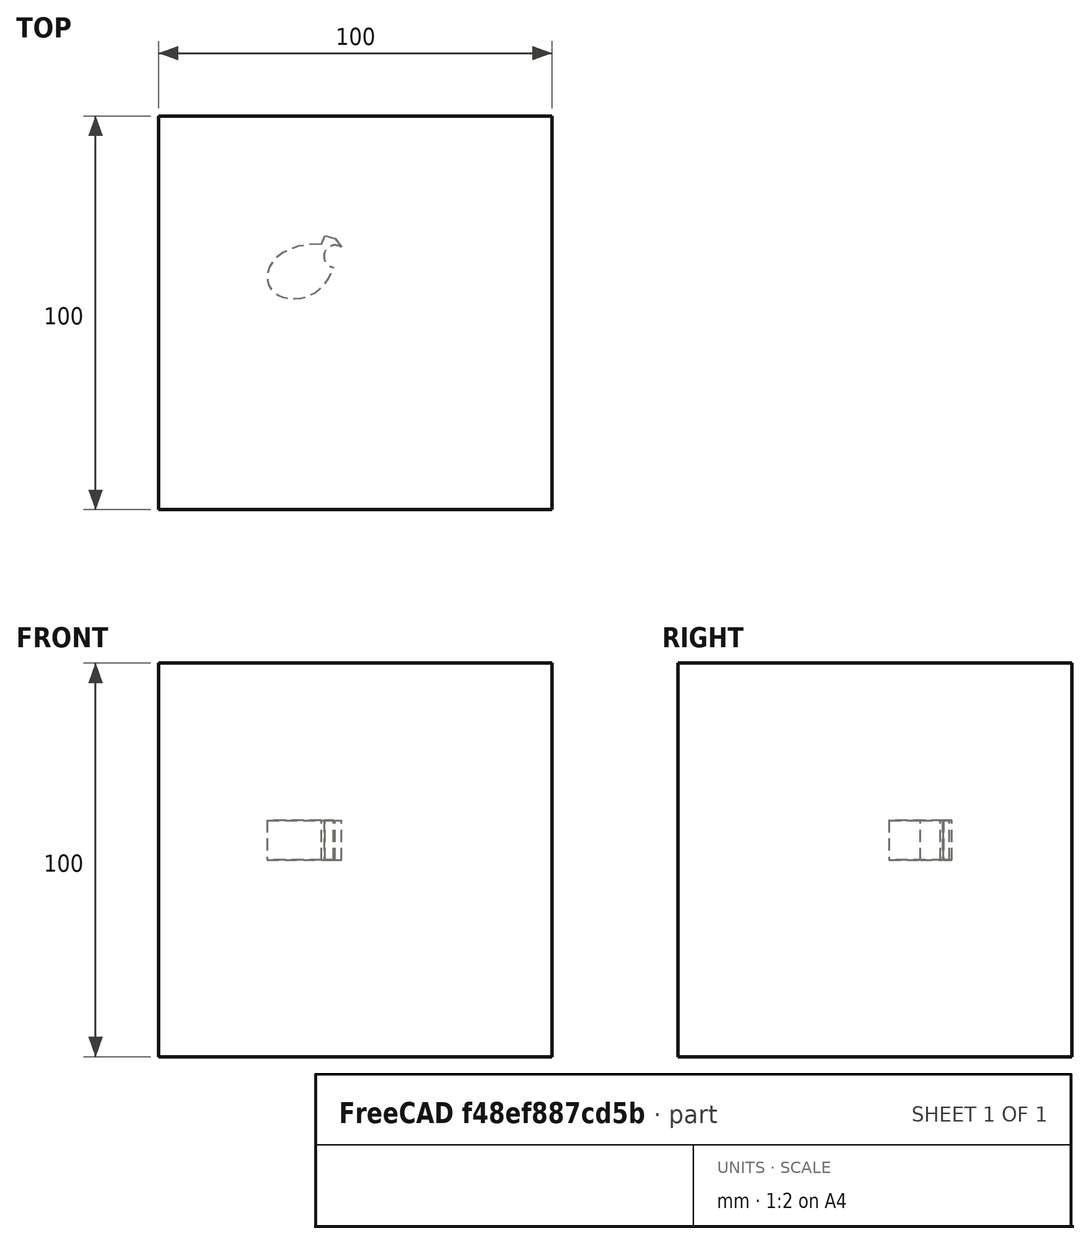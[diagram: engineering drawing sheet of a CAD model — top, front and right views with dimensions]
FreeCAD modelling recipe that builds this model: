
FCSTD DOCUMENT  (FreeCAD 0.19RUnknown)
Label: mirrorTest-1
License: All rights reserved
LicenseURL: http://en.wikipedia.org/wiki/All_rights_reserved
objects: App::DocumentObjectGroupPython×1248, App::Part×2, Part::FeaturePython×1, Sketcher::SketchObject×1, Part::Extrusion×1, Part::Mirroring×1
note: 4 computed .brp shape members not serialized (recipe doc carries the construction recipe); baked Part::Feature solids carry a one-line shape summary decoded from their .brp

FEATURE [App::DocumentObjectGroupPython] HALFPI  # scripted group (container) (typed FeaturePython)
  name = HALFPI
  value = pi/2.
FEATURE [App::DocumentObjectGroupPython] PI  # scripted group (container) (typed FeaturePython)
  name = PI
  value = 1.*pi
FEATURE [App::DocumentObjectGroupPython] TWOPI  # scripted group (container) (typed FeaturePython)
  name = TWOPI
  value = 2.*pi
FEATURE [App::DocumentObjectGroupPython] Constants  # scripted group (container) (typed FeaturePython)
  Group = -> [HALFPI,PI,TWOPI]
FEATURE [App::DocumentObjectGroupPython] Variables  # scripted group (container) (typed FeaturePython)
FEATURE [App::DocumentObjectGroupPython] Quantities  # scripted group (container) (typed FeaturePython)
FEATURE [App::DocumentObjectGroupPython] Isotopes  # scripted group (container) (typed FeaturePython)
FEATURE [App::DocumentObjectGroupPython] Elements  # scripted group (container) (typed FeaturePython)
FEATURE [App::DocumentObjectGroupPython] G4Isotopes  # scripted group (container) (typed FeaturePython)
FEATURE [App::DocumentObjectGroupPython] H_element  # scripted group (container) (typed FeaturePython)
  Z = 1
  atom_value = 1.008
  formula = H
  name = H_element
FEATURE [App::DocumentObjectGroupPython] He_element  # scripted group (container) (typed FeaturePython)
  Z = 2
  atom_value = 4.0026
  formula = He
  name = He_element
FEATURE [App::DocumentObjectGroupPython] Li_element  # scripted group (container) (typed FeaturePython)
  Z = 3
  atom_value = 6.94
  formula = Li
  name = Li_element
FEATURE [App::DocumentObjectGroupPython] Be_element  # scripted group (container) (typed FeaturePython)
  Z = 4
  atom_value = 9.01218
  formula = Be
  name = Be_element
FEATURE [App::DocumentObjectGroupPython] B_element  # scripted group (container) (typed FeaturePython)
  Z = 5
  atom_value = 10.81
  formula = B
  name = B_element
FEATURE [App::DocumentObjectGroupPython] C_element  # scripted group (container) (typed FeaturePython)
  Z = 6
  atom_value = 12.011
  formula = C
  name = C_element
FEATURE [App::DocumentObjectGroupPython] N_element  # scripted group (container) (typed FeaturePython)
  Z = 7
  atom_value = 14.007
  formula = N
  name = N_element
FEATURE [App::DocumentObjectGroupPython] O_element  # scripted group (container) (typed FeaturePython)
  Z = 8
  atom_value = 15.999
  formula = O
  name = O_element
FEATURE [App::DocumentObjectGroupPython] F_element  # scripted group (container) (typed FeaturePython)
  Z = 9
  atom_value = 18.9984
  formula = F
  name = F_element
FEATURE [App::DocumentObjectGroupPython] Ne_element  # scripted group (container) (typed FeaturePython)
  Z = 10
  atom_value = 20.1797
  formula = Ne
  name = Ne_element
FEATURE [App::DocumentObjectGroupPython] Na_element  # scripted group (container) (typed FeaturePython)
  Z = 11
  atom_value = 22.9898
  formula = Na
  name = Na_element
FEATURE [App::DocumentObjectGroupPython] Mg_element  # scripted group (container) (typed FeaturePython)
  Z = 12
  atom_value = 24.305
  formula = Mg
  name = Mg_element
FEATURE [App::DocumentObjectGroupPython] Al_element  # scripted group (container) (typed FeaturePython)
  Z = 13
  atom_value = 26.9815
  formula = Al
  name = Al_element
FEATURE [App::DocumentObjectGroupPython] Si_element  # scripted group (container) (typed FeaturePython)
  Z = 14
  atom_value = 28.085
  formula = Si
  name = Si_element
FEATURE [App::DocumentObjectGroupPython] P_element  # scripted group (container) (typed FeaturePython)
  Z = 15
  atom_value = 30.9738
  formula = P
  name = P_element
FEATURE [App::DocumentObjectGroupPython] S_element  # scripted group (container) (typed FeaturePython)
  Z = 16
  atom_value = 32.06
  formula = S
  name = S_element
FEATURE [App::DocumentObjectGroupPython] Cl_element  # scripted group (container) (typed FeaturePython)
  Z = 17
  atom_value = 35.45
  formula = Cl
  name = Cl_element
FEATURE [App::DocumentObjectGroupPython] Ar_element  # scripted group (container) (typed FeaturePython)
  Z = 18
  atom_value = 39.95
  formula = Ar
  name = Ar_element
FEATURE [App::DocumentObjectGroupPython] K_element  # scripted group (container) (typed FeaturePython)
  Z = 19
  atom_value = 39.0983
  formula = K
  name = K_element
FEATURE [App::DocumentObjectGroupPython] Ca_element  # scripted group (container) (typed FeaturePython)
  Z = 20
  atom_value = 40.078
  formula = Ca
  name = Ca_element
FEATURE [App::DocumentObjectGroupPython] Sc_element  # scripted group (container) (typed FeaturePython)
  Z = 21
  atom_value = 44.9559
  formula = Sc
  name = Sc_element
FEATURE [App::DocumentObjectGroupPython] Ti_element  # scripted group (container) (typed FeaturePython)
  Z = 22
  atom_value = 47.867
  formula = Ti
  name = Ti_element
FEATURE [App::DocumentObjectGroupPython] V_element  # scripted group (container) (typed FeaturePython)
  Z = 23
  atom_value = 50.9415
  formula = V
  name = V_element
FEATURE [App::DocumentObjectGroupPython] Cr_element  # scripted group (container) (typed FeaturePython)
  Z = 24
  atom_value = 51.9961
  formula = Cr
  name = Cr_element
FEATURE [App::DocumentObjectGroupPython] Mn_element  # scripted group (container) (typed FeaturePython)
  Z = 25
  atom_value = 54.938
  formula = Mn
  name = Mn_element
FEATURE [App::DocumentObjectGroupPython] Fe_element  # scripted group (container) (typed FeaturePython)
  Z = 26
  atom_value = 55.845
  formula = Fe
  name = Fe_element
FEATURE [App::DocumentObjectGroupPython] Co_element  # scripted group (container) (typed FeaturePython)
  Z = 27
  atom_value = 58.9332
  formula = Co
  name = Co_element
FEATURE [App::DocumentObjectGroupPython] Ni_element  # scripted group (container) (typed FeaturePython)
  Z = 28
  atom_value = 58.6934
  formula = Ni
  name = Ni_element
FEATURE [App::DocumentObjectGroupPython] Cu_element  # scripted group (container) (typed FeaturePython)
  Z = 29
  atom_value = 63.546
  formula = Cu
  name = Cu_element
FEATURE [App::DocumentObjectGroupPython] Zn_element  # scripted group (container) (typed FeaturePython)
  Z = 30
  atom_value = 65.38
  formula = Zn
  name = Zn_element
FEATURE [App::DocumentObjectGroupPython] Ga_element  # scripted group (container) (typed FeaturePython)
  Z = 31
  atom_value = 69.723
  formula = Ga
  name = Ga_element
FEATURE [App::DocumentObjectGroupPython] Ge_element  # scripted group (container) (typed FeaturePython)
  Z = 32
  atom_value = 72.63
  formula = Ge
  name = Ge_element
FEATURE [App::DocumentObjectGroupPython] As_element  # scripted group (container) (typed FeaturePython)
  Z = 33
  atom_value = 74.9216
  formula = As
  name = As_element
FEATURE [App::DocumentObjectGroupPython] Se_element  # scripted group (container) (typed FeaturePython)
  Z = 34
  atom_value = 78.971
  formula = Se
  name = Se_element
FEATURE [App::DocumentObjectGroupPython] Br_element  # scripted group (container) (typed FeaturePython)
  Z = 35
  atom_value = 79.904
  formula = Br
  name = Br_element
FEATURE [App::DocumentObjectGroupPython] Kr_element  # scripted group (container) (typed FeaturePython)
  Z = 36
  atom_value = 83.798
  formula = Kr
  name = Kr_element
FEATURE [App::DocumentObjectGroupPython] Rb_element  # scripted group (container) (typed FeaturePython)
  Z = 37
  atom_value = 85.4678
  formula = Rb
  name = Rb_element
FEATURE [App::DocumentObjectGroupPython] Sr_element  # scripted group (container) (typed FeaturePython)
  Z = 38
  atom_value = 87.62
  formula = Sr
  name = Sr_element
FEATURE [App::DocumentObjectGroupPython] Y_element  # scripted group (container) (typed FeaturePython)
  Z = 39
  atom_value = 88.9058
  formula = Y
  name = Y_element
FEATURE [App::DocumentObjectGroupPython] Zr_element  # scripted group (container) (typed FeaturePython)
  Z = 40
  atom_value = 91.224
  formula = Zr
  name = Zr_element
FEATURE [App::DocumentObjectGroupPython] Nb_element  # scripted group (container) (typed FeaturePython)
  Z = 41
  atom_value = 92.9064
  formula = Nb
  name = Nb_element
FEATURE [App::DocumentObjectGroupPython] Mo_element  # scripted group (container) (typed FeaturePython)
  Z = 42
  atom_value = 95.95
  formula = Mo
  name = Mo_element
FEATURE [App::DocumentObjectGroupPython] Tc_element  # scripted group (container) (typed FeaturePython)
  Z = 43
  atom_value = 97
  formula = Tc
  name = Tc_element
FEATURE [App::DocumentObjectGroupPython] Ru_element  # scripted group (container) (typed FeaturePython)
  Z = 44
  atom_value = 101.07
  formula = Ru
  name = Ru_element
FEATURE [App::DocumentObjectGroupPython] Rh_element  # scripted group (container) (typed FeaturePython)
  Z = 45
  atom_value = 102.905
  formula = Rh
  name = Rh_element
FEATURE [App::DocumentObjectGroupPython] Pd_element  # scripted group (container) (typed FeaturePython)
  Z = 46
  atom_value = 106.42
  formula = Pd
  name = Pd_element
FEATURE [App::DocumentObjectGroupPython] Ag_element  # scripted group (container) (typed FeaturePython)
  Z = 47
  atom_value = 107.868
  formula = Ag
  name = Ag_element
FEATURE [App::DocumentObjectGroupPython] Cd_element  # scripted group (container) (typed FeaturePython)
  Z = 48
  atom_value = 112.414
  formula = Cd
  name = Cd_element
FEATURE [App::DocumentObjectGroupPython] In_element  # scripted group (container) (typed FeaturePython)
  Z = 49
  atom_value = 114.818
  formula = In
  name = In_element
FEATURE [App::DocumentObjectGroupPython] Sn_element  # scripted group (container) (typed FeaturePython)
  Z = 50
  atom_value = 118.71
  formula = Sn
  name = Sn_element
FEATURE [App::DocumentObjectGroupPython] Sb_element  # scripted group (container) (typed FeaturePython)
  Z = 51
  atom_value = 121.76
  formula = Sb
  name = Sb_element
FEATURE [App::DocumentObjectGroupPython] Te_element  # scripted group (container) (typed FeaturePython)
  Z = 52
  atom_value = 127.6
  formula = Te
  name = Te_element
FEATURE [App::DocumentObjectGroupPython] I_element  # scripted group (container) (typed FeaturePython)
  Z = 53
  atom_value = 126.904
  formula = I
  name = I_element
FEATURE [App::DocumentObjectGroupPython] Xe_element  # scripted group (container) (typed FeaturePython)
  Z = 54
  atom_value = 131.293
  formula = Xe
  name = Xe_element
FEATURE [App::DocumentObjectGroupPython] Cs_element  # scripted group (container) (typed FeaturePython)
  Z = 55
  atom_value = 132.905
  formula = Cs
  name = Cs_element
FEATURE [App::DocumentObjectGroupPython] Ba_element  # scripted group (container) (typed FeaturePython)
  Z = 56
  atom_value = 137.327
  formula = Ba
  name = Ba_element
FEATURE [App::DocumentObjectGroupPython] La_element  # scripted group (container) (typed FeaturePython)
  Z = 57
  atom_value = 138.905
  formula = La
  name = La_element
FEATURE [App::DocumentObjectGroupPython] Ce_element  # scripted group (container) (typed FeaturePython)
  Z = 58
  atom_value = 140.116
  formula = Ce
  name = Ce_element
FEATURE [App::DocumentObjectGroupPython] Pr_element  # scripted group (container) (typed FeaturePython)
  Z = 59
  atom_value = 140.908
  formula = Pr
  name = Pr_element
FEATURE [App::DocumentObjectGroupPython] Nd_element  # scripted group (container) (typed FeaturePython)
  Z = 60
  atom_value = 144.242
  formula = Nd
  name = Nd_element
FEATURE [App::DocumentObjectGroupPython] Pm_element  # scripted group (container) (typed FeaturePython)
  Z = 61
  atom_value = 145
  formula = Pm
  name = Pm_element
FEATURE [App::DocumentObjectGroupPython] Sm_element  # scripted group (container) (typed FeaturePython)
  Z = 62
  atom_value = 150.36
  formula = Sm
  name = Sm_element
FEATURE [App::DocumentObjectGroupPython] Eu_element  # scripted group (container) (typed FeaturePython)
  Z = 63
  atom_value = 151.964
  formula = Eu
  name = Eu_element
FEATURE [App::DocumentObjectGroupPython] Gd_element  # scripted group (container) (typed FeaturePython)
  Z = 64
  atom_value = 157.25
  formula = Gd
  name = Gd_element
FEATURE [App::DocumentObjectGroupPython] Tb_element  # scripted group (container) (typed FeaturePython)
  Z = 65
  atom_value = 158.925
  formula = Tb
  name = Tb_element
FEATURE [App::DocumentObjectGroupPython] Dy_element  # scripted group (container) (typed FeaturePython)
  Z = 66
  atom_value = 162.5
  formula = Dy
  name = Dy_element
FEATURE [App::DocumentObjectGroupPython] Ho_element  # scripted group (container) (typed FeaturePython)
  Z = 67
  atom_value = 164.93
  formula = Ho
  name = Ho_element
FEATURE [App::DocumentObjectGroupPython] Er_element  # scripted group (container) (typed FeaturePython)
  Z = 68
  atom_value = 167.259
  formula = Er
  name = Er_element
FEATURE [App::DocumentObjectGroupPython] Tm_element  # scripted group (container) (typed FeaturePython)
  Z = 69
  atom_value = 168.934
  formula = Tm
  name = Tm_element
FEATURE [App::DocumentObjectGroupPython] Yb_element  # scripted group (container) (typed FeaturePython)
  Z = 70
  atom_value = 173.045
  formula = Yb
  name = Yb_element
FEATURE [App::DocumentObjectGroupPython] Lu_element  # scripted group (container) (typed FeaturePython)
  Z = 71
  atom_value = 174.967
  formula = Lu
  name = Lu_element
FEATURE [App::DocumentObjectGroupPython] Hf_element  # scripted group (container) (typed FeaturePython)
  Z = 72
  atom_value = 178.49
  formula = Hf
  name = Hf_element
FEATURE [App::DocumentObjectGroupPython] Ta_element  # scripted group (container) (typed FeaturePython)
  Z = 73
  atom_value = 180.948
  formula = Ta
  name = Ta_element
FEATURE [App::DocumentObjectGroupPython] W_element  # scripted group (container) (typed FeaturePython)
  Z = 74
  atom_value = 183.84
  formula = W
  name = W_element
FEATURE [App::DocumentObjectGroupPython] Re_element  # scripted group (container) (typed FeaturePython)
  Z = 75
  atom_value = 186.207
  formula = Re
  name = Re_element
FEATURE [App::DocumentObjectGroupPython] Os_element  # scripted group (container) (typed FeaturePython)
  Z = 76
  atom_value = 190.23
  formula = Os
  name = Os_element
FEATURE [App::DocumentObjectGroupPython] Ir_element  # scripted group (container) (typed FeaturePython)
  Z = 77
  atom_value = 192.217
  formula = Ir
  name = Ir_element
FEATURE [App::DocumentObjectGroupPython] Pt_element  # scripted group (container) (typed FeaturePython)
  Z = 78
  atom_value = 195.084
  formula = Pt
  name = Pt_element
FEATURE [App::DocumentObjectGroupPython] Au_element  # scripted group (container) (typed FeaturePython)
  Z = 79
  atom_value = 196.967
  formula = Au
  name = Au_element
FEATURE [App::DocumentObjectGroupPython] Hg_element  # scripted group (container) (typed FeaturePython)
  Z = 80
  atom_value = 200.592
  formula = Hg
  name = Hg_element
FEATURE [App::DocumentObjectGroupPython] Tl_element  # scripted group (container) (typed FeaturePython)
  Z = 81
  atom_value = 204.38
  formula = Tl
  name = Tl_element
FEATURE [App::DocumentObjectGroupPython] Pb_element  # scripted group (container) (typed FeaturePython)
  Z = 82
  atom_value = 207.2
  formula = Pb
  name = Pb_element
FEATURE [App::DocumentObjectGroupPython] Bi_element  # scripted group (container) (typed FeaturePython)
  Z = 83
  atom_value = 208.98
  formula = Bi
  name = Bi_element
FEATURE [App::DocumentObjectGroupPython] Po_element  # scripted group (container) (typed FeaturePython)
  Z = 84
  atom_value = 209
  formula = Po
  name = Po_element
FEATURE [App::DocumentObjectGroupPython] At_element  # scripted group (container) (typed FeaturePython)
  Z = 85
  atom_value = 210
  formula = At
  name = At_element
FEATURE [App::DocumentObjectGroupPython] Rn_element  # scripted group (container) (typed FeaturePython)
  Z = 86
  atom_value = 222
  formula = Rn
  name = Rn_element
FEATURE [App::DocumentObjectGroupPython] Fr_element  # scripted group (container) (typed FeaturePython)
  Z = 87
  atom_value = 223
  formula = Fr
  name = Fr_element
FEATURE [App::DocumentObjectGroupPython] Ra_element  # scripted group (container) (typed FeaturePython)
  Z = 88
  atom_value = 226
  formula = Ra
  name = Ra_element
FEATURE [App::DocumentObjectGroupPython] Ac_element  # scripted group (container) (typed FeaturePython)
  Z = 89
  atom_value = 227
  formula = Ac
  name = Ac_element
FEATURE [App::DocumentObjectGroupPython] Th_element  # scripted group (container) (typed FeaturePython)
  Z = 90
  atom_value = 232.038
  formula = Th
  name = Th_element
FEATURE [App::DocumentObjectGroupPython] Pa_element  # scripted group (container) (typed FeaturePython)
  Z = 91
  atom_value = 231.036
  formula = Pa
  name = Pa_element
FEATURE [App::DocumentObjectGroupPython] U_element  # scripted group (container) (typed FeaturePython)
  Z = 92
  atom_value = 238.029
  formula = U
  name = U_element
FEATURE [App::DocumentObjectGroupPython] Np_element  # scripted group (container) (typed FeaturePython)
  Z = 93
  atom_value = 237
  formula = Np
  name = Np_element
FEATURE [App::DocumentObjectGroupPython] Pu_element  # scripted group (container) (typed FeaturePython)
  Z = 94
  atom_value = 244
  formula = Pu
  name = Pu_element
FEATURE [App::DocumentObjectGroupPython] Am_element  # scripted group (container) (typed FeaturePython)
  Z = 95
  atom_value = 243
  formula = Am
  name = Am_element
FEATURE [App::DocumentObjectGroupPython] Cm_element  # scripted group (container) (typed FeaturePython)
  Z = 96
  atom_value = 247
  formula = Cm
  name = Cm_element
FEATURE [App::DocumentObjectGroupPython] Bk_element  # scripted group (container) (typed FeaturePython)
  Z = 97
  atom_value = 247
  formula = Bk
  name = Bk_element
FEATURE [App::DocumentObjectGroupPython] Cf_element  # scripted group (container) (typed FeaturePython)
  Z = 98
  atom_value = 251
  formula = Cf
  name = Cf_element
FEATURE [App::DocumentObjectGroupPython] G4Elements  # scripted group (container) (typed FeaturePython)
  Group = -> [H_element,He_element,Li_element,Be_element,B_element,C_element,N_element,O_element,F_element,Ne_element,Na_element,Mg_element,Al_element,Si_element,P_element,S_element,Cl_element,Ar_element,K_element,Ca_element,Sc_element,Ti_element,V_element,Cr_element,Mn_element,Fe_element,Co_element,Ni_element,Cu_element,Zn_element,Ga_element,Ge_element,As_element,Se_element,Br_element,Kr_element,Rb_element,+61 more]
FEATURE [App::DocumentObjectGroupPython] H_element001  label="H_element : 0.101"  # scripted group (container) (typed FeaturePython)
  n = 0.101327
FEATURE [App::DocumentObjectGroupPython] C_element001  label="C_element : 0.775"  # scripted group (container) (typed FeaturePython)
  n = 0.7755
FEATURE [App::DocumentObjectGroupPython] N_element001  label="N_element : 0.035"  # scripted group (container) (typed FeaturePython)
  n = 0.035057
FEATURE [App::DocumentObjectGroupPython] O_element001  label="O_element : 0.052"  # scripted group (container) (typed FeaturePython)
  n = 0.0523159
FEATURE [App::DocumentObjectGroupPython] F_element001  label="F_element : 0.017"  # scripted group (container) (typed FeaturePython)
  n = 0.017422
FEATURE [App::DocumentObjectGroupPython] Ca_element001  label="Ca_element : 0.018"  # scripted group (container) (typed FeaturePython)
  n = 0.018378
FEATURE [App::DocumentObjectGroupPython] G4_A_150_TISSUE  label="G4_A-150_TISSUE"  # scripted group (container) (typed FeaturePython)
  Dunit = g/cm3
  Dvalue = 1.127
  Group = -> [H_element001,C_element001,N_element001,O_element001,F_element001,Ca_element001]
  conduct = 2
  density = 1
  expand = 3
  formula = G4_A-150_TISSUE
  name = G4_A-150_TISSUE
  specific = 4
FEATURE [App::DocumentObjectGroupPython] C_element002  label="C_element : 3"  # scripted group (container) (typed FeaturePython)
  n = 3
  ref = C_element
FEATURE [App::DocumentObjectGroupPython] H_element002  label="H_element : 6"  # scripted group (container) (typed FeaturePython)
  n = 6
  ref = H_element
FEATURE [App::DocumentObjectGroupPython] O_element002  label="O_element : 1"  # scripted group (container) (typed FeaturePython)
  n = 1
  ref = O_element
FEATURE [App::DocumentObjectGroupPython] G4_ACETONE  # scripted group (container) (typed FeaturePython)
  Dunit = g/cm3
  Dvalue = 0.7899
  Group = -> [C_element002,H_element002,O_element002]
  conduct = 2
  density = 1
  expand = 3
  formula = G4_ACETONE
  name = G4_ACETONE
  specific = 4
FEATURE [App::DocumentObjectGroupPython] C_element003  label="C_element : 2"  # scripted group (container) (typed FeaturePython)
  n = 2
  ref = C_element
FEATURE [App::DocumentObjectGroupPython] H_element003  label="H_element : 2"  # scripted group (container) (typed FeaturePython)
  n = 2
  ref = H_element
FEATURE [App::DocumentObjectGroupPython] G4_ACETYLENE  # scripted group (container) (typed FeaturePython)
  Dunit = g/cm3
  Dvalue = 0.0010967
  Group = -> [C_element003,H_element003]
  conduct = 2
  density = 1
  expand = 3
  formula = G4_ACETYLENE
  name = G4_ACETYLENE
  specific = 4
FEATURE [App::DocumentObjectGroupPython] C_element004  label="C_element : 5"  # scripted group (container) (typed FeaturePython)
  n = 5
  ref = C_element
FEATURE [App::DocumentObjectGroupPython] H_element004  label="H_element : 5"  # scripted group (container) (typed FeaturePython)
  n = 5
  ref = H_element
FEATURE [App::DocumentObjectGroupPython] N_element002  label="N_element : 5"  # scripted group (container) (typed FeaturePython)
  n = 5
  ref = N_element
FEATURE [App::DocumentObjectGroupPython] G4_ADENINE  # scripted group (container) (typed FeaturePython)
  Dunit = g/cm3
  Dvalue = 1.6
  Group = -> [C_element004,H_element004,N_element002]
  conduct = 2
  density = 1
  expand = 3
  formula = G4_ADENINE
  name = G4_ADENINE
  specific = 4
FEATURE [App::DocumentObjectGroupPython] H_element005  label="H_element : 0.114"  # scripted group (container) (typed FeaturePython)
  n = 0.114
FEATURE [App::DocumentObjectGroupPython] C_element005  label="C_element : 0.598"  # scripted group (container) (typed FeaturePython)
  n = 0.598
FEATURE [App::DocumentObjectGroupPython] N_element003  label="N_element : 0.007"  # scripted group (container) (typed FeaturePython)
  n = 0.007
FEATURE [App::DocumentObjectGroupPython] O_element003  label="O_element : 0.278"  # scripted group (container) (typed FeaturePython)
  n = 0.278
FEATURE [App::DocumentObjectGroupPython] Na_element001  label="Na_element : 0.001"  # scripted group (container) (typed FeaturePython)
  n = 0.001
FEATURE [App::DocumentObjectGroupPython] S_element001  label="S_element : 0.001"  # scripted group (container) (typed FeaturePython)
  n = 0.001
FEATURE [App::DocumentObjectGroupPython] Cl_element001  label="Cl_element : 0.001"  # scripted group (container) (typed FeaturePython)
  n = 0.001
FEATURE [App::DocumentObjectGroupPython] G4_ADIPOSE_TISSUE_ICRP  # scripted group (container) (typed FeaturePython)
  Dunit = g/cm3
  Dvalue = 0.95
  Group = -> [H_element005,C_element005,N_element003,O_element003,Na_element001,S_element001,Cl_element001]
  conduct = 2
  density = 1
  expand = 3
  formula = G4_ADIPOSE_TISSUE_ICRP
  name = G4_ADIPOSE_TISSUE_ICRP
  specific = 4
FEATURE [App::DocumentObjectGroupPython] C_element006  label="C_element : 0.000"  # scripted group (container) (typed FeaturePython)
  n = 0.000124
FEATURE [App::DocumentObjectGroupPython] N_element004  label="N_element : 0.755"  # scripted group (container) (typed FeaturePython)
  n = 0.755268
FEATURE [App::DocumentObjectGroupPython] O_element004  label="O_element : 0.232"  # scripted group (container) (typed FeaturePython)
  n = 0.231781
FEATURE [App::DocumentObjectGroupPython] Ar_element001  label="Ar_element : 0.013"  # scripted group (container) (typed FeaturePython)
  n = 0.012827
FEATURE [App::DocumentObjectGroupPython] G4_AIR  # scripted group (container) (typed FeaturePython)
  Dunit = g/cm3
  Dvalue = 0.00120479
  Group = -> [C_element006,N_element004,O_element004,Ar_element001]
  conduct = 2
  density = 1
  expand = 3
  formula = G4_AIR
  name = G4_AIR
  specific = 4
FEATURE [App::DocumentObjectGroupPython] C_element007  label="C_element : 006"  # scripted group (container) (typed FeaturePython)
  n = 3
  ref = C_element
FEATURE [App::DocumentObjectGroupPython] H_element006  label="H_element : 7"  # scripted group (container) (typed FeaturePython)
  n = 7
  ref = H_element
FEATURE [App::DocumentObjectGroupPython] N_element005  label="N_element : 1"  # scripted group (container) (typed FeaturePython)
  n = 1
  ref = N_element
FEATURE [App::DocumentObjectGroupPython] O_element005  label="O_element : 2"  # scripted group (container) (typed FeaturePython)
  n = 2
  ref = O_element
FEATURE [App::DocumentObjectGroupPython] G4_ALANINE  # scripted group (container) (typed FeaturePython)
  Dunit = g/cm3
  Dvalue = 1.42
  Group = -> [C_element007,H_element006,N_element005,O_element005]
  conduct = 2
  density = 1
  expand = 3
  formula = G4_ALANINE
  name = G4_ALANINE
  specific = 4
FEATURE [App::DocumentObjectGroupPython] Al_element001  label="Al_element : 2"  # scripted group (container) (typed FeaturePython)
  n = 2
  ref = Al_element
FEATURE [App::DocumentObjectGroupPython] O_element006  label="O_element : 3"  # scripted group (container) (typed FeaturePython)
  n = 3
  ref = O_element
FEATURE [App::DocumentObjectGroupPython] G4_ALUMINUM_OXIDE  # scripted group (container) (typed FeaturePython)
  Dunit = g/cm3
  Dvalue = 3.97
  Group = -> [Al_element001,O_element006]
  conduct = 2
  density = 1
  expand = 3
  formula = G4_ALUMINUM_OXIDE
  name = G4_ALUMINUM_OXIDE
  specific = 4
FEATURE [App::DocumentObjectGroupPython] H_element007  label="H_element : 0.106"  # scripted group (container) (typed FeaturePython)
  n = 0.10593
FEATURE [App::DocumentObjectGroupPython] C_element008  label="C_element : 0.789"  # scripted group (container) (typed FeaturePython)
  n = 0.788974
FEATURE [App::DocumentObjectGroupPython] O_element007  label="O_element : 0.105"  # scripted group (container) (typed FeaturePython)
  n = 0.105096
FEATURE [App::DocumentObjectGroupPython] G4_AMBER  # scripted group (container) (typed FeaturePython)
  Dunit = g/cm3
  Dvalue = 1.1
  Group = -> [H_element007,C_element008,O_element007]
  conduct = 2
  density = 1
  expand = 3
  formula = G4_AMBER
  name = G4_AMBER
  specific = 4
FEATURE [App::DocumentObjectGroupPython] N_element006  label="N_element : 006"  # scripted group (container) (typed FeaturePython)
  n = 1
  ref = N_element
FEATURE [App::DocumentObjectGroupPython] H_element008  label="H_element : 3"  # scripted group (container) (typed FeaturePython)
  n = 3
  ref = H_element
FEATURE [App::DocumentObjectGroupPython] G4_AMMONIA  # scripted group (container) (typed FeaturePython)
  Dunit = g/cm3
  Dvalue = 0.000826019
  Group = -> [N_element006,H_element008]
  conduct = 2
  density = 1
  expand = 3
  formula = G4_AMMONIA
  name = G4_AMMONIA
  specific = 4
FEATURE [App::DocumentObjectGroupPython] C_element009  label="C_element : 6"  # scripted group (container) (typed FeaturePython)
  n = 6
  ref = C_element
FEATURE [App::DocumentObjectGroupPython] H_element009  label="H_element : 008"  # scripted group (container) (typed FeaturePython)
  n = 7
  ref = H_element
FEATURE [App::DocumentObjectGroupPython] N_element007  label="N_element : 007"  # scripted group (container) (typed FeaturePython)
  n = 1
  ref = N_element
FEATURE [App::DocumentObjectGroupPython] G4_ANILINE  # scripted group (container) (typed FeaturePython)
  Dunit = g/cm3
  Dvalue = 1.0235
  Group = -> [C_element009,H_element009,N_element007]
  conduct = 2
  density = 1
  expand = 3
  formula = G4_ANILINE
  name = G4_ANILINE
  specific = 4
FEATURE [App::DocumentObjectGroupPython] C_element010  label="C_element : 14"  # scripted group (container) (typed FeaturePython)
  n = 14
  ref = C_element
FEATURE [App::DocumentObjectGroupPython] H_element010  label="H_element : 10"  # scripted group (container) (typed FeaturePython)
  n = 10
  ref = H_element
FEATURE [App::DocumentObjectGroupPython] G4_ANTHRACENE  # scripted group (container) (typed FeaturePython)
  Dunit = g/cm3
  Dvalue = 1.283
  Group = -> [C_element010,H_element010]
  conduct = 2
  density = 1
  expand = 3
  formula = G4_ANTHRACENE
  name = G4_ANTHRACENE
  specific = 4
FEATURE [App::DocumentObjectGroupPython] H_element011  label="H_element : 0.065"  # scripted group (container) (typed FeaturePython)
  n = 0.0654709
FEATURE [App::DocumentObjectGroupPython] C_element011  label="C_element : 0.537"  # scripted group (container) (typed FeaturePython)
  n = 0.536944
FEATURE [App::DocumentObjectGroupPython] N_element008  label="N_element : 0.021"  # scripted group (container) (typed FeaturePython)
  n = 0.0215
FEATURE [App::DocumentObjectGroupPython] O_element008  label="O_element : 0.032"  # scripted group (container) (typed FeaturePython)
  n = 0.032085
FEATURE [App::DocumentObjectGroupPython] F_element002  label="F_element : 0.167"  # scripted group (container) (typed FeaturePython)
  n = 0.167411
FEATURE [App::DocumentObjectGroupPython] Ca_element002  label="Ca_element : 0.177"  # scripted group (container) (typed FeaturePython)
  n = 0.176589
FEATURE [App::DocumentObjectGroupPython] G4_B_100_BONE  label="G4_B-100_BONE"  # scripted group (container) (typed FeaturePython)
  Dunit = g/cm3
  Dvalue = 1.45
  Group = -> [H_element011,C_element011,N_element008,O_element008,F_element002,Ca_element002]
  conduct = 2
  density = 1
  expand = 3
  formula = G4_B-100_BONE
  name = G4_B-100_BONE
  specific = 4
FEATURE [App::DocumentObjectGroupPython] H_element012  label="H_element : 0.057"  # scripted group (container) (typed FeaturePython)
  n = 0.057441
FEATURE [App::DocumentObjectGroupPython] C_element012  label="C_element : 0.790"  # scripted group (container) (typed FeaturePython)
  n = 0.774591
FEATURE [App::DocumentObjectGroupPython] O_element009  label="O_element : 0.168"  # scripted group (container) (typed FeaturePython)
  n = 0.167968
FEATURE [App::DocumentObjectGroupPython] G4_BAKELITE  # scripted group (container) (typed FeaturePython)
  Dunit = g/cm3
  Dvalue = 1.25
  Group = -> [H_element012,C_element012,O_element009]
  conduct = 2
  density = 1
  expand = 3
  formula = G4_BAKELITE
  name = G4_BAKELITE
  specific = 4
FEATURE [App::DocumentObjectGroupPython] Ba_element001  label="Ba_element : 1"  # scripted group (container) (typed FeaturePython)
  n = 1
  ref = Ba_element
FEATURE [App::DocumentObjectGroupPython] F_element003  label="F_element : 2"  # scripted group (container) (typed FeaturePython)
  n = 2
  ref = F_element
FEATURE [App::DocumentObjectGroupPython] G4_BARIUM_FLUORIDE  # scripted group (container) (typed FeaturePython)
  Dunit = g/cm3
  Dvalue = 4.89
  Group = -> [Ba_element001,F_element003]
  conduct = 2
  density = 1
  expand = 3
  formula = G4_BARIUM_FLUORIDE
  name = G4_BARIUM_FLUORIDE
  specific = 4
FEATURE [App::DocumentObjectGroupPython] Ba_element002  label="Ba_element : 002"  # scripted group (container) (typed FeaturePython)
  n = 1
  ref = Ba_element
FEATURE [App::DocumentObjectGroupPython] S_element002  label="S_element : 1"  # scripted group (container) (typed FeaturePython)
  n = 1
  ref = S_element
FEATURE [App::DocumentObjectGroupPython] O_element010  label="O_element : 4"  # scripted group (container) (typed FeaturePython)
  n = 4
  ref = O_element
FEATURE [App::DocumentObjectGroupPython] G4_BARIUM_SULFATE  # scripted group (container) (typed FeaturePython)
  Dunit = g/cm3
  Dvalue = 4.5
  Group = -> [Ba_element002,S_element002,O_element010]
  conduct = 2
  density = 1
  expand = 3
  formula = G4_BARIUM_SULFATE
  name = G4_BARIUM_SULFATE
  specific = 4
FEATURE [App::DocumentObjectGroupPython] C_element013  label="C_element : 007"  # scripted group (container) (typed FeaturePython)
  n = 6
  ref = C_element
FEATURE [App::DocumentObjectGroupPython] H_element013  label="H_element : 009"  # scripted group (container) (typed FeaturePython)
  n = 6
  ref = H_element
FEATURE [App::DocumentObjectGroupPython] G4_BENZENE  # scripted group (container) (typed FeaturePython)
  Dunit = g/cm3
  Dvalue = 0.87865
  Group = -> [C_element013,H_element013]
  conduct = 2
  density = 1
  expand = 3
  formula = G4_BENZENE
  name = G4_BENZENE
  specific = 4
FEATURE [App::DocumentObjectGroupPython] Be_element001  label="Be_element : 1"  # scripted group (container) (typed FeaturePython)
  n = 1
  ref = Be_element
FEATURE [App::DocumentObjectGroupPython] O_element011  label="O_element : 005"  # scripted group (container) (typed FeaturePython)
  n = 1
  ref = O_element
FEATURE [App::DocumentObjectGroupPython] G4_BERYLLIUM_OXIDE  # scripted group (container) (typed FeaturePython)
  Dunit = g/cm3
  Dvalue = 3.01
  Group = -> [Be_element001,O_element011]
  conduct = 2
  density = 1
  expand = 3
  formula = G4_BERYLLIUM_OXIDE
  name = G4_BERYLLIUM_OXIDE
  specific = 4
FEATURE [App::DocumentObjectGroupPython] Bi_element001  label="Bi_element : 4"  # scripted group (container) (typed FeaturePython)
  n = 4
  ref = Bi_element
FEATURE [App::DocumentObjectGroupPython] Ge_element001  label="Ge_element : 3"  # scripted group (container) (typed FeaturePython)
  n = 3
  ref = Ge_element
FEATURE [App::DocumentObjectGroupPython] O_element012  label="O_element : 12"  # scripted group (container) (typed FeaturePython)
  n = 12
  ref = O_element
FEATURE [App::DocumentObjectGroupPython] G4_BGO  # scripted group (container) (typed FeaturePython)
  Dunit = g/cm3
  Dvalue = 7.13
  Group = -> [Bi_element001,Ge_element001,O_element012]
  conduct = 2
  density = 1
  expand = 3
  formula = G4_BGO
  name = G4_BGO
  specific = 4
FEATURE [App::DocumentObjectGroupPython] H_element014  label="H_element : 0.102"  # scripted group (container) (typed FeaturePython)
  n = 0.102
FEATURE [App::DocumentObjectGroupPython] C_element014  label="C_element : 0.110"  # scripted group (container) (typed FeaturePython)
  n = 0.11
FEATURE [App::DocumentObjectGroupPython] N_element009  label="N_element : 0.033"  # scripted group (container) (typed FeaturePython)
  n = 0.033
FEATURE [App::DocumentObjectGroupPython] O_element013  label="O_element : 0.745"  # scripted group (container) (typed FeaturePython)
  n = 0.745
FEATURE [App::DocumentObjectGroupPython] Na_element002  label="Na_element : 0.002"  # scripted group (container) (typed FeaturePython)
  n = 0.001
FEATURE [App::DocumentObjectGroupPython] P_element001  label="P_element : 0.001"  # scripted group (container) (typed FeaturePython)
  n = 0.001
FEATURE [App::DocumentObjectGroupPython] S_element003  label="S_element : 0.002"  # scripted group (container) (typed FeaturePython)
  n = 0.002
FEATURE [App::DocumentObjectGroupPython] Cl_element002  label="Cl_element : 0.003"  # scripted group (container) (typed FeaturePython)
  n = 0.003
FEATURE [App::DocumentObjectGroupPython] K_element001  label="K_element : 0.002"  # scripted group (container) (typed FeaturePython)
  n = 0.002
FEATURE [App::DocumentObjectGroupPython] Fe_element001  label="Fe_element : 0.001"  # scripted group (container) (typed FeaturePython)
  n = 0.001
FEATURE [App::DocumentObjectGroupPython] G4_BLOOD_ICRP  # scripted group (container) (typed FeaturePython)
  Dunit = g/cm3
  Dvalue = 1.06
  Group = -> [H_element014,C_element014,N_element009,O_element013,Na_element002,P_element001,S_element003,Cl_element002,K_element001,Fe_element001]
  conduct = 2
  density = 1
  expand = 3
  formula = G4_BLOOD_ICRP
  name = G4_BLOOD_ICRP
  specific = 4
FEATURE [App::DocumentObjectGroupPython] H_element015  label="H_element : 0.064"  # scripted group (container) (typed FeaturePython)
  n = 0.064
FEATURE [App::DocumentObjectGroupPython] C_element015  label="C_element : 0.278"  # scripted group (container) (typed FeaturePython)
  n = 0.278
FEATURE [App::DocumentObjectGroupPython] N_element010  label="N_element : 0.027"  # scripted group (container) (typed FeaturePython)
  n = 0.027
FEATURE [App::DocumentObjectGroupPython] O_element014  label="O_element : 0.410"  # scripted group (container) (typed FeaturePython)
  n = 0.41
FEATURE [App::DocumentObjectGroupPython] Mg_element001  label="Mg_element : 0.002"  # scripted group (container) (typed FeaturePython)
  n = 0.002
FEATURE [App::DocumentObjectGroupPython] P_element002  label="P_element : 0.070"  # scripted group (container) (typed FeaturePython)
  n = 0.07
FEATURE [App::DocumentObjectGroupPython] S_element004  label="S_element : 0.003"  # scripted group (container) (typed FeaturePython)
  n = 0.002
FEATURE [App::DocumentObjectGroupPython] Ca_element003  label="Ca_element : 0.147"  # scripted group (container) (typed FeaturePython)
  n = 0.147
FEATURE [App::DocumentObjectGroupPython] G4_BONE_COMPACT_ICRU  # scripted group (container) (typed FeaturePython)
  Dunit = g/cm3
  Dvalue = 1.85
  Group = -> [H_element015,C_element015,N_element010,O_element014,Mg_element001,P_element002,S_element004,Ca_element003]
  conduct = 2
  density = 1
  expand = 3
  formula = G4_BONE_COMPACT_ICRU
  name = G4_BONE_COMPACT_ICRU
  specific = 4
FEATURE [App::DocumentObjectGroupPython] H_element016  label="H_element : 0.034"  # scripted group (container) (typed FeaturePython)
  n = 0.034
FEATURE [App::DocumentObjectGroupPython] C_element016  label="C_element : 0.155"  # scripted group (container) (typed FeaturePython)
  n = 0.155
FEATURE [App::DocumentObjectGroupPython] N_element011  label="N_element : 0.042"  # scripted group (container) (typed FeaturePython)
  n = 0.042
FEATURE [App::DocumentObjectGroupPython] O_element015  label="O_element : 0.435"  # scripted group (container) (typed FeaturePython)
  n = 0.435
FEATURE [App::DocumentObjectGroupPython] Na_element003  label="Na_element : 0.003"  # scripted group (container) (typed FeaturePython)
  n = 0.001
FEATURE [App::DocumentObjectGroupPython] Mg_element002  label="Mg_element : 0.003"  # scripted group (container) (typed FeaturePython)
  n = 0.002
FEATURE [App::DocumentObjectGroupPython] P_element003  label="P_element : 0.103"  # scripted group (container) (typed FeaturePython)
  n = 0.103
FEATURE [App::DocumentObjectGroupPython] S_element005  label="S_element : 0.004"  # scripted group (container) (typed FeaturePython)
  n = 0.003
FEATURE [App::DocumentObjectGroupPython] Ca_element004  label="Ca_element : 0.225"  # scripted group (container) (typed FeaturePython)
  n = 0.225
FEATURE [App::DocumentObjectGroupPython] G4_BONE_CORTICAL_ICRP  # scripted group (container) (typed FeaturePython)
  Dunit = g/cm3
  Dvalue = 1.92
  Group = -> [H_element016,C_element016,N_element011,O_element015,Na_element003,Mg_element002,P_element003,S_element005,Ca_element004]
  conduct = 2
  density = 1
  expand = 3
  formula = G4_BONE_CORTICAL_ICRP
  name = G4_BONE_CORTICAL_ICRP
  specific = 4
FEATURE [App::DocumentObjectGroupPython] B_element001  label="B_element : 4"  # scripted group (container) (typed FeaturePython)
  n = 4
  ref = B_element
FEATURE [App::DocumentObjectGroupPython] C_element017  label="C_element : 1"  # scripted group (container) (typed FeaturePython)
  n = 1
  ref = C_element
FEATURE [App::DocumentObjectGroupPython] G4_BORON_CARBIDE  # scripted group (container) (typed FeaturePython)
  Dunit = g/cm3
  Dvalue = 2.52
  Group = -> [B_element001,C_element017]
  conduct = 2
  density = 1
  expand = 3
  formula = G4_BORON_CARBIDE
  name = G4_BORON_CARBIDE
  specific = 4
FEATURE [App::DocumentObjectGroupPython] B_element002  label="B_element : 2"  # scripted group (container) (typed FeaturePython)
  n = 2
  ref = B_element
FEATURE [App::DocumentObjectGroupPython] O_element016  label="O_element : 006"  # scripted group (container) (typed FeaturePython)
  n = 3
  ref = O_element
FEATURE [App::DocumentObjectGroupPython] G4_BORON_OXIDE  # scripted group (container) (typed FeaturePython)
  Dunit = g/cm3
  Dvalue = 1.812
  Group = -> [B_element002,O_element016]
  conduct = 2
  density = 1
  expand = 3
  formula = G4_BORON_OXIDE
  name = G4_BORON_OXIDE
  specific = 4
FEATURE [App::DocumentObjectGroupPython] H_element017  label="H_element : 0.107"  # scripted group (container) (typed FeaturePython)
  n = 0.107
FEATURE [App::DocumentObjectGroupPython] C_element018  label="C_element : 0.145"  # scripted group (container) (typed FeaturePython)
  n = 0.145
FEATURE [App::DocumentObjectGroupPython] N_element012  label="N_element : 0.022"  # scripted group (container) (typed FeaturePython)
  n = 0.022
FEATURE [App::DocumentObjectGroupPython] O_element017  label="O_element : 0.712"  # scripted group (container) (typed FeaturePython)
  n = 0.712
FEATURE [App::DocumentObjectGroupPython] Na_element004  label="Na_element : 0.004"  # scripted group (container) (typed FeaturePython)
  n = 0.002
FEATURE [App::DocumentObjectGroupPython] P_element004  label="P_element : 0.004"  # scripted group (container) (typed FeaturePython)
  n = 0.004
FEATURE [App::DocumentObjectGroupPython] S_element006  label="S_element : 0.005"  # scripted group (container) (typed FeaturePython)
  n = 0.002
FEATURE [App::DocumentObjectGroupPython] Cl_element003  label="Cl_element : 0.004"  # scripted group (container) (typed FeaturePython)
  n = 0.003
FEATURE [App::DocumentObjectGroupPython] K_element002  label="K_element : 0.003"  # scripted group (container) (typed FeaturePython)
  n = 0.003
FEATURE [App::DocumentObjectGroupPython] G4_BRAIN_ICRP  # scripted group (container) (typed FeaturePython)
  Dunit = g/cm3
  Dvalue = 1.04
  Group = -> [H_element017,C_element018,N_element012,O_element017,Na_element004,P_element004,S_element006,Cl_element003,K_element002]
  conduct = 2
  density = 1
  expand = 3
  formula = G4_BRAIN_ICRP
  name = G4_BRAIN_ICRP
  specific = 4
FEATURE [App::DocumentObjectGroupPython] C_element019  label="C_element : 4"  # scripted group (container) (typed FeaturePython)
  n = 4
  ref = C_element
FEATURE [App::DocumentObjectGroupPython] H_element018  label="H_element : 010"  # scripted group (container) (typed FeaturePython)
  n = 10
  ref = H_element
FEATURE [App::DocumentObjectGroupPython] G4_BUTANE  # scripted group (container) (typed FeaturePython)
  Dunit = g/cm3
  Dvalue = 0.00249343
  Group = -> [C_element019,H_element018]
  conduct = 2
  density = 1
  expand = 3
  formula = G4_BUTANE
  name = G4_BUTANE
  specific = 4
FEATURE [App::DocumentObjectGroupPython] C_element020  label="C_element : 008"  # scripted group (container) (typed FeaturePython)
  n = 4
  ref = C_element
FEATURE [App::DocumentObjectGroupPython] H_element019  label="H_element : 011"  # scripted group (container) (typed FeaturePython)
  n = 10
  ref = H_element
FEATURE [App::DocumentObjectGroupPython] O_element018  label="O_element : 007"  # scripted group (container) (typed FeaturePython)
  n = 1
  ref = O_element
FEATURE [App::DocumentObjectGroupPython] G4_N_BUTYL_ALCOHOL  label="G4_N-BUTYL_ALCOHOL"  # scripted group (container) (typed FeaturePython)
  Dunit = g/cm3
  Dvalue = 0.8098
  Group = -> [C_element020,H_element019,O_element018]
  conduct = 2
  density = 1
  expand = 3
  formula = G4_N-BUTYL_ALCOHOL
  name = G4_N-BUTYL_ALCOHOL
  specific = 4
FEATURE [App::DocumentObjectGroupPython] H_element020  label="H_element : 0.025"  # scripted group (container) (typed FeaturePython)
  n = 0.02468
FEATURE [App::DocumentObjectGroupPython] C_element021  label="C_element : 0.502"  # scripted group (container) (typed FeaturePython)
  n = 0.501611
FEATURE [App::DocumentObjectGroupPython] O_element019  label="O_element : 0.005"  # scripted group (container) (typed FeaturePython)
  n = 0.004527
FEATURE [App::DocumentObjectGroupPython] F_element004  label="F_element : 0.465"  # scripted group (container) (typed FeaturePython)
  n = 0.465209
FEATURE [App::DocumentObjectGroupPython] Si_element001  label="Si_element : 0.004"  # scripted group (container) (typed FeaturePython)
  n = 0.003973
FEATURE [App::DocumentObjectGroupPython] G4_C_552  label="G4_C-552"  # scripted group (container) (typed FeaturePython)
  Dunit = g/cm3
  Dvalue = 1.76
  Group = -> [H_element020,C_element021,O_element019,F_element004,Si_element001]
  conduct = 2
  density = 1
  expand = 3
  formula = G4_C-552
  name = G4_C-552
  specific = 4
FEATURE [App::DocumentObjectGroupPython] Cd_element001  label="Cd_element : 1"  # scripted group (container) (typed FeaturePython)
  n = 1
  ref = Cd_element
FEATURE [App::DocumentObjectGroupPython] Te_element001  label="Te_element : 1"  # scripted group (container) (typed FeaturePython)
  n = 1
  ref = Te_element
FEATURE [App::DocumentObjectGroupPython] G4_CADMIUM_TELLURIDE  # scripted group (container) (typed FeaturePython)
  Dunit = g/cm3
  Dvalue = 6.2
  Group = -> [Cd_element001,Te_element001]
  conduct = 2
  density = 1
  expand = 3
  formula = G4_CADMIUM_TELLURIDE
  name = G4_CADMIUM_TELLURIDE
  specific = 4
FEATURE [App::DocumentObjectGroupPython] Cd_element002  label="Cd_element : 002"  # scripted group (container) (typed FeaturePython)
  n = 1
  ref = Cd_element
FEATURE [App::DocumentObjectGroupPython] W_element001  label="W_element : 1"  # scripted group (container) (typed FeaturePython)
  n = 1
  ref = W_element
FEATURE [App::DocumentObjectGroupPython] O_element020  label="O_element : 008"  # scripted group (container) (typed FeaturePython)
  n = 4
  ref = O_element
FEATURE [App::DocumentObjectGroupPython] G4_CADMIUM_TUNGSTATE  # scripted group (container) (typed FeaturePython)
  Dunit = g/cm3
  Dvalue = 7.9
  Group = -> [Cd_element002,W_element001,O_element020]
  conduct = 2
  density = 1
  expand = 3
  formula = G4_CADMIUM_TUNGSTATE
  name = G4_CADMIUM_TUNGSTATE
  specific = 4
FEATURE [App::DocumentObjectGroupPython] Ca_element005  label="Ca_element : 1"  # scripted group (container) (typed FeaturePython)
  n = 1
  ref = Ca_element
FEATURE [App::DocumentObjectGroupPython] C_element022  label="C_element : 009"  # scripted group (container) (typed FeaturePython)
  n = 1
  ref = C_element
FEATURE [App::DocumentObjectGroupPython] O_element021  label="O_element : 009"  # scripted group (container) (typed FeaturePython)
  n = 3
  ref = O_element
FEATURE [App::DocumentObjectGroupPython] G4_CALCIUM_CARBONATE  # scripted group (container) (typed FeaturePython)
  Dunit = g/cm3
  Dvalue = 2.8
  Group = -> [Ca_element005,C_element022,O_element021]
  conduct = 2
  density = 1
  expand = 3
  formula = G4_CALCIUM_CARBONATE
  name = G4_CALCIUM_CARBONATE
  specific = 4
FEATURE [App::DocumentObjectGroupPython] Ca_element006  label="Ca_element : 002"  # scripted group (container) (typed FeaturePython)
  n = 1
  ref = Ca_element
FEATURE [App::DocumentObjectGroupPython] F_element005  label="F_element : 003"  # scripted group (container) (typed FeaturePython)
  n = 2
  ref = F_element
FEATURE [App::DocumentObjectGroupPython] G4_CALCIUM_FLUORIDE  # scripted group (container) (typed FeaturePython)
  Dunit = g/cm3
  Dvalue = 3.18
  Group = -> [Ca_element006,F_element005]
  conduct = 2
  density = 1
  expand = 3
  formula = G4_CALCIUM_FLUORIDE
  name = G4_CALCIUM_FLUORIDE
  specific = 4
FEATURE [App::DocumentObjectGroupPython] Ca_element007  label="Ca_element : 003"  # scripted group (container) (typed FeaturePython)
  n = 1
  ref = Ca_element
FEATURE [App::DocumentObjectGroupPython] O_element022  label="O_element : 010"  # scripted group (container) (typed FeaturePython)
  n = 1
  ref = O_element
FEATURE [App::DocumentObjectGroupPython] G4_CALCIUM_OXIDE  # scripted group (container) (typed FeaturePython)
  Dunit = g/cm3
  Dvalue = 3.3
  Group = -> [Ca_element007,O_element022]
  conduct = 2
  density = 1
  expand = 3
  formula = G4_CALCIUM_OXIDE
  name = G4_CALCIUM_OXIDE
  specific = 4
FEATURE [App::DocumentObjectGroupPython] Ca_element008  label="Ca_element : 004"  # scripted group (container) (typed FeaturePython)
  n = 1
  ref = Ca_element
FEATURE [App::DocumentObjectGroupPython] S_element007  label="S_element : 002"  # scripted group (container) (typed FeaturePython)
  n = 1
  ref = S_element
FEATURE [App::DocumentObjectGroupPython] O_element023  label="O_element : 011"  # scripted group (container) (typed FeaturePython)
  n = 4
  ref = O_element
FEATURE [App::DocumentObjectGroupPython] G4_CALCIUM_SULFATE  # scripted group (container) (typed FeaturePython)
  Dunit = g/cm3
  Dvalue = 2.96
  Group = -> [Ca_element008,S_element007,O_element023]
  conduct = 2
  density = 1
  expand = 3
  formula = G4_CALCIUM_SULFATE
  name = G4_CALCIUM_SULFATE
  specific = 4
FEATURE [App::DocumentObjectGroupPython] Ca_element009  label="Ca_element : 005"  # scripted group (container) (typed FeaturePython)
  n = 1
  ref = Ca_element
FEATURE [App::DocumentObjectGroupPython] W_element002  label="W_element : 002"  # scripted group (container) (typed FeaturePython)
  n = 1
  ref = W_element
FEATURE [App::DocumentObjectGroupPython] O_element024  label="O_element : 012"  # scripted group (container) (typed FeaturePython)
  n = 4
  ref = O_element
FEATURE [App::DocumentObjectGroupPython] G4_CALCIUM_TUNGSTATE  # scripted group (container) (typed FeaturePython)
  Dunit = g/cm3
  Dvalue = 6.062
  Group = -> [Ca_element009,W_element002,O_element024]
  conduct = 2
  density = 1
  expand = 3
  formula = G4_CALCIUM_TUNGSTATE
  name = G4_CALCIUM_TUNGSTATE
  specific = 4
FEATURE [App::DocumentObjectGroupPython] C_element023  label="C_element : 010"  # scripted group (container) (typed FeaturePython)
  n = 1
  ref = C_element
FEATURE [App::DocumentObjectGroupPython] O_element025  label="O_element : 013"  # scripted group (container) (typed FeaturePython)
  n = 2
  ref = O_element
FEATURE [App::DocumentObjectGroupPython] G4_CARBON_DIOXIDE  # scripted group (container) (typed FeaturePython)
  Dunit = g/cm3
  Dvalue = 0.00184212
  Group = -> [C_element023,O_element025]
  conduct = 2
  density = 1
  expand = 3
  formula = G4_CARBON_DIOXIDE
  name = G4_CARBON_DIOXIDE
  specific = 4
FEATURE [App::DocumentObjectGroupPython] C_element024  label="C_element : 011"  # scripted group (container) (typed FeaturePython)
  n = 1
  ref = C_element
FEATURE [App::DocumentObjectGroupPython] Cl_element004  label="Cl_element : 4"  # scripted group (container) (typed FeaturePython)
  n = 4
  ref = Cl_element
FEATURE [App::DocumentObjectGroupPython] G4_CARBON_TETRACHLORIDE  # scripted group (container) (typed FeaturePython)
  Dunit = g/cm3
  Dvalue = 1.594
  Group = -> [C_element024,Cl_element004]
  conduct = 2
  density = 1
  expand = 3
  formula = G4_CARBON_TETRACHLORIDE
  name = G4_CARBON_TETRACHLORIDE
  specific = 4
FEATURE [App::DocumentObjectGroupPython] C_element025  label="C_element : 012"  # scripted group (container) (typed FeaturePython)
  n = 6
  ref = C_element
FEATURE [App::DocumentObjectGroupPython] H_element021  label="H_element : 012"  # scripted group (container) (typed FeaturePython)
  n = 10
  ref = H_element
FEATURE [App::DocumentObjectGroupPython] O_element026  label="O_element : 5"  # scripted group (container) (typed FeaturePython)
  n = 5
  ref = O_element
FEATURE [App::DocumentObjectGroupPython] G4_CELLULOSE_CELLOPHANE  # scripted group (container) (typed FeaturePython)
  Dunit = g/cm3
  Dvalue = 1.42
  Group = -> [C_element025,H_element021,O_element026]
  conduct = 2
  density = 1
  expand = 3
  formula = G4_CELLULOSE_CELLOPHANE
  name = G4_CELLULOSE_CELLOPHANE
  specific = 4
FEATURE [App::DocumentObjectGroupPython] H_element022  label="H_element : 0.067"  # scripted group (container) (typed FeaturePython)
  n = 0.067125
FEATURE [App::DocumentObjectGroupPython] C_element026  label="C_element : 0.545"  # scripted group (container) (typed FeaturePython)
  n = 0.545403
FEATURE [App::DocumentObjectGroupPython] O_element027  label="O_element : 0.387"  # scripted group (container) (typed FeaturePython)
  n = 0.387472
FEATURE [App::DocumentObjectGroupPython] G4_CELLULOSE_BUTYRATE  # scripted group (container) (typed FeaturePython)
  Dunit = g/cm3
  Dvalue = 1.2
  Group = -> [H_element022,C_element026,O_element027]
  conduct = 2
  density = 1
  expand = 3
  formula = G4_CELLULOSE_BUTYRATE
  name = G4_CELLULOSE_BUTYRATE
  specific = 4
FEATURE [App::DocumentObjectGroupPython] H_element023  label="H_element : 0.029"  # scripted group (container) (typed FeaturePython)
  n = 0.029216
FEATURE [App::DocumentObjectGroupPython] C_element027  label="C_element : 0.271"  # scripted group (container) (typed FeaturePython)
  n = 0.271296
FEATURE [App::DocumentObjectGroupPython] N_element013  label="N_element : 0.121"  # scripted group (container) (typed FeaturePython)
  n = 0.121276
FEATURE [App::DocumentObjectGroupPython] O_element028  label="O_element : 0.578"  # scripted group (container) (typed FeaturePython)
  n = 0.578212
FEATURE [App::DocumentObjectGroupPython] G4_CELLULOSE_NITRATE  # scripted group (container) (typed FeaturePython)
  Dunit = g/cm3
  Dvalue = 1.49
  Group = -> [H_element023,C_element027,N_element013,O_element028]
  conduct = 2
  density = 1
  expand = 3
  formula = G4_CELLULOSE_NITRATE
  name = G4_CELLULOSE_NITRATE
  specific = 4
FEATURE [App::DocumentObjectGroupPython] H_element024  label="H_element : 0.108"  # scripted group (container) (typed FeaturePython)
  n = 0.107596
FEATURE [App::DocumentObjectGroupPython] N_element014  label="N_element : 0.001"  # scripted group (container) (typed FeaturePython)
  n = 0.0008
FEATURE [App::DocumentObjectGroupPython] O_element029  label="O_element : 0.875"  # scripted group (container) (typed FeaturePython)
  n = 0.874976
FEATURE [App::DocumentObjectGroupPython] S_element008  label="S_element : 0.015"  # scripted group (container) (typed FeaturePython)
  n = 0.014627
FEATURE [App::DocumentObjectGroupPython] Ce_element001  label="Ce_element : 0.002"  # scripted group (container) (typed FeaturePython)
  n = 0.002001
FEATURE [App::DocumentObjectGroupPython] G4_CERIC_SULFATE  # scripted group (container) (typed FeaturePython)
  Dunit = g/cm3
  Dvalue = 1.03
  Group = -> [H_element024,N_element014,O_element029,S_element008,Ce_element001]
  conduct = 2
  density = 1
  expand = 3
  formula = G4_CERIC_SULFATE
  name = G4_CERIC_SULFATE
  specific = 4
FEATURE [App::DocumentObjectGroupPython] Cs_element001  label="Cs_element : 1"  # scripted group (container) (typed FeaturePython)
  n = 1
  ref = Cs_element
FEATURE [App::DocumentObjectGroupPython] F_element006  label="F_element : 1"  # scripted group (container) (typed FeaturePython)
  n = 1
  ref = F_element
FEATURE [App::DocumentObjectGroupPython] G4_CESIUM_FLUORIDE  # scripted group (container) (typed FeaturePython)
  Dunit = g/cm3
  Dvalue = 4.115
  Group = -> [Cs_element001,F_element006]
  conduct = 2
  density = 1
  expand = 3
  formula = G4_CESIUM_FLUORIDE
  name = G4_CESIUM_FLUORIDE
  specific = 4
FEATURE [App::DocumentObjectGroupPython] Cs_element002  label="Cs_element : 002"  # scripted group (container) (typed FeaturePython)
  n = 1
  ref = Cs_element
FEATURE [App::DocumentObjectGroupPython] I_element001  label="I_element : 1"  # scripted group (container) (typed FeaturePython)
  n = 1
  ref = I_element
FEATURE [App::DocumentObjectGroupPython] G4_CESIUM_IODIDE  # scripted group (container) (typed FeaturePython)
  Dunit = g/cm3
  Dvalue = 4.51
  Group = -> [Cs_element002,I_element001]
  conduct = 2
  density = 1
  expand = 3
  formula = G4_CESIUM_IODIDE
  name = G4_CESIUM_IODIDE
  specific = 4
FEATURE [App::DocumentObjectGroupPython] C_element028  label="C_element : 013"  # scripted group (container) (typed FeaturePython)
  n = 6
  ref = C_element
FEATURE [App::DocumentObjectGroupPython] H_element025  label="H_element : 013"  # scripted group (container) (typed FeaturePython)
  n = 5
  ref = H_element
FEATURE [App::DocumentObjectGroupPython] Cl_element005  label="Cl_element : 1"  # scripted group (container) (typed FeaturePython)
  n = 1
  ref = Cl_element
FEATURE [App::DocumentObjectGroupPython] G4_CHLOROBENZENE  # scripted group (container) (typed FeaturePython)
  Dunit = g/cm3
  Dvalue = 1.1058
  Group = -> [C_element028,H_element025,Cl_element005]
  conduct = 2
  density = 1
  expand = 3
  formula = G4_CHLOROBENZENE
  name = G4_CHLOROBENZENE
  specific = 4
FEATURE [App::DocumentObjectGroupPython] C_element029  label="C_element : 014"  # scripted group (container) (typed FeaturePython)
  n = 1
  ref = C_element
FEATURE [App::DocumentObjectGroupPython] H_element026  label="H_element : 1"  # scripted group (container) (typed FeaturePython)
  n = 1
  ref = H_element
FEATURE [App::DocumentObjectGroupPython] Cl_element006  label="Cl_element : 3"  # scripted group (container) (typed FeaturePython)
  n = 3
  ref = Cl_element
FEATURE [App::DocumentObjectGroupPython] G4_CHLOROFORM  # scripted group (container) (typed FeaturePython)
  Dunit = g/cm3
  Dvalue = 1.4832
  Group = -> [C_element029,H_element026,Cl_element006]
  conduct = 2
  density = 1
  expand = 3
  formula = G4_CHLOROFORM
  name = G4_CHLOROFORM
  specific = 4
FEATURE [App::DocumentObjectGroupPython] H_element027  label="H_element : 0.010"  # scripted group (container) (typed FeaturePython)
  n = 0.01
FEATURE [App::DocumentObjectGroupPython] C_element030  label="C_element : 0.001"  # scripted group (container) (typed FeaturePython)
  n = 0.001
FEATURE [App::DocumentObjectGroupPython] O_element030  label="O_element : 0.529"  # scripted group (container) (typed FeaturePython)
  n = 0.529107
FEATURE [App::DocumentObjectGroupPython] Na_element005  label="Na_element : 0.016"  # scripted group (container) (typed FeaturePython)
  n = 0.016
FEATURE [App::DocumentObjectGroupPython] Mg_element003  label="Mg_element : 0.004"  # scripted group (container) (typed FeaturePython)
  n = 0.002
FEATURE [App::DocumentObjectGroupPython] Al_element002  label="Al_element : 0.034"  # scripted group (container) (typed FeaturePython)
  n = 0.033872
FEATURE [App::DocumentObjectGroupPython] Si_element002  label="Si_element : 0.337"  # scripted group (container) (typed FeaturePython)
  n = 0.337021
FEATURE [App::DocumentObjectGroupPython] K_element003  label="K_element : 0.013"  # scripted group (container) (typed FeaturePython)
  n = 0.013
FEATURE [App::DocumentObjectGroupPython] Ca_element010  label="Ca_element : 0.044"  # scripted group (container) (typed FeaturePython)
  n = 0.044
FEATURE [App::DocumentObjectGroupPython] Fe_element002  label="Fe_element : 0.014"  # scripted group (container) (typed FeaturePython)
  n = 0.014
FEATURE [App::DocumentObjectGroupPython] G4_CONCRETE  # scripted group (container) (typed FeaturePython)
  Dunit = g/cm3
  Dvalue = 2.3
  Group = -> [H_element027,C_element030,O_element030,Na_element005,Mg_element003,Al_element002,Si_element002,K_element003,Ca_element010,Fe_element002]
  conduct = 2
  density = 1
  expand = 3
  formula = G4_CONCRETE
  name = G4_CONCRETE
  specific = 4
FEATURE [App::DocumentObjectGroupPython] C_element031  label="C_element : 015"  # scripted group (container) (typed FeaturePython)
  n = 6
  ref = C_element
FEATURE [App::DocumentObjectGroupPython] H_element028  label="H_element : 12"  # scripted group (container) (typed FeaturePython)
  n = 12
  ref = H_element
FEATURE [App::DocumentObjectGroupPython] G4_CYCLOHEXANE  # scripted group (container) (typed FeaturePython)
  Dunit = g/cm3
  Dvalue = 0.779
  Group = -> [C_element031,H_element028]
  conduct = 2
  density = 1
  expand = 3
  formula = G4_CYCLOHEXANE
  name = G4_CYCLOHEXANE
  specific = 4
FEATURE [App::DocumentObjectGroupPython] C_element032  label="C_element : 016"  # scripted group (container) (typed FeaturePython)
  n = 6
  ref = C_element
FEATURE [App::DocumentObjectGroupPython] H_element029  label="H_element : 4"  # scripted group (container) (typed FeaturePython)
  n = 4
  ref = H_element
FEATURE [App::DocumentObjectGroupPython] Cl_element007  label="Cl_element : 2"  # scripted group (container) (typed FeaturePython)
  n = 2
  ref = Cl_element
FEATURE [App::DocumentObjectGroupPython] G4_1_2_DICHLOROBENZENE  label="G4_1.2-DICHLOROBENZENE"  # scripted group (container) (typed FeaturePython)
  Dunit = g/cm3
  Dvalue = 1.3048
  Group = -> [C_element032,H_element029,Cl_element007]
  conduct = 2
  density = 1
  expand = 3
  formula = G4_1.2-DICHLOROBENZENE
  name = G4_1.2-DICHLOROBENZENE
  specific = 4
FEATURE [App::DocumentObjectGroupPython] C_element033  label="C_element : 017"  # scripted group (container) (typed FeaturePython)
  n = 4
  ref = C_element
FEATURE [App::DocumentObjectGroupPython] H_element030  label="H_element : 8"  # scripted group (container) (typed FeaturePython)
  n = 8
  ref = H_element
FEATURE [App::DocumentObjectGroupPython] O_element031  label="O_element : 014"  # scripted group (container) (typed FeaturePython)
  n = 1
  ref = O_element
FEATURE [App::DocumentObjectGroupPython] Cl_element008  label="Cl_element : 005"  # scripted group (container) (typed FeaturePython)
  n = 2
  ref = Cl_element
FEATURE [App::DocumentObjectGroupPython] G4_DICHLORODIETHYL_ETHER  # scripted group (container) (typed FeaturePython)
  Dunit = g/cm3
  Dvalue = 1.2199
  Group = -> [C_element033,H_element030,O_element031,Cl_element008]
  conduct = 2
  density = 1
  expand = 3
  formula = G4_DICHLORODIETHYL_ETHER
  name = G4_DICHLORODIETHYL_ETHER
  specific = 4
FEATURE [App::DocumentObjectGroupPython] C_element034  label="C_element : 018"  # scripted group (container) (typed FeaturePython)
  n = 2
  ref = C_element
FEATURE [App::DocumentObjectGroupPython] H_element031  label="H_element : 014"  # scripted group (container) (typed FeaturePython)
  n = 4
  ref = H_element
FEATURE [App::DocumentObjectGroupPython] Cl_element009  label="Cl_element : 006"  # scripted group (container) (typed FeaturePython)
  n = 2
  ref = Cl_element
FEATURE [App::DocumentObjectGroupPython] G4_1_2_DICHLOROETHANE  label="G4_1.2-DICHLOROETHANE"  # scripted group (container) (typed FeaturePython)
  Dunit = g/cm3
  Dvalue = 1.2351
  Group = -> [C_element034,H_element031,Cl_element009]
  conduct = 2
  density = 1
  expand = 3
  formula = G4_1.2-DICHLOROETHANE
  name = G4_1.2-DICHLOROETHANE
  specific = 4
FEATURE [App::DocumentObjectGroupPython] C_element035  label="C_element : 019"  # scripted group (container) (typed FeaturePython)
  n = 4
  ref = C_element
FEATURE [App::DocumentObjectGroupPython] H_element032  label="H_element : 015"  # scripted group (container) (typed FeaturePython)
  n = 10
  ref = H_element
FEATURE [App::DocumentObjectGroupPython] O_element032  label="O_element : 015"  # scripted group (container) (typed FeaturePython)
  n = 1
  ref = O_element
FEATURE [App::DocumentObjectGroupPython] G4_DIETHYL_ETHER  # scripted group (container) (typed FeaturePython)
  Dunit = g/cm3
  Dvalue = 0.71378
  Group = -> [C_element035,H_element032,O_element032]
  conduct = 2
  density = 1
  expand = 3
  formula = G4_DIETHYL_ETHER
  name = G4_DIETHYL_ETHER
  specific = 4
FEATURE [App::DocumentObjectGroupPython] C_element036  label="C_element : 020"  # scripted group (container) (typed FeaturePython)
  n = 3
  ref = C_element
FEATURE [App::DocumentObjectGroupPython] H_element033  label="H_element : 016"  # scripted group (container) (typed FeaturePython)
  n = 7
  ref = H_element
FEATURE [App::DocumentObjectGroupPython] N_element015  label="N_element : 008"  # scripted group (container) (typed FeaturePython)
  n = 1
  ref = N_element
FEATURE [App::DocumentObjectGroupPython] O_element033  label="O_element : 016"  # scripted group (container) (typed FeaturePython)
  n = 1
  ref = O_element
FEATURE [App::DocumentObjectGroupPython] G4_N_N_DIMETHYL_FORMAMIDE  label="G4_N.N-DIMETHYL_FORMAMIDE"  # scripted group (container) (typed FeaturePython)
  Dunit = g/cm3
  Dvalue = 0.9487
  Group = -> [C_element036,H_element033,N_element015,O_element033]
  conduct = 2
  density = 1
  expand = 3
  formula = G4_N.N-DIMETHYL_FORMAMIDE
  name = G4_N.N-DIMETHYL_FORMAMIDE
  specific = 4
FEATURE [App::DocumentObjectGroupPython] C_element037  label="C_element : 021"  # scripted group (container) (typed FeaturePython)
  n = 2
  ref = C_element
FEATURE [App::DocumentObjectGroupPython] H_element034  label="H_element : 017"  # scripted group (container) (typed FeaturePython)
  n = 6
  ref = H_element
FEATURE [App::DocumentObjectGroupPython] O_element034  label="O_element : 017"  # scripted group (container) (typed FeaturePython)
  n = 1
  ref = O_element
FEATURE [App::DocumentObjectGroupPython] S_element009  label="S_element : 003"  # scripted group (container) (typed FeaturePython)
  n = 1
  ref = S_element
FEATURE [App::DocumentObjectGroupPython] G4_DIMETHYL_SULFOXIDE  # scripted group (container) (typed FeaturePython)
  Dunit = g/cm3
  Dvalue = 1.1014
  Group = -> [C_element037,H_element034,O_element034,S_element009]
  conduct = 2
  density = 1
  expand = 3
  formula = G4_DIMETHYL_SULFOXIDE
  name = G4_DIMETHYL_SULFOXIDE
  specific = 4
FEATURE [App::DocumentObjectGroupPython] C_element038  label="C_element : 022"  # scripted group (container) (typed FeaturePython)
  n = 2
  ref = C_element
FEATURE [App::DocumentObjectGroupPython] H_element035  label="H_element : 018"  # scripted group (container) (typed FeaturePython)
  n = 6
  ref = H_element
FEATURE [App::DocumentObjectGroupPython] G4_ETHANE  # scripted group (container) (typed FeaturePython)
  Dunit = g/cm3
  Dvalue = 0.00125324
  Group = -> [C_element038,H_element035]
  conduct = 2
  density = 1
  expand = 3
  formula = G4_ETHANE
  name = G4_ETHANE
  specific = 4
FEATURE [App::DocumentObjectGroupPython] C_element039  label="C_element : 023"  # scripted group (container) (typed FeaturePython)
  n = 2
  ref = C_element
FEATURE [App::DocumentObjectGroupPython] H_element036  label="H_element : 019"  # scripted group (container) (typed FeaturePython)
  n = 6
  ref = H_element
FEATURE [App::DocumentObjectGroupPython] O_element035  label="O_element : 018"  # scripted group (container) (typed FeaturePython)
  n = 1
  ref = O_element
FEATURE [App::DocumentObjectGroupPython] G4_ETHYL_ALCOHOL  # scripted group (container) (typed FeaturePython)
  Dunit = g/cm3
  Dvalue = 0.7893
  Group = -> [C_element039,H_element036,O_element035]
  conduct = 2
  density = 1
  expand = 3
  formula = G4_ETHYL_ALCOHOL
  name = G4_ETHYL_ALCOHOL
  specific = 4
FEATURE [App::DocumentObjectGroupPython] H_element037  label="H_element : 0.090"  # scripted group (container) (typed FeaturePython)
  n = 0.090027
FEATURE [App::DocumentObjectGroupPython] C_element040  label="C_element : 0.585"  # scripted group (container) (typed FeaturePython)
  n = 0.585182
FEATURE [App::DocumentObjectGroupPython] O_element036  label="O_element : 0.325"  # scripted group (container) (typed FeaturePython)
  n = 0.324791
FEATURE [App::DocumentObjectGroupPython] G4_ETHYL_CELLULOSE  # scripted group (container) (typed FeaturePython)
  Dunit = g/cm3
  Dvalue = 1.13
  Group = -> [H_element037,C_element040,O_element036]
  conduct = 2
  density = 1
  expand = 3
  formula = G4_ETHYL_CELLULOSE
  name = G4_ETHYL_CELLULOSE
  specific = 4
FEATURE [App::DocumentObjectGroupPython] C_element041  label="C_element : 024"  # scripted group (container) (typed FeaturePython)
  n = 2
  ref = C_element
FEATURE [App::DocumentObjectGroupPython] H_element038  label="H_element : 020"  # scripted group (container) (typed FeaturePython)
  n = 4
  ref = H_element
FEATURE [App::DocumentObjectGroupPython] G4_ETHYLENE  # scripted group (container) (typed FeaturePython)
  Dunit = g/cm3
  Dvalue = 0.00117497
  Group = -> [C_element041,H_element038]
  conduct = 2
  density = 1
  expand = 3
  formula = G4_ETHYLENE
  name = G4_ETHYLENE
  specific = 4
FEATURE [App::DocumentObjectGroupPython] H_element039  label="H_element : 0.096"  # scripted group (container) (typed FeaturePython)
  n = 0.096
FEATURE [App::DocumentObjectGroupPython] C_element042  label="C_element : 0.195"  # scripted group (container) (typed FeaturePython)
  n = 0.195
FEATURE [App::DocumentObjectGroupPython] N_element016  label="N_element : 0.057"  # scripted group (container) (typed FeaturePython)
  n = 0.057
FEATURE [App::DocumentObjectGroupPython] O_element037  label="O_element : 0.646"  # scripted group (container) (typed FeaturePython)
  n = 0.646
FEATURE [App::DocumentObjectGroupPython] Na_element006  label="Na_element : 0.017"  # scripted group (container) (typed FeaturePython)
  n = 0.001
FEATURE [App::DocumentObjectGroupPython] P_element005  label="P_element : 0.104"  # scripted group (container) (typed FeaturePython)
  n = 0.001
FEATURE [App::DocumentObjectGroupPython] S_element010  label="S_element : 0.016"  # scripted group (container) (typed FeaturePython)
  n = 0.003
FEATURE [App::DocumentObjectGroupPython] Cl_element010  label="Cl_element : 0.005"  # scripted group (container) (typed FeaturePython)
  n = 0.001
FEATURE [App::DocumentObjectGroupPython] G4_EYE_LENS_ICRP  # scripted group (container) (typed FeaturePython)
  Dunit = g/cm3
  Dvalue = 1.07
  Group = -> [H_element039,C_element042,N_element016,O_element037,Na_element006,P_element005,S_element010,Cl_element010]
  conduct = 2
  density = 1
  expand = 3
  formula = G4_EYE_LENS_ICRP
  name = G4_EYE_LENS_ICRP
  specific = 4
FEATURE [App::DocumentObjectGroupPython] Fe_element003  label="Fe_element : 2"  # scripted group (container) (typed FeaturePython)
  n = 2
  ref = Fe_element
FEATURE [App::DocumentObjectGroupPython] O_element038  label="O_element : 019"  # scripted group (container) (typed FeaturePython)
  n = 3
  ref = O_element
FEATURE [App::DocumentObjectGroupPython] G4_FERRIC_OXIDE  # scripted group (container) (typed FeaturePython)
  Dunit = g/cm3
  Dvalue = 5.2
  Group = -> [Fe_element003,O_element038]
  conduct = 2
  density = 1
  expand = 3
  formula = G4_FERRIC_OXIDE
  name = G4_FERRIC_OXIDE
  specific = 4
FEATURE [App::DocumentObjectGroupPython] Fe_element004  label="Fe_element : 1"  # scripted group (container) (typed FeaturePython)
  n = 1
  ref = Fe_element
FEATURE [App::DocumentObjectGroupPython] B_element003  label="B_element : 1"  # scripted group (container) (typed FeaturePython)
  n = 1
  ref = B_element
FEATURE [App::DocumentObjectGroupPython] G4_FERROBORIDE  # scripted group (container) (typed FeaturePython)
  Dunit = g/cm3
  Dvalue = 7.15
  Group = -> [Fe_element004,B_element003]
  conduct = 2
  density = 1
  expand = 3
  formula = G4_FERROBORIDE
  name = G4_FERROBORIDE
  specific = 4
FEATURE [App::DocumentObjectGroupPython] Fe_element005  label="Fe_element : 003"  # scripted group (container) (typed FeaturePython)
  n = 1
  ref = Fe_element
FEATURE [App::DocumentObjectGroupPython] O_element039  label="O_element : 020"  # scripted group (container) (typed FeaturePython)
  n = 1
  ref = O_element
FEATURE [App::DocumentObjectGroupPython] G4_FERROUS_OXIDE  # scripted group (container) (typed FeaturePython)
  Dunit = g/cm3
  Dvalue = 5.7
  Group = -> [Fe_element005,O_element039]
  conduct = 2
  density = 1
  expand = 3
  formula = G4_FERROUS_OXIDE
  name = G4_FERROUS_OXIDE
  specific = 4
FEATURE [App::DocumentObjectGroupPython] H_element040  label="H_element : 0.115"  # scripted group (container) (typed FeaturePython)
  n = 0.108259
FEATURE [App::DocumentObjectGroupPython] N_element017  label="N_element : 0.000"  # scripted group (container) (typed FeaturePython)
  n = 2.7e-05
FEATURE [App::DocumentObjectGroupPython] O_element040  label="O_element : 0.879"  # scripted group (container) (typed FeaturePython)
  n = 0.878636
FEATURE [App::DocumentObjectGroupPython] Na_element007  label="Na_element : 0.000"  # scripted group (container) (typed FeaturePython)
  n = 2.2e-05
FEATURE [App::DocumentObjectGroupPython] S_element011  label="S_element : 0.013"  # scripted group (container) (typed FeaturePython)
  n = 0.012968
FEATURE [App::DocumentObjectGroupPython] Cl_element011  label="Cl_element : 0.000"  # scripted group (container) (typed FeaturePython)
  n = 3.4e-05
FEATURE [App::DocumentObjectGroupPython] Fe_element006  label="Fe_element : 0.000"  # scripted group (container) (typed FeaturePython)
  n = 5.4e-05
FEATURE [App::DocumentObjectGroupPython] G4_FERROUS_SULFATE  # scripted group (container) (typed FeaturePython)
  Dunit = g/cm3
  Dvalue = 1.024
  Group = -> [H_element040,N_element017,O_element040,Na_element007,S_element011,Cl_element011,Fe_element006]
  conduct = 2
  density = 1
  expand = 3
  formula = G4_FERROUS_SULFATE
  name = G4_FERROUS_SULFATE
  specific = 4
FEATURE [App::DocumentObjectGroupPython] C_element043  label="C_element : 0.099"  # scripted group (container) (typed FeaturePython)
  n = 0.099335
FEATURE [App::DocumentObjectGroupPython] F_element007  label="F_element : 0.314"  # scripted group (container) (typed FeaturePython)
  n = 0.314247
FEATURE [App::DocumentObjectGroupPython] Cl_element012  label="Cl_element : 0.586"  # scripted group (container) (typed FeaturePython)
  n = 0.586418
FEATURE [App::DocumentObjectGroupPython] G4_FREON_12  label="G4_FREON-12"  # scripted group (container) (typed FeaturePython)
  Dunit = g/cm3
  Dvalue = 1.12
  Group = -> [C_element043,F_element007,Cl_element012]
  conduct = 2
  density = 1
  expand = 3
  formula = G4_FREON-12
  name = G4_FREON-12
  specific = 4
FEATURE [App::DocumentObjectGroupPython] C_element044  label="C_element : 0.057"  # scripted group (container) (typed FeaturePython)
  n = 0.057245
FEATURE [App::DocumentObjectGroupPython] F_element008  label="F_element : 0.181"  # scripted group (container) (typed FeaturePython)
  n = 0.181096
FEATURE [App::DocumentObjectGroupPython] Br_element001  label="Br_element : 0.762"  # scripted group (container) (typed FeaturePython)
  n = 0.761659
FEATURE [App::DocumentObjectGroupPython] G4_FREON_12B2  label="G4_FREON-12B2"  # scripted group (container) (typed FeaturePython)
  Dunit = g/cm3
  Dvalue = 1.8
  Group = -> [C_element044,F_element008,Br_element001]
  conduct = 2
  density = 1
  expand = 3
  formula = G4_FREON-12B2
  name = G4_FREON-12B2
  specific = 4
FEATURE [App::DocumentObjectGroupPython] C_element045  label="C_element : 0.115"  # scripted group (container) (typed FeaturePython)
  n = 0.114983
FEATURE [App::DocumentObjectGroupPython] F_element009  label="F_element : 0.546"  # scripted group (container) (typed FeaturePython)
  n = 0.545621
FEATURE [App::DocumentObjectGroupPython] Cl_element013  label="Cl_element : 0.339"  # scripted group (container) (typed FeaturePython)
  n = 0.339396
FEATURE [App::DocumentObjectGroupPython] G4_FREON_13  label="G4_FREON-13"  # scripted group (container) (typed FeaturePython)
  Dunit = g/cm3
  Dvalue = 0.95
  Group = -> [C_element045,F_element009,Cl_element013]
  conduct = 2
  density = 1
  expand = 3
  formula = G4_FREON-13
  name = G4_FREON-13
  specific = 4
FEATURE [App::DocumentObjectGroupPython] C_element046  label="C_element : 025"  # scripted group (container) (typed FeaturePython)
  n = 1
  ref = C_element
FEATURE [App::DocumentObjectGroupPython] F_element010  label="F_element : 3"  # scripted group (container) (typed FeaturePython)
  n = 3
  ref = F_element
FEATURE [App::DocumentObjectGroupPython] Br_element002  label="Br_element : 1"  # scripted group (container) (typed FeaturePython)
  n = 1
  ref = Br_element
FEATURE [App::DocumentObjectGroupPython] G4_FREON_13B1  label="G4_FREON-13B1"  # scripted group (container) (typed FeaturePython)
  Dunit = g/cm3
  Dvalue = 1.5
  Group = -> [C_element046,F_element010,Br_element002]
  conduct = 2
  density = 1
  expand = 3
  formula = G4_FREON-13B1
  name = G4_FREON-13B1
  specific = 4
FEATURE [App::DocumentObjectGroupPython] C_element047  label="C_element : 0.061"  # scripted group (container) (typed FeaturePython)
  n = 0.061309
FEATURE [App::DocumentObjectGroupPython] F_element011  label="F_element : 0.291"  # scripted group (container) (typed FeaturePython)
  n = 0.290924
FEATURE [App::DocumentObjectGroupPython] I_element002  label="I_element : 0.648"  # scripted group (container) (typed FeaturePython)
  n = 0.647767
FEATURE [App::DocumentObjectGroupPython] G4_FREON_13I1  label="G4_FREON-13I1"  # scripted group (container) (typed FeaturePython)
  Dunit = g/cm3
  Dvalue = 1.8
  Group = -> [C_element047,F_element011,I_element002]
  conduct = 2
  density = 1
  expand = 3
  formula = G4_FREON-13I1
  name = G4_FREON-13I1
  specific = 4
FEATURE [App::DocumentObjectGroupPython] Gd_element001  label="Gd_element : 2"  # scripted group (container) (typed FeaturePython)
  n = 2
  ref = Gd_element
FEATURE [App::DocumentObjectGroupPython] O_element041  label="O_element : 021"  # scripted group (container) (typed FeaturePython)
  n = 2
  ref = O_element
FEATURE [App::DocumentObjectGroupPython] S_element012  label="S_element : 004"  # scripted group (container) (typed FeaturePython)
  n = 1
  ref = S_element
FEATURE [App::DocumentObjectGroupPython] G4_GADOLINIUM_OXYSULFIDE  # scripted group (container) (typed FeaturePython)
  Dunit = g/cm3
  Dvalue = 7.44
  Group = -> [Gd_element001,O_element041,S_element012]
  conduct = 2
  density = 1
  expand = 3
  formula = G4_GADOLINIUM_OXYSULFIDE
  name = G4_GADOLINIUM_OXYSULFIDE
  specific = 4
FEATURE [App::DocumentObjectGroupPython] Ga_element001  label="Ga_element : 1"  # scripted group (container) (typed FeaturePython)
  n = 1
  ref = Ga_element
FEATURE [App::DocumentObjectGroupPython] As_element001  label="As_element : 1"  # scripted group (container) (typed FeaturePython)
  n = 1
  ref = As_element
FEATURE [App::DocumentObjectGroupPython] G4_GALLIUM_ARSENIDE  # scripted group (container) (typed FeaturePython)
  Dunit = g/cm3
  Dvalue = 5.31
  Group = -> [Ga_element001,As_element001]
  conduct = 2
  density = 1
  expand = 3
  formula = G4_GALLIUM_ARSENIDE
  name = G4_GALLIUM_ARSENIDE
  specific = 4
FEATURE [App::DocumentObjectGroupPython] H_element041  label="H_element : 0.081"  # scripted group (container) (typed FeaturePython)
  n = 0.08118
FEATURE [App::DocumentObjectGroupPython] C_element048  label="C_element : 0.416"  # scripted group (container) (typed FeaturePython)
  n = 0.41606
FEATURE [App::DocumentObjectGroupPython] N_element018  label="N_element : 0.111"  # scripted group (container) (typed FeaturePython)
  n = 0.11124
FEATURE [App::DocumentObjectGroupPython] O_element042  label="O_element : 0.381"  # scripted group (container) (typed FeaturePython)
  n = 0.38064
FEATURE [App::DocumentObjectGroupPython] S_element013  label="S_element : 0.011"  # scripted group (container) (typed FeaturePython)
  n = 0.01088
FEATURE [App::DocumentObjectGroupPython] G4_GEL_PHOTO_EMULSION  # scripted group (container) (typed FeaturePython)
  Dunit = g/cm3
  Dvalue = 1.2914
  Group = -> [H_element041,C_element048,N_element018,O_element042,S_element013]
  conduct = 2
  density = 1
  expand = 3
  formula = G4_GEL_PHOTO_EMULSION
  name = G4_GEL_PHOTO_EMULSION
  specific = 4
FEATURE [App::DocumentObjectGroupPython] B_element004  label="B_element : 0.040"  # scripted group (container) (typed FeaturePython)
  n = 0.0400639
FEATURE [App::DocumentObjectGroupPython] O_element043  label="O_element : 0.540"  # scripted group (container) (typed FeaturePython)
  n = 0.539561
FEATURE [App::DocumentObjectGroupPython] Na_element008  label="Na_element : 0.028"  # scripted group (container) (typed FeaturePython)
  n = 0.0281909
FEATURE [App::DocumentObjectGroupPython] Al_element003  label="Al_element : 0.012"  # scripted group (container) (typed FeaturePython)
  n = 0.011644
FEATURE [App::DocumentObjectGroupPython] Si_element003  label="Si_element : 0.377"  # scripted group (container) (typed FeaturePython)
  n = 0.377219
FEATURE [App::DocumentObjectGroupPython] K_element004  label="K_element : 0.014"  # scripted group (container) (typed FeaturePython)
  n = 0.00332099
FEATURE [App::DocumentObjectGroupPython] G4_Pyrex_Glass  # scripted group (container) (typed FeaturePython)
  Dunit = g/cm3
  Dvalue = 2.23
  Group = -> [B_element004,O_element043,Na_element008,Al_element003,Si_element003,K_element004]
  conduct = 2
  density = 1
  expand = 3
  formula = G4_Pyrex_Glass
  name = G4_Pyrex_Glass
  specific = 4
FEATURE [App::DocumentObjectGroupPython] O_element044  label="O_element : 0.156"  # scripted group (container) (typed FeaturePython)
  n = 0.156453
FEATURE [App::DocumentObjectGroupPython] Si_element004  label="Si_element : 0.081"  # scripted group (container) (typed FeaturePython)
  n = 0.080866
FEATURE [App::DocumentObjectGroupPython] Ti_element001  label="Ti_element : 0.008"  # scripted group (container) (typed FeaturePython)
  n = 0.008092
FEATURE [App::DocumentObjectGroupPython] As_element002  label="As_element : 0.003"  # scripted group (container) (typed FeaturePython)
  n = 0.002651
FEATURE [App::DocumentObjectGroupPython] Pb_element001  label="Pb_element : 0.752"  # scripted group (container) (typed FeaturePython)
  n = 0.751938
FEATURE [App::DocumentObjectGroupPython] G4_GLASS_LEAD  # scripted group (container) (typed FeaturePython)
  Dunit = g/cm3
  Dvalue = 6.22
  Group = -> [O_element044,Si_element004,Ti_element001,As_element002,Pb_element001]
  conduct = 2
  density = 1
  expand = 3
  formula = G4_GLASS_LEAD
  name = G4_GLASS_LEAD
  specific = 4
FEATURE [App::DocumentObjectGroupPython] O_element045  label="O_element : 0.460"  # scripted group (container) (typed FeaturePython)
  n = 0.4598
FEATURE [App::DocumentObjectGroupPython] Na_element009  label="Na_element : 0.096"  # scripted group (container) (typed FeaturePython)
  n = 0.0964411
FEATURE [App::DocumentObjectGroupPython] Si_element005  label="Si_element : 0.378"  # scripted group (container) (typed FeaturePython)
  n = 0.336553
FEATURE [App::DocumentObjectGroupPython] Ca_element011  label="Ca_element : 0.107"  # scripted group (container) (typed FeaturePython)
  n = 0.107205
FEATURE [App::DocumentObjectGroupPython] G4_GLASS_PLATE  # scripted group (container) (typed FeaturePython)
  Dunit = g/cm3
  Dvalue = 2.4
  Group = -> [O_element045,Na_element009,Si_element005,Ca_element011]
  conduct = 2
  density = 1
  expand = 3
  formula = G4_GLASS_PLATE
  name = G4_GLASS_PLATE
  specific = 4
FEATURE [App::DocumentObjectGroupPython] C_element049  label="C_element : 026"  # scripted group (container) (typed FeaturePython)
  n = 5
  ref = C_element
FEATURE [App::DocumentObjectGroupPython] H_element042  label="H_element : 021"  # scripted group (container) (typed FeaturePython)
  n = 10
  ref = H_element
FEATURE [App::DocumentObjectGroupPython] N_element019  label="N_element : 2"  # scripted group (container) (typed FeaturePython)
  n = 2
  ref = N_element
FEATURE [App::DocumentObjectGroupPython] O_element046  label="O_element : 022"  # scripted group (container) (typed FeaturePython)
  n = 3
  ref = O_element
FEATURE [App::DocumentObjectGroupPython] G4_GLUTAMINE  # scripted group (container) (typed FeaturePython)
  Dunit = g/cm3
  Dvalue = 1.46
  Group = -> [C_element049,H_element042,N_element019,O_element046]
  conduct = 2
  density = 1
  expand = 3
  formula = G4_GLUTAMINE
  name = G4_GLUTAMINE
  specific = 4
FEATURE [App::DocumentObjectGroupPython] C_element050  label="C_element : 027"  # scripted group (container) (typed FeaturePython)
  n = 3
  ref = C_element
FEATURE [App::DocumentObjectGroupPython] H_element043  label="H_element : 022"  # scripted group (container) (typed FeaturePython)
  n = 8
  ref = H_element
FEATURE [App::DocumentObjectGroupPython] O_element047  label="O_element : 023"  # scripted group (container) (typed FeaturePython)
  n = 3
  ref = O_element
FEATURE [App::DocumentObjectGroupPython] G4_GLYCEROL  # scripted group (container) (typed FeaturePython)
  Dunit = g/cm3
  Dvalue = 1.2613
  Group = -> [C_element050,H_element043,O_element047]
  conduct = 2
  density = 1
  expand = 3
  formula = G4_GLYCEROL
  name = G4_GLYCEROL
  specific = 4
FEATURE [App::DocumentObjectGroupPython] C_element051  label="C_element : 028"  # scripted group (container) (typed FeaturePython)
  n = 5
  ref = C_element
FEATURE [App::DocumentObjectGroupPython] H_element044  label="H_element : 023"  # scripted group (container) (typed FeaturePython)
  n = 5
  ref = H_element
FEATURE [App::DocumentObjectGroupPython] N_element020  label="N_element : 009"  # scripted group (container) (typed FeaturePython)
  n = 5
  ref = N_element
FEATURE [App::DocumentObjectGroupPython] O_element048  label="O_element : 024"  # scripted group (container) (typed FeaturePython)
  n = 1
  ref = O_element
FEATURE [App::DocumentObjectGroupPython] G4_GUANINE  # scripted group (container) (typed FeaturePython)
  Dunit = g/cm3
  Dvalue = 2.2
  Group = -> [C_element051,H_element044,N_element020,O_element048]
  conduct = 2
  density = 1
  expand = 3
  formula = G4_GUANINE
  name = G4_GUANINE
  specific = 4
FEATURE [App::DocumentObjectGroupPython] Ca_element012  label="Ca_element : 006"  # scripted group (container) (typed FeaturePython)
  n = 1
  ref = Ca_element
FEATURE [App::DocumentObjectGroupPython] S_element014  label="S_element : 005"  # scripted group (container) (typed FeaturePython)
  n = 1
  ref = S_element
FEATURE [App::DocumentObjectGroupPython] O_element049  label="O_element : 6"  # scripted group (container) (typed FeaturePython)
  n = 6
  ref = O_element
FEATURE [App::DocumentObjectGroupPython] H_element045  label="H_element : 024"  # scripted group (container) (typed FeaturePython)
  n = 4
  ref = H_element
FEATURE [App::DocumentObjectGroupPython] G4_GYPSUM  # scripted group (container) (typed FeaturePython)
  Dunit = g/cm3
  Dvalue = 2.32
  Group = -> [Ca_element012,S_element014,O_element049,H_element045]
  conduct = 2
  density = 1
  expand = 3
  formula = G4_GYPSUM
  name = G4_GYPSUM
  specific = 4
FEATURE [App::DocumentObjectGroupPython] C_element052  label="C_element : 7"  # scripted group (container) (typed FeaturePython)
  n = 7
  ref = C_element
FEATURE [App::DocumentObjectGroupPython] H_element046  label="H_element : 16"  # scripted group (container) (typed FeaturePython)
  n = 16
  ref = H_element
FEATURE [App::DocumentObjectGroupPython] G4_N_HEPTANE  label="G4_N-HEPTANE"  # scripted group (container) (typed FeaturePython)
  Dunit = g/cm3
  Dvalue = 0.68376
  Group = -> [C_element052,H_element046]
  conduct = 2
  density = 1
  expand = 3
  formula = G4_N-HEPTANE
  name = G4_N-HEPTANE
  specific = 4
FEATURE [App::DocumentObjectGroupPython] C_element053  label="C_element : 029"  # scripted group (container) (typed FeaturePython)
  n = 6
  ref = C_element
FEATURE [App::DocumentObjectGroupPython] H_element047  label="H_element : 14"  # scripted group (container) (typed FeaturePython)
  n = 14
  ref = H_element
FEATURE [App::DocumentObjectGroupPython] G4_N_HEXANE  label="G4_N-HEXANE"  # scripted group (container) (typed FeaturePython)
  Dunit = g/cm3
  Dvalue = 0.6603
  Group = -> [C_element053,H_element047]
  conduct = 2
  density = 1
  expand = 3
  formula = G4_N-HEXANE
  name = G4_N-HEXANE
  specific = 4
FEATURE [App::DocumentObjectGroupPython] C_element054  label="C_element : 22"  # scripted group (container) (typed FeaturePython)
  n = 22
  ref = C_element
FEATURE [App::DocumentObjectGroupPython] H_element048  label="H_element : 025"  # scripted group (container) (typed FeaturePython)
  n = 10
  ref = H_element
FEATURE [App::DocumentObjectGroupPython] N_element021  label="N_element : 010"  # scripted group (container) (typed FeaturePython)
  n = 2
  ref = N_element
FEATURE [App::DocumentObjectGroupPython] O_element050  label="O_element : 025"  # scripted group (container) (typed FeaturePython)
  n = 5
  ref = O_element
FEATURE [App::DocumentObjectGroupPython] G4_KAPTON  # scripted group (container) (typed FeaturePython)
  Dunit = g/cm3
  Dvalue = 1.42
  Group = -> [C_element054,H_element048,N_element021,O_element050]
  conduct = 2
  density = 1
  expand = 3
  formula = G4_KAPTON
  name = G4_KAPTON
  specific = 4
FEATURE [App::DocumentObjectGroupPython] La_element001  label="La_element : 1"  # scripted group (container) (typed FeaturePython)
  n = 1
  ref = La_element
FEATURE [App::DocumentObjectGroupPython] Br_element003  label="Br_element : 002"  # scripted group (container) (typed FeaturePython)
  n = 1
  ref = Br_element
FEATURE [App::DocumentObjectGroupPython] O_element051  label="O_element : 026"  # scripted group (container) (typed FeaturePython)
  n = 1
  ref = O_element
FEATURE [App::DocumentObjectGroupPython] G4_LANTHANUM_OXYBROMIDE  # scripted group (container) (typed FeaturePython)
  Dunit = g/cm3
  Dvalue = 6.28
  Group = -> [La_element001,Br_element003,O_element051]
  conduct = 2
  density = 1
  expand = 3
  formula = G4_LANTHANUM_OXYBROMIDE
  name = G4_LANTHANUM_OXYBROMIDE
  specific = 4
FEATURE [App::DocumentObjectGroupPython] La_element002  label="La_element : 2"  # scripted group (container) (typed FeaturePython)
  n = 2
  ref = La_element
FEATURE [App::DocumentObjectGroupPython] O_element052  label="O_element : 027"  # scripted group (container) (typed FeaturePython)
  n = 2
  ref = O_element
FEATURE [App::DocumentObjectGroupPython] S_element015  label="S_element : 006"  # scripted group (container) (typed FeaturePython)
  n = 1
  ref = S_element
FEATURE [App::DocumentObjectGroupPython] G4_LANTHANUM_OXYSULFIDE  # scripted group (container) (typed FeaturePython)
  Dunit = g/cm3
  Dvalue = 5.86
  Group = -> [La_element002,O_element052,S_element015]
  conduct = 2
  density = 1
  expand = 3
  formula = G4_LANTHANUM_OXYSULFIDE
  name = G4_LANTHANUM_OXYSULFIDE
  specific = 4
FEATURE [App::DocumentObjectGroupPython] O_element053  label="O_element : 0.072"  # scripted group (container) (typed FeaturePython)
  n = 0.071682
FEATURE [App::DocumentObjectGroupPython] Pb_element002  label="Pb_element : 0.928"  # scripted group (container) (typed FeaturePython)
  n = 0.928318
FEATURE [App::DocumentObjectGroupPython] G4_LEAD_OXIDE  # scripted group (container) (typed FeaturePython)
  Dunit = g/cm3
  Dvalue = 9.53
  Group = -> [O_element053,Pb_element002]
  conduct = 2
  density = 1
  expand = 3
  formula = G4_LEAD_OXIDE
  name = G4_LEAD_OXIDE
  specific = 4
FEATURE [App::DocumentObjectGroupPython] Li_element001  label="Li_element : 1"  # scripted group (container) (typed FeaturePython)
  n = 1
  ref = Li_element
FEATURE [App::DocumentObjectGroupPython] N_element022  label="N_element : 011"  # scripted group (container) (typed FeaturePython)
  n = 1
  ref = N_element
FEATURE [App::DocumentObjectGroupPython] H_element049  label="H_element : 026"  # scripted group (container) (typed FeaturePython)
  n = 2
  ref = H_element
FEATURE [App::DocumentObjectGroupPython] G4_LITHIUM_AMIDE  # scripted group (container) (typed FeaturePython)
  Dunit = g/cm3
  Dvalue = 1.178
  Group = -> [Li_element001,N_element022,H_element049]
  conduct = 2
  density = 1
  expand = 3
  formula = G4_LITHIUM_AMIDE
  name = G4_LITHIUM_AMIDE
  specific = 4
FEATURE [App::DocumentObjectGroupPython] Li_element002  label="Li_element : 2"  # scripted group (container) (typed FeaturePython)
  n = 2
  ref = Li_element
FEATURE [App::DocumentObjectGroupPython] C_element055  label="C_element : 030"  # scripted group (container) (typed FeaturePython)
  n = 1
  ref = C_element
FEATURE [App::DocumentObjectGroupPython] O_element054  label="O_element : 028"  # scripted group (container) (typed FeaturePython)
  n = 3
  ref = O_element
FEATURE [App::DocumentObjectGroupPython] G4_LITHIUM_CARBONATE  # scripted group (container) (typed FeaturePython)
  Dunit = g/cm3
  Dvalue = 2.11
  Group = -> [Li_element002,C_element055,O_element054]
  conduct = 2
  density = 1
  expand = 3
  formula = G4_LITHIUM_CARBONATE
  name = G4_LITHIUM_CARBONATE
  specific = 4
FEATURE [App::DocumentObjectGroupPython] Li_element003  label="Li_element : 003"  # scripted group (container) (typed FeaturePython)
  n = 1
  ref = Li_element
FEATURE [App::DocumentObjectGroupPython] F_element012  label="F_element : 004"  # scripted group (container) (typed FeaturePython)
  n = 1
  ref = F_element
FEATURE [App::DocumentObjectGroupPython] G4_LITHIUM_FLUORIDE  # scripted group (container) (typed FeaturePython)
  Dunit = g/cm3
  Dvalue = 2.635
  Group = -> [Li_element003,F_element012]
  conduct = 2
  density = 1
  expand = 3
  formula = G4_LITHIUM_FLUORIDE
  name = G4_LITHIUM_FLUORIDE
  specific = 4
FEATURE [App::DocumentObjectGroupPython] Li_element004  label="Li_element : 004"  # scripted group (container) (typed FeaturePython)
  n = 1
  ref = Li_element
FEATURE [App::DocumentObjectGroupPython] H_element050  label="H_element : 027"  # scripted group (container) (typed FeaturePython)
  n = 1
  ref = H_element
FEATURE [App::DocumentObjectGroupPython] G4_LITHIUM_HYDRIDE  # scripted group (container) (typed FeaturePython)
  Dunit = g/cm3
  Dvalue = 0.82
  Group = -> [Li_element004,H_element050]
  conduct = 2
  density = 1
  expand = 3
  formula = G4_LITHIUM_HYDRIDE
  name = G4_LITHIUM_HYDRIDE
  specific = 4
FEATURE [App::DocumentObjectGroupPython] Li_element005  label="Li_element : 005"  # scripted group (container) (typed FeaturePython)
  n = 1
  ref = Li_element
FEATURE [App::DocumentObjectGroupPython] I_element003  label="I_element : 002"  # scripted group (container) (typed FeaturePython)
  n = 1
  ref = I_element
FEATURE [App::DocumentObjectGroupPython] G4_LITHIUM_IODIDE  # scripted group (container) (typed FeaturePython)
  Dunit = g/cm3
  Dvalue = 3.494
  Group = -> [Li_element005,I_element003]
  conduct = 2
  density = 1
  expand = 3
  formula = G4_LITHIUM_IODIDE
  name = G4_LITHIUM_IODIDE
  specific = 4
FEATURE [App::DocumentObjectGroupPython] Li_element006  label="Li_element : 006"  # scripted group (container) (typed FeaturePython)
  n = 2
  ref = Li_element
FEATURE [App::DocumentObjectGroupPython] O_element055  label="O_element : 029"  # scripted group (container) (typed FeaturePython)
  n = 1
  ref = O_element
FEATURE [App::DocumentObjectGroupPython] G4_LITHIUM_OXIDE  # scripted group (container) (typed FeaturePython)
  Dunit = g/cm3
  Dvalue = 2.013
  Group = -> [Li_element006,O_element055]
  conduct = 2
  density = 1
  expand = 3
  formula = G4_LITHIUM_OXIDE
  name = G4_LITHIUM_OXIDE
  specific = 4
FEATURE [App::DocumentObjectGroupPython] Li_element007  label="Li_element : 007"  # scripted group (container) (typed FeaturePython)
  n = 2
  ref = Li_element
FEATURE [App::DocumentObjectGroupPython] B_element005  label="B_element : 005"  # scripted group (container) (typed FeaturePython)
  n = 4
  ref = B_element
FEATURE [App::DocumentObjectGroupPython] O_element056  label="O_element : 7"  # scripted group (container) (typed FeaturePython)
  n = 7
  ref = O_element
FEATURE [App::DocumentObjectGroupPython] G4_LITHIUM_TETRABORATE  # scripted group (container) (typed FeaturePython)
  Dunit = g/cm3
  Dvalue = 2.44
  Group = -> [Li_element007,B_element005,O_element056]
  conduct = 2
  density = 1
  expand = 3
  formula = G4_LITHIUM_TETRABORATE
  name = G4_LITHIUM_TETRABORATE
  specific = 4
FEATURE [App::DocumentObjectGroupPython] H_element051  label="H_element : 0.105"  # scripted group (container) (typed FeaturePython)
  n = 0.105
FEATURE [App::DocumentObjectGroupPython] C_element056  label="C_element : 0.083"  # scripted group (container) (typed FeaturePython)
  n = 0.083
FEATURE [App::DocumentObjectGroupPython] N_element023  label="N_element : 0.023"  # scripted group (container) (typed FeaturePython)
  n = 0.023
FEATURE [App::DocumentObjectGroupPython] O_element057  label="O_element : 0.779"  # scripted group (container) (typed FeaturePython)
  n = 0.779
FEATURE [App::DocumentObjectGroupPython] Na_element010  label="Na_element : 0.097"  # scripted group (container) (typed FeaturePython)
  n = 0.002
FEATURE [App::DocumentObjectGroupPython] P_element006  label="P_element : 0.105"  # scripted group (container) (typed FeaturePython)
  n = 0.001
FEATURE [App::DocumentObjectGroupPython] S_element016  label="S_element : 0.017"  # scripted group (container) (typed FeaturePython)
  n = 0.002
FEATURE [App::DocumentObjectGroupPython] Cl_element014  label="Cl_element : 0.587"  # scripted group (container) (typed FeaturePython)
  n = 0.003
FEATURE [App::DocumentObjectGroupPython] K_element005  label="K_element : 0.015"  # scripted group (container) (typed FeaturePython)
  n = 0.002
FEATURE [App::DocumentObjectGroupPython] G4_LUNG_ICRP  # scripted group (container) (typed FeaturePython)
  Dunit = g/cm3
  Dvalue = 1.04
  Group = -> [H_element051,C_element056,N_element023,O_element057,Na_element010,P_element006,S_element016,Cl_element014,K_element005]
  conduct = 2
  density = 1
  expand = 3
  formula = G4_LUNG_ICRP
  name = G4_LUNG_ICRP
  specific = 4
FEATURE [App::DocumentObjectGroupPython] H_element052  label="H_element : 0.116"  # scripted group (container) (typed FeaturePython)
  n = 0.114318
FEATURE [App::DocumentObjectGroupPython] C_element057  label="C_element : 0.656"  # scripted group (container) (typed FeaturePython)
  n = 0.655824
FEATURE [App::DocumentObjectGroupPython] O_element058  label="O_element : 0.092"  # scripted group (container) (typed FeaturePython)
  n = 0.0921831
FEATURE [App::DocumentObjectGroupPython] Mg_element004  label="Mg_element : 0.135"  # scripted group (container) (typed FeaturePython)
  n = 0.134792
FEATURE [App::DocumentObjectGroupPython] Ca_element013  label="Ca_element : 0.003"  # scripted group (container) (typed FeaturePython)
  n = 0.002883
FEATURE [App::DocumentObjectGroupPython] G4_M3_WAX  # scripted group (container) (typed FeaturePython)
  Dunit = g/cm3
  Dvalue = 1.05
  Group = -> [H_element052,C_element057,O_element058,Mg_element004,Ca_element013]
  conduct = 2
  density = 1
  expand = 3
  formula = G4_M3_WAX
  name = G4_M3_WAX
  specific = 4
FEATURE [App::DocumentObjectGroupPython] Mg_element005  label="Mg_element : 1"  # scripted group (container) (typed FeaturePython)
  n = 1
  ref = Mg_element
FEATURE [App::DocumentObjectGroupPython] C_element058  label="C_element : 031"  # scripted group (container) (typed FeaturePython)
  n = 1
  ref = C_element
FEATURE [App::DocumentObjectGroupPython] O_element059  label="O_element : 030"  # scripted group (container) (typed FeaturePython)
  n = 3
  ref = O_element
FEATURE [App::DocumentObjectGroupPython] G4_MAGNESIUM_CARBONATE  # scripted group (container) (typed FeaturePython)
  Dunit = g/cm3
  Dvalue = 2.958
  Group = -> [Mg_element005,C_element058,O_element059]
  conduct = 2
  density = 1
  expand = 3
  formula = G4_MAGNESIUM_CARBONATE
  name = G4_MAGNESIUM_CARBONATE
  specific = 4
FEATURE [App::DocumentObjectGroupPython] Mg_element006  label="Mg_element : 002"  # scripted group (container) (typed FeaturePython)
  n = 1
  ref = Mg_element
FEATURE [App::DocumentObjectGroupPython] F_element013  label="F_element : 005"  # scripted group (container) (typed FeaturePython)
  n = 2
  ref = F_element
FEATURE [App::DocumentObjectGroupPython] G4_MAGNESIUM_FLUORIDE  # scripted group (container) (typed FeaturePython)
  Dunit = g/cm3
  Dvalue = 3
  Group = -> [Mg_element006,F_element013]
  conduct = 2
  density = 1
  expand = 3
  formula = G4_MAGNESIUM_FLUORIDE
  name = G4_MAGNESIUM_FLUORIDE
  specific = 4
FEATURE [App::DocumentObjectGroupPython] Mg_element007  label="Mg_element : 003"  # scripted group (container) (typed FeaturePython)
  n = 1
  ref = Mg_element
FEATURE [App::DocumentObjectGroupPython] O_element060  label="O_element : 031"  # scripted group (container) (typed FeaturePython)
  n = 1
  ref = O_element
FEATURE [App::DocumentObjectGroupPython] G4_MAGNESIUM_OXIDE  # scripted group (container) (typed FeaturePython)
  Dunit = g/cm3
  Dvalue = 3.58
  Group = -> [Mg_element007,O_element060]
  conduct = 2
  density = 1
  expand = 3
  formula = G4_MAGNESIUM_OXIDE
  name = G4_MAGNESIUM_OXIDE
  specific = 4
FEATURE [App::DocumentObjectGroupPython] Mg_element008  label="Mg_element : 004"  # scripted group (container) (typed FeaturePython)
  n = 1
  ref = Mg_element
FEATURE [App::DocumentObjectGroupPython] B_element006  label="B_element : 006"  # scripted group (container) (typed FeaturePython)
  n = 4
  ref = B_element
FEATURE [App::DocumentObjectGroupPython] O_element061  label="O_element : 032"  # scripted group (container) (typed FeaturePython)
  n = 7
  ref = O_element
FEATURE [App::DocumentObjectGroupPython] G4_MAGNESIUM_TETRABORATE  # scripted group (container) (typed FeaturePython)
  Dunit = g/cm3
  Dvalue = 2.53
  Group = -> [Mg_element008,B_element006,O_element061]
  conduct = 2
  density = 1
  expand = 3
  formula = G4_MAGNESIUM_TETRABORATE
  name = G4_MAGNESIUM_TETRABORATE
  specific = 4
FEATURE [App::DocumentObjectGroupPython] Hg_element001  label="Hg_element : 1"  # scripted group (container) (typed FeaturePython)
  n = 1
  ref = Hg_element
FEATURE [App::DocumentObjectGroupPython] I_element004  label="I_element : 2"  # scripted group (container) (typed FeaturePython)
  n = 2
  ref = I_element
FEATURE [App::DocumentObjectGroupPython] G4_MERCURIC_IODIDE  # scripted group (container) (typed FeaturePython)
  Dunit = g/cm3
  Dvalue = 6.36
  Group = -> [Hg_element001,I_element004]
  conduct = 2
  density = 1
  expand = 3
  formula = G4_MERCURIC_IODIDE
  name = G4_MERCURIC_IODIDE
  specific = 4
FEATURE [App::DocumentObjectGroupPython] C_element059  label="C_element : 032"  # scripted group (container) (typed FeaturePython)
  n = 1
  ref = C_element
FEATURE [App::DocumentObjectGroupPython] H_element053  label="H_element : 028"  # scripted group (container) (typed FeaturePython)
  n = 4
  ref = H_element
FEATURE [App::DocumentObjectGroupPython] G4_METHANE  # scripted group (container) (typed FeaturePython)
  Dunit = g/cm3
  Dvalue = 0.000667151
  Group = -> [C_element059,H_element053]
  conduct = 2
  density = 1
  expand = 3
  formula = G4_METHANE
  name = G4_METHANE
  specific = 4
FEATURE [App::DocumentObjectGroupPython] C_element060  label="C_element : 033"  # scripted group (container) (typed FeaturePython)
  n = 1
  ref = C_element
FEATURE [App::DocumentObjectGroupPython] H_element054  label="H_element : 029"  # scripted group (container) (typed FeaturePython)
  n = 4
  ref = H_element
FEATURE [App::DocumentObjectGroupPython] O_element062  label="O_element : 033"  # scripted group (container) (typed FeaturePython)
  n = 1
  ref = O_element
FEATURE [App::DocumentObjectGroupPython] G4_METHANOL  # scripted group (container) (typed FeaturePython)
  Dunit = g/cm3
  Dvalue = 0.7914
  Group = -> [C_element060,H_element054,O_element062]
  conduct = 2
  density = 1
  expand = 3
  formula = G4_METHANOL
  name = G4_METHANOL
  specific = 4
FEATURE [App::DocumentObjectGroupPython] H_element055  label="H_element : 0.134"  # scripted group (container) (typed FeaturePython)
  n = 0.13404
FEATURE [App::DocumentObjectGroupPython] C_element061  label="C_element : 0.778"  # scripted group (container) (typed FeaturePython)
  n = 0.77796
FEATURE [App::DocumentObjectGroupPython] O_element063  label="O_element : 0.035"  # scripted group (container) (typed FeaturePython)
  n = 0.03502
FEATURE [App::DocumentObjectGroupPython] Mg_element009  label="Mg_element : 0.039"  # scripted group (container) (typed FeaturePython)
  n = 0.038594
FEATURE [App::DocumentObjectGroupPython] Ti_element002  label="Ti_element : 0.014"  # scripted group (container) (typed FeaturePython)
  n = 0.014386
FEATURE [App::DocumentObjectGroupPython] G4_MIX_D_WAX  # scripted group (container) (typed FeaturePython)
  Dunit = g/cm3
  Dvalue = 0.99
  Group = -> [H_element055,C_element061,O_element063,Mg_element009,Ti_element002]
  conduct = 2
  density = 1
  expand = 3
  formula = G4_MIX_D_WAX
  name = G4_MIX_D_WAX
  specific = 4
FEATURE [App::DocumentObjectGroupPython] H_element056  label="H_element : 0.135"  # scripted group (container) (typed FeaturePython)
  n = 0.081192
FEATURE [App::DocumentObjectGroupPython] C_element062  label="C_element : 0.583"  # scripted group (container) (typed FeaturePython)
  n = 0.583442
FEATURE [App::DocumentObjectGroupPython] N_element024  label="N_element : 0.018"  # scripted group (container) (typed FeaturePython)
  n = 0.017798
FEATURE [App::DocumentObjectGroupPython] O_element064  label="O_element : 0.186"  # scripted group (container) (typed FeaturePython)
  n = 0.186381
FEATURE [App::DocumentObjectGroupPython] Mg_element010  label="Mg_element : 0.130"  # scripted group (container) (typed FeaturePython)
  n = 0.130287
FEATURE [App::DocumentObjectGroupPython] Cl_element015  label="Cl_element : 0.588"  # scripted group (container) (typed FeaturePython)
  n = 0.0009
FEATURE [App::DocumentObjectGroupPython] G4_MS20_TISSUE  # scripted group (container) (typed FeaturePython)
  Dunit = g/cm3
  Dvalue = 1
  Group = -> [H_element056,C_element062,N_element024,O_element064,Mg_element010,Cl_element015]
  conduct = 2
  density = 1
  expand = 3
  formula = G4_MS20_TISSUE
  name = G4_MS20_TISSUE
  specific = 4
FEATURE [App::DocumentObjectGroupPython] H_element057  label="H_element : 0.136"  # scripted group (container) (typed FeaturePython)
  n = 0.102
FEATURE [App::DocumentObjectGroupPython] C_element063  label="C_element : 0.143"  # scripted group (container) (typed FeaturePython)
  n = 0.143
FEATURE [App::DocumentObjectGroupPython] N_element025  label="N_element : 0.034"  # scripted group (container) (typed FeaturePython)
  n = 0.034
FEATURE [App::DocumentObjectGroupPython] O_element065  label="O_element : 0.710"  # scripted group (container) (typed FeaturePython)
  n = 0.71
FEATURE [App::DocumentObjectGroupPython] Na_element011  label="Na_element : 0.098"  # scripted group (container) (typed FeaturePython)
  n = 0.001
FEATURE [App::DocumentObjectGroupPython] P_element007  label="P_element : 0.002"  # scripted group (container) (typed FeaturePython)
  n = 0.002
FEATURE [App::DocumentObjectGroupPython] S_element017  label="S_element : 0.018"  # scripted group (container) (typed FeaturePython)
  n = 0.003
FEATURE [App::DocumentObjectGroupPython] Cl_element016  label="Cl_element : 0.589"  # scripted group (container) (typed FeaturePython)
  n = 0.001
FEATURE [App::DocumentObjectGroupPython] K_element006  label="K_element : 0.004"  # scripted group (container) (typed FeaturePython)
  n = 0.004
FEATURE [App::DocumentObjectGroupPython] G4_MUSCLE_SKELETAL_ICRP  # scripted group (container) (typed FeaturePython)
  Dunit = g/cm3
  Dvalue = 1.05
  Group = -> [H_element057,C_element063,N_element025,O_element065,Na_element011,P_element007,S_element017,Cl_element016,K_element006]
  conduct = 2
  density = 1
  expand = 3
  formula = G4_MUSCLE_SKELETAL_ICRP
  name = G4_MUSCLE_SKELETAL_ICRP
  specific = 4
FEATURE [App::DocumentObjectGroupPython] H_element058  label="H_element : 0.137"  # scripted group (container) (typed FeaturePython)
  n = 0.102102
FEATURE [App::DocumentObjectGroupPython] C_element064  label="C_element : 0.123"  # scripted group (container) (typed FeaturePython)
  n = 0.123123
FEATURE [App::DocumentObjectGroupPython] N_element026  label="N_element : 0.756"  # scripted group (container) (typed FeaturePython)
  n = 0.035035
FEATURE [App::DocumentObjectGroupPython] O_element066  label="O_element : 0.730"  # scripted group (container) (typed FeaturePython)
  n = 0.72973
FEATURE [App::DocumentObjectGroupPython] Na_element012  label="Na_element : 0.099"  # scripted group (container) (typed FeaturePython)
  n = 0.001001
FEATURE [App::DocumentObjectGroupPython] P_element008  label="P_element : 0.106"  # scripted group (container) (typed FeaturePython)
  n = 0.002002
FEATURE [App::DocumentObjectGroupPython] S_element018  label="S_element : 0.019"  # scripted group (container) (typed FeaturePython)
  n = 0.004004
FEATURE [App::DocumentObjectGroupPython] K_element007  label="K_element : 0.016"  # scripted group (container) (typed FeaturePython)
  n = 0.003003
FEATURE [App::DocumentObjectGroupPython] G4_MUSCLE_STRIATED_ICRU  # scripted group (container) (typed FeaturePython)
  Dunit = g/cm3
  Dvalue = 1.04
  Group = -> [H_element058,C_element064,N_element026,O_element066,Na_element012,P_element008,S_element018,K_element007]
  conduct = 2
  density = 1
  expand = 3
  formula = G4_MUSCLE_STRIATED_ICRU
  name = G4_MUSCLE_STRIATED_ICRU
  specific = 4
FEATURE [App::DocumentObjectGroupPython] H_element059  label="H_element : 0.098"  # scripted group (container) (typed FeaturePython)
  n = 0.0982341
FEATURE [App::DocumentObjectGroupPython] C_element065  label="C_element : 0.156"  # scripted group (container) (typed FeaturePython)
  n = 0.156214
FEATURE [App::DocumentObjectGroupPython] N_element027  label="N_element : 0.757"  # scripted group (container) (typed FeaturePython)
  n = 0.035451
FEATURE [App::DocumentObjectGroupPython] O_element067  label="O_element : 0.880"  # scripted group (container) (typed FeaturePython)
  n = 0.710101
FEATURE [App::DocumentObjectGroupPython] G4_MUSCLE_WITH_SUCROSE  # scripted group (container) (typed FeaturePython)
  Dunit = g/cm3
  Dvalue = 1.11
  Group = -> [H_element059,C_element065,N_element027,O_element067]
  conduct = 2
  density = 1
  expand = 3
  formula = G4_MUSCLE_WITH_SUCROSE
  name = G4_MUSCLE_WITH_SUCROSE
  specific = 4
FEATURE [App::DocumentObjectGroupPython] H_element060  label="H_element : 0.138"  # scripted group (container) (typed FeaturePython)
  n = 0.101969
FEATURE [App::DocumentObjectGroupPython] C_element066  label="C_element : 0.120"  # scripted group (container) (typed FeaturePython)
  n = 0.120058
FEATURE [App::DocumentObjectGroupPython] N_element028  label="N_element : 0.758"  # scripted group (container) (typed FeaturePython)
  n = 0.035451
FEATURE [App::DocumentObjectGroupPython] O_element068  label="O_element : 0.743"  # scripted group (container) (typed FeaturePython)
  n = 0.742522
FEATURE [App::DocumentObjectGroupPython] G4_MUSCLE_WITHOUT_SUCROSE  # scripted group (container) (typed FeaturePython)
  Dunit = g/cm3
  Dvalue = 1.07
  Group = -> [H_element060,C_element066,N_element028,O_element068]
  conduct = 2
  density = 1
  expand = 3
  formula = G4_MUSCLE_WITHOUT_SUCROSE
  name = G4_MUSCLE_WITHOUT_SUCROSE
  specific = 4
FEATURE [App::DocumentObjectGroupPython] C_element067  label="C_element : 10"  # scripted group (container) (typed FeaturePython)
  n = 10
  ref = C_element
FEATURE [App::DocumentObjectGroupPython] H_element061  label="H_element : 030"  # scripted group (container) (typed FeaturePython)
  n = 8
  ref = H_element
FEATURE [App::DocumentObjectGroupPython] G4_NAPHTHALENE  # scripted group (container) (typed FeaturePython)
  Dunit = g/cm3
  Dvalue = 1.145
  Group = -> [C_element067,H_element061]
  conduct = 2
  density = 1
  expand = 3
  formula = G4_NAPHTHALENE
  name = G4_NAPHTHALENE
  specific = 4
FEATURE [App::DocumentObjectGroupPython] C_element068  label="C_element : 034"  # scripted group (container) (typed FeaturePython)
  n = 6
  ref = C_element
FEATURE [App::DocumentObjectGroupPython] H_element062  label="H_element : 031"  # scripted group (container) (typed FeaturePython)
  n = 5
  ref = H_element
FEATURE [App::DocumentObjectGroupPython] N_element029  label="N_element : 012"  # scripted group (container) (typed FeaturePython)
  n = 1
  ref = N_element
FEATURE [App::DocumentObjectGroupPython] O_element069  label="O_element : 034"  # scripted group (container) (typed FeaturePython)
  n = 2
  ref = O_element
FEATURE [App::DocumentObjectGroupPython] G4_NITROBENZENE  # scripted group (container) (typed FeaturePython)
  Dunit = g/cm3
  Dvalue = 1.19867
  Group = -> [C_element068,H_element062,N_element029,O_element069]
  conduct = 2
  density = 1
  expand = 3
  formula = G4_NITROBENZENE
  name = G4_NITROBENZENE
  specific = 4
FEATURE [App::DocumentObjectGroupPython] N_element030  label="N_element : 013"  # scripted group (container) (typed FeaturePython)
  n = 2
  ref = N_element
FEATURE [App::DocumentObjectGroupPython] O_element070  label="O_element : 035"  # scripted group (container) (typed FeaturePython)
  n = 1
  ref = O_element
FEATURE [App::DocumentObjectGroupPython] G4_NITROUS_OXIDE  # scripted group (container) (typed FeaturePython)
  Dunit = g/cm3
  Dvalue = 0.00183094
  Group = -> [N_element030,O_element070]
  conduct = 2
  density = 1
  expand = 3
  formula = G4_NITROUS_OXIDE
  name = G4_NITROUS_OXIDE
  specific = 4
FEATURE [App::DocumentObjectGroupPython] H_element063  label="H_element : 0.104"  # scripted group (container) (typed FeaturePython)
  n = 0.103509
FEATURE [App::DocumentObjectGroupPython] C_element069  label="C_element : 0.648"  # scripted group (container) (typed FeaturePython)
  n = 0.648416
FEATURE [App::DocumentObjectGroupPython] N_element031  label="N_element : 0.100"  # scripted group (container) (typed FeaturePython)
  n = 0.0995361
FEATURE [App::DocumentObjectGroupPython] O_element071  label="O_element : 0.149"  # scripted group (container) (typed FeaturePython)
  n = 0.148539
FEATURE [App::DocumentObjectGroupPython] G4_NYLON_8062  label="G4_NYLON-8062"  # scripted group (container) (typed FeaturePython)
  Dunit = g/cm3
  Dvalue = 1.08
  Group = -> [H_element063,C_element069,N_element031,O_element071]
  conduct = 2
  density = 1
  expand = 3
  formula = G4_NYLON-8062
  name = G4_NYLON-8062
  specific = 4
FEATURE [App::DocumentObjectGroupPython] C_element070  label="C_element : 035"  # scripted group (container) (typed FeaturePython)
  n = 6
  ref = C_element
FEATURE [App::DocumentObjectGroupPython] H_element064  label="H_element : 11"  # scripted group (container) (typed FeaturePython)
  n = 11
  ref = H_element
FEATURE [App::DocumentObjectGroupPython] N_element032  label="N_element : 014"  # scripted group (container) (typed FeaturePython)
  n = 1
  ref = N_element
FEATURE [App::DocumentObjectGroupPython] O_element072  label="O_element : 036"  # scripted group (container) (typed FeaturePython)
  n = 1
  ref = O_element
FEATURE [App::DocumentObjectGroupPython] G4_NYLON_6_6  label="G4_NYLON-6-6"  # scripted group (container) (typed FeaturePython)
  Dunit = g/cm3
  Dvalue = 1.14
  Group = -> [C_element070,H_element064,N_element032,O_element072]
  conduct = 2
  density = 1
  expand = 3
  formula = G4_NYLON-6-6
  name = G4_NYLON-6-6
  specific = 4
FEATURE [App::DocumentObjectGroupPython] H_element065  label="H_element : 0.139"  # scripted group (container) (typed FeaturePython)
  n = 0.107062
FEATURE [App::DocumentObjectGroupPython] C_element071  label="C_element : 0.680"  # scripted group (container) (typed FeaturePython)
  n = 0.680449
FEATURE [App::DocumentObjectGroupPython] N_element033  label="N_element : 0.099"  # scripted group (container) (typed FeaturePython)
  n = 0.099189
FEATURE [App::DocumentObjectGroupPython] O_element073  label="O_element : 0.113"  # scripted group (container) (typed FeaturePython)
  n = 0.1133
FEATURE [App::DocumentObjectGroupPython] G4_NYLON_6_10  label="G4_NYLON-6-10"  # scripted group (container) (typed FeaturePython)
  Dunit = g/cm3
  Dvalue = 1.14
  Group = -> [H_element065,C_element071,N_element033,O_element073]
  conduct = 2
  density = 1
  expand = 3
  formula = G4_NYLON-6-10
  name = G4_NYLON-6-10
  specific = 4
FEATURE [App::DocumentObjectGroupPython] H_element066  label="H_element : 0.140"  # scripted group (container) (typed FeaturePython)
  n = 0.115476
FEATURE [App::DocumentObjectGroupPython] C_element072  label="C_element : 0.721"  # scripted group (container) (typed FeaturePython)
  n = 0.720818
FEATURE [App::DocumentObjectGroupPython] N_element034  label="N_element : 0.076"  # scripted group (container) (typed FeaturePython)
  n = 0.0764169
FEATURE [App::DocumentObjectGroupPython] O_element074  label="O_element : 0.087"  # scripted group (container) (typed FeaturePython)
  n = 0.0872889
FEATURE [App::DocumentObjectGroupPython] G4_NYLON_11_RILSAN  label="G4_NYLON-11_RILSAN"  # scripted group (container) (typed FeaturePython)
  Dunit = g/cm3
  Dvalue = 1.425
  Group = -> [H_element066,C_element072,N_element034,O_element074]
  conduct = 2
  density = 1
  expand = 3
  formula = G4_NYLON-11_RILSAN
  name = G4_NYLON-11_RILSAN
  specific = 4
FEATURE [App::DocumentObjectGroupPython] C_element073  label="C_element : 8"  # scripted group (container) (typed FeaturePython)
  n = 8
  ref = C_element
FEATURE [App::DocumentObjectGroupPython] H_element067  label="H_element : 18"  # scripted group (container) (typed FeaturePython)
  n = 18
  ref = H_element
FEATURE [App::DocumentObjectGroupPython] G4_OCTANE  # scripted group (container) (typed FeaturePython)
  Dunit = g/cm3
  Dvalue = 0.7026
  Group = -> [C_element073,H_element067]
  conduct = 2
  density = 1
  expand = 3
  formula = G4_OCTANE
  name = G4_OCTANE
  specific = 4
FEATURE [App::DocumentObjectGroupPython] C_element074  label="C_element : 25"  # scripted group (container) (typed FeaturePython)
  n = 25
  ref = C_element
FEATURE [App::DocumentObjectGroupPython] H_element068  label="H_element : 52"  # scripted group (container) (typed FeaturePython)
  n = 52
  ref = H_element
FEATURE [App::DocumentObjectGroupPython] G4_PARAFFIN  # scripted group (container) (typed FeaturePython)
  Dunit = g/cm3
  Dvalue = 0.93
  Group = -> [C_element074,H_element068]
  conduct = 2
  density = 1
  expand = 3
  formula = G4_PARAFFIN
  name = G4_PARAFFIN
  specific = 4
FEATURE [App::DocumentObjectGroupPython] C_element075  label="C_element : 036"  # scripted group (container) (typed FeaturePython)
  n = 5
  ref = C_element
FEATURE [App::DocumentObjectGroupPython] H_element069  label="H_element : 032"  # scripted group (container) (typed FeaturePython)
  n = 12
  ref = H_element
FEATURE [App::DocumentObjectGroupPython] G4_N_PENTANE  label="G4_N-PENTANE"  # scripted group (container) (typed FeaturePython)
  Dunit = g/cm3
  Dvalue = 0.6262
  Group = -> [C_element075,H_element069]
  conduct = 2
  density = 1
  expand = 3
  formula = G4_N-PENTANE
  name = G4_N-PENTANE
  specific = 4
FEATURE [App::DocumentObjectGroupPython] H_element070  label="H_element : 0.014"  # scripted group (container) (typed FeaturePython)
  n = 0.0141
FEATURE [App::DocumentObjectGroupPython] C_element076  label="C_element : 0.072"  # scripted group (container) (typed FeaturePython)
  n = 0.072261
FEATURE [App::DocumentObjectGroupPython] N_element035  label="N_element : 0.019"  # scripted group (container) (typed FeaturePython)
  n = 0.01932
FEATURE [App::DocumentObjectGroupPython] O_element075  label="O_element : 0.066"  # scripted group (container) (typed FeaturePython)
  n = 0.066101
FEATURE [App::DocumentObjectGroupPython] S_element019  label="S_element : 0.020"  # scripted group (container) (typed FeaturePython)
  n = 0.00189
FEATURE [App::DocumentObjectGroupPython] Br_element004  label="Br_element : 0.349"  # scripted group (container) (typed FeaturePython)
  n = 0.349103
FEATURE [App::DocumentObjectGroupPython] Ag_element001  label="Ag_element : 0.474"  # scripted group (container) (typed FeaturePython)
  n = 0.474105
FEATURE [App::DocumentObjectGroupPython] I_element005  label="I_element : 0.003"  # scripted group (container) (typed FeaturePython)
  n = 0.00312
FEATURE [App::DocumentObjectGroupPython] G4_PHOTO_EMULSION  # scripted group (container) (typed FeaturePython)
  Dunit = g/cm3
  Dvalue = 3.815
  Group = -> [H_element070,C_element076,N_element035,O_element075,S_element019,Br_element004,Ag_element001,I_element005]
  conduct = 2
  density = 1
  expand = 3
  formula = G4_PHOTO_EMULSION
  name = G4_PHOTO_EMULSION
  specific = 4
FEATURE [App::DocumentObjectGroupPython] C_element077  label="C_element : 9"  # scripted group (container) (typed FeaturePython)
  n = 9
  ref = C_element
FEATURE [App::DocumentObjectGroupPython] H_element071  label="H_element : 033"  # scripted group (container) (typed FeaturePython)
  n = 10
  ref = H_element
FEATURE [App::DocumentObjectGroupPython] G4_PLASTIC_SC_VINYLTOLUENE  # scripted group (container) (typed FeaturePython)
  Dunit = g/cm3
  Dvalue = 1.032
  Group = -> [C_element077,H_element071]
  conduct = 2
  density = 1
  expand = 3
  formula = G4_PLASTIC_SC_VINYLTOLUENE
  name = G4_PLASTIC_SC_VINYLTOLUENE
  specific = 4
FEATURE [App::DocumentObjectGroupPython] Pu_element001  label="Pu_element : 1"  # scripted group (container) (typed FeaturePython)
  n = 1
  ref = Pu_element
FEATURE [App::DocumentObjectGroupPython] O_element076  label="O_element : 037"  # scripted group (container) (typed FeaturePython)
  n = 2
  ref = O_element
FEATURE [App::DocumentObjectGroupPython] G4_PLUTONIUM_DIOXIDE  # scripted group (container) (typed FeaturePython)
  Dunit = g/cm3
  Dvalue = 11.46
  Group = -> [Pu_element001,O_element076]
  conduct = 2
  density = 1
  expand = 3
  formula = G4_PLUTONIUM_DIOXIDE
  name = G4_PLUTONIUM_DIOXIDE
  specific = 4
FEATURE [App::DocumentObjectGroupPython] C_element078  label="C_element : 037"  # scripted group (container) (typed FeaturePython)
  n = 3
  ref = C_element
FEATURE [App::DocumentObjectGroupPython] H_element072  label="H_element : 034"  # scripted group (container) (typed FeaturePython)
  n = 3
  ref = H_element
FEATURE [App::DocumentObjectGroupPython] N_element036  label="N_element : 015"  # scripted group (container) (typed FeaturePython)
  n = 1
  ref = N_element
FEATURE [App::DocumentObjectGroupPython] G4_POLYACRYLONITRILE  # scripted group (container) (typed FeaturePython)
  Dunit = g/cm3
  Dvalue = 1.17
  Group = -> [C_element078,H_element072,N_element036]
  conduct = 2
  density = 1
  expand = 3
  formula = G4_POLYACRYLONITRILE
  name = G4_POLYACRYLONITRILE
  specific = 4
FEATURE [App::DocumentObjectGroupPython] C_element079  label="C_element : 16"  # scripted group (container) (typed FeaturePython)
  n = 16
  ref = C_element
FEATURE [App::DocumentObjectGroupPython] H_element073  label="H_element : 035"  # scripted group (container) (typed FeaturePython)
  n = 14
  ref = H_element
FEATURE [App::DocumentObjectGroupPython] O_element077  label="O_element : 038"  # scripted group (container) (typed FeaturePython)
  n = 3
  ref = O_element
FEATURE [App::DocumentObjectGroupPython] G4_POLYCARBONATE  # scripted group (container) (typed FeaturePython)
  Dunit = g/cm3
  Dvalue = 1.2
  Group = -> [C_element079,H_element073,O_element077]
  conduct = 2
  density = 1
  expand = 3
  formula = G4_POLYCARBONATE
  name = G4_POLYCARBONATE
  specific = 4
FEATURE [App::DocumentObjectGroupPython] C_element080  label="C_element : 038"  # scripted group (container) (typed FeaturePython)
  n = 8
  ref = C_element
FEATURE [App::DocumentObjectGroupPython] H_element074  label="H_element : 036"  # scripted group (container) (typed FeaturePython)
  n = 7
  ref = H_element
FEATURE [App::DocumentObjectGroupPython] Cl_element017  label="Cl_element : 007"  # scripted group (container) (typed FeaturePython)
  n = 1
  ref = Cl_element
FEATURE [App::DocumentObjectGroupPython] G4_POLYCHLOROSTYRENE  # scripted group (container) (typed FeaturePython)
  Dunit = g/cm3
  Dvalue = 1.3
  Group = -> [C_element080,H_element074,Cl_element017]
  conduct = 2
  density = 1
  expand = 3
  formula = G4_POLYCHLOROSTYRENE
  name = G4_POLYCHLOROSTYRENE
  specific = 4
FEATURE [App::DocumentObjectGroupPython] C_element081  label="C_element : 039"  # scripted group (container) (typed FeaturePython)
  n = 1
  ref = C_element
FEATURE [App::DocumentObjectGroupPython] H_element075  label="H_element : 037"  # scripted group (container) (typed FeaturePython)
  n = 2
  ref = H_element
FEATURE [App::DocumentObjectGroupPython] G4_POLYETHYLENE  # scripted group (container) (typed FeaturePython)
  Dunit = g/cm3
  Dvalue = 0.94
  Group = -> [C_element081,H_element075]
  conduct = 2
  density = 1
  expand = 3
  formula = G4_POLYETHYLENE
  name = G4_POLYETHYLENE
  specific = 4
FEATURE [App::DocumentObjectGroupPython] C_element082  label="C_element : 040"  # scripted group (container) (typed FeaturePython)
  n = 10
  ref = C_element
FEATURE [App::DocumentObjectGroupPython] H_element076  label="H_element : 038"  # scripted group (container) (typed FeaturePython)
  n = 8
  ref = H_element
FEATURE [App::DocumentObjectGroupPython] O_element078  label="O_element : 039"  # scripted group (container) (typed FeaturePython)
  n = 4
  ref = O_element
FEATURE [App::DocumentObjectGroupPython] G4_MYLAR  # scripted group (container) (typed FeaturePython)
  Dunit = g/cm3
  Dvalue = 1.4
  Group = -> [C_element082,H_element076,O_element078]
  conduct = 2
  density = 1
  expand = 3
  formula = G4_MYLAR
  name = G4_MYLAR
  specific = 4
FEATURE [App::DocumentObjectGroupPython] C_element083  label="C_element : 041"  # scripted group (container) (typed FeaturePython)
  n = 5
  ref = C_element
FEATURE [App::DocumentObjectGroupPython] H_element077  label="H_element : 039"  # scripted group (container) (typed FeaturePython)
  n = 8
  ref = H_element
FEATURE [App::DocumentObjectGroupPython] O_element079  label="O_element : 040"  # scripted group (container) (typed FeaturePython)
  n = 2
  ref = O_element
FEATURE [App::DocumentObjectGroupPython] G4_PLEXIGLASS  # scripted group (container) (typed FeaturePython)
  Dunit = g/cm3
  Dvalue = 1.19
  Group = -> [C_element083,H_element077,O_element079]
  conduct = 2
  density = 1
  expand = 3
  formula = G4_PLEXIGLASS
  name = G4_PLEXIGLASS
  specific = 4
FEATURE [App::DocumentObjectGroupPython] C_element084  label="C_element : 042"  # scripted group (container) (typed FeaturePython)
  n = 1
  ref = C_element
FEATURE [App::DocumentObjectGroupPython] H_element078  label="H_element : 040"  # scripted group (container) (typed FeaturePython)
  n = 2
  ref = H_element
FEATURE [App::DocumentObjectGroupPython] O_element080  label="O_element : 041"  # scripted group (container) (typed FeaturePython)
  n = 1
  ref = O_element
FEATURE [App::DocumentObjectGroupPython] G4_POLYOXYMETHYLENE  # scripted group (container) (typed FeaturePython)
  Dunit = g/cm3
  Dvalue = 1.425
  Group = -> [C_element084,H_element078,O_element080]
  conduct = 2
  density = 1
  expand = 3
  formula = G4_POLYOXYMETHYLENE
  name = G4_POLYOXYMETHYLENE
  specific = 4
FEATURE [App::DocumentObjectGroupPython] C_element085  label="C_element : 043"  # scripted group (container) (typed FeaturePython)
  n = 2
  ref = C_element
FEATURE [App::DocumentObjectGroupPython] H_element079  label="H_element : 041"  # scripted group (container) (typed FeaturePython)
  n = 4
  ref = H_element
FEATURE [App::DocumentObjectGroupPython] G4_POLYPROPYLENE  # scripted group (container) (typed FeaturePython)
  Dunit = g/cm3
  Dvalue = 0.9
  Group = -> [C_element085,H_element079]
  conduct = 2
  density = 1
  expand = 3
  formula = G4_POLYPROPYLENE
  name = G4_POLYPROPYLENE
  specific = 4
FEATURE [App::DocumentObjectGroupPython] C_element086  label="C_element : 044"  # scripted group (container) (typed FeaturePython)
  n = 8
  ref = C_element
FEATURE [App::DocumentObjectGroupPython] H_element080  label="H_element : 042"  # scripted group (container) (typed FeaturePython)
  n = 8
  ref = H_element
FEATURE [App::DocumentObjectGroupPython] G4_POLYSTYRENE  # scripted group (container) (typed FeaturePython)
  Dunit = g/cm3
  Dvalue = 1.06
  Group = -> [C_element086,H_element080]
  conduct = 2
  density = 1
  expand = 3
  formula = G4_POLYSTYRENE
  name = G4_POLYSTYRENE
  specific = 4
FEATURE [App::DocumentObjectGroupPython] C_element087  label="C_element : 045"  # scripted group (container) (typed FeaturePython)
  n = 2
  ref = C_element
FEATURE [App::DocumentObjectGroupPython] F_element014  label="F_element : 4"  # scripted group (container) (typed FeaturePython)
  n = 4
  ref = F_element
FEATURE [App::DocumentObjectGroupPython] G4_TEFLON  # scripted group (container) (typed FeaturePython)
  Dunit = g/cm3
  Dvalue = 2.2
  Group = -> [C_element087,F_element014]
  conduct = 2
  density = 1
  expand = 3
  formula = G4_TEFLON
  name = G4_TEFLON
  specific = 4
FEATURE [App::DocumentObjectGroupPython] C_element088  label="C_element : 046"  # scripted group (container) (typed FeaturePython)
  n = 2
  ref = C_element
FEATURE [App::DocumentObjectGroupPython] F_element015  label="F_element : 006"  # scripted group (container) (typed FeaturePython)
  n = 3
  ref = F_element
FEATURE [App::DocumentObjectGroupPython] Cl_element018  label="Cl_element : 008"  # scripted group (container) (typed FeaturePython)
  n = 1
  ref = Cl_element
FEATURE [App::DocumentObjectGroupPython] G4_POLYTRIFLUOROCHLOROETHYLENE  # scripted group (container) (typed FeaturePython)
  Dunit = g/cm3
  Dvalue = 2.1
  Group = -> [C_element088,F_element015,Cl_element018]
  conduct = 2
  density = 1
  expand = 3
  formula = G4_POLYTRIFLUOROCHLOROETHYLENE
  name = G4_POLYTRIFLUOROCHLOROETHYLENE
  specific = 4
FEATURE [App::DocumentObjectGroupPython] C_element089  label="C_element : 047"  # scripted group (container) (typed FeaturePython)
  n = 4
  ref = C_element
FEATURE [App::DocumentObjectGroupPython] H_element081  label="H_element : 043"  # scripted group (container) (typed FeaturePython)
  n = 6
  ref = H_element
FEATURE [App::DocumentObjectGroupPython] O_element081  label="O_element : 042"  # scripted group (container) (typed FeaturePython)
  n = 2
  ref = O_element
FEATURE [App::DocumentObjectGroupPython] G4_POLYVINYL_ACETATE  # scripted group (container) (typed FeaturePython)
  Dunit = g/cm3
  Dvalue = 1.19
  Group = -> [C_element089,H_element081,O_element081]
  conduct = 2
  density = 1
  expand = 3
  formula = G4_POLYVINYL_ACETATE
  name = G4_POLYVINYL_ACETATE
  specific = 4
FEATURE [App::DocumentObjectGroupPython] C_element090  label="C_element : 048"  # scripted group (container) (typed FeaturePython)
  n = 2
  ref = C_element
FEATURE [App::DocumentObjectGroupPython] H_element082  label="H_element : 044"  # scripted group (container) (typed FeaturePython)
  n = 4
  ref = H_element
FEATURE [App::DocumentObjectGroupPython] O_element082  label="O_element : 043"  # scripted group (container) (typed FeaturePython)
  n = 1
  ref = O_element
FEATURE [App::DocumentObjectGroupPython] G4_POLYVINYL_ALCOHOL  # scripted group (container) (typed FeaturePython)
  Dunit = g/cm3
  Dvalue = 1.3
  Group = -> [C_element090,H_element082,O_element082]
  conduct = 2
  density = 1
  expand = 3
  formula = G4_POLYVINYL_ALCOHOL
  name = G4_POLYVINYL_ALCOHOL
  specific = 4
FEATURE [App::DocumentObjectGroupPython] C_element091  label="C_element : 049"  # scripted group (container) (typed FeaturePython)
  n = 8
  ref = C_element
FEATURE [App::DocumentObjectGroupPython] H_element083  label="H_element : 045"  # scripted group (container) (typed FeaturePython)
  n = 14
  ref = H_element
FEATURE [App::DocumentObjectGroupPython] O_element083  label="O_element : 044"  # scripted group (container) (typed FeaturePython)
  n = 2
  ref = O_element
FEATURE [App::DocumentObjectGroupPython] G4_POLYVINYL_BUTYRAL  # scripted group (container) (typed FeaturePython)
  Dunit = g/cm3
  Dvalue = 1.12
  Group = -> [C_element091,H_element083,O_element083]
  conduct = 2
  density = 1
  expand = 3
  formula = G4_POLYVINYL_BUTYRAL
  name = G4_POLYVINYL_BUTYRAL
  specific = 4
FEATURE [App::DocumentObjectGroupPython] C_element092  label="C_element : 050"  # scripted group (container) (typed FeaturePython)
  n = 2
  ref = C_element
FEATURE [App::DocumentObjectGroupPython] H_element084  label="H_element : 046"  # scripted group (container) (typed FeaturePython)
  n = 3
  ref = H_element
FEATURE [App::DocumentObjectGroupPython] Cl_element019  label="Cl_element : 009"  # scripted group (container) (typed FeaturePython)
  n = 1
  ref = Cl_element
FEATURE [App::DocumentObjectGroupPython] G4_POLYVINYL_CHLORIDE  # scripted group (container) (typed FeaturePython)
  Dunit = g/cm3
  Dvalue = 1.3
  Group = -> [C_element092,H_element084,Cl_element019]
  conduct = 2
  density = 1
  expand = 3
  formula = G4_POLYVINYL_CHLORIDE
  name = G4_POLYVINYL_CHLORIDE
  specific = 4
FEATURE [App::DocumentObjectGroupPython] C_element093  label="C_element : 051"  # scripted group (container) (typed FeaturePython)
  n = 2
  ref = C_element
FEATURE [App::DocumentObjectGroupPython] H_element085  label="H_element : 047"  # scripted group (container) (typed FeaturePython)
  n = 2
  ref = H_element
FEATURE [App::DocumentObjectGroupPython] Cl_element020  label="Cl_element : 010"  # scripted group (container) (typed FeaturePython)
  n = 2
  ref = Cl_element
FEATURE [App::DocumentObjectGroupPython] G4_POLYVINYLIDENE_CHLORIDE  # scripted group (container) (typed FeaturePython)
  Dunit = g/cm3
  Dvalue = 1.7
  Group = -> [C_element093,H_element085,Cl_element020]
  conduct = 2
  density = 1
  expand = 3
  formula = G4_POLYVINYLIDENE_CHLORIDE
  name = G4_POLYVINYLIDENE_CHLORIDE
  specific = 4
FEATURE [App::DocumentObjectGroupPython] C_element094  label="C_element : 052"  # scripted group (container) (typed FeaturePython)
  n = 2
  ref = C_element
FEATURE [App::DocumentObjectGroupPython] H_element086  label="H_element : 048"  # scripted group (container) (typed FeaturePython)
  n = 2
  ref = H_element
FEATURE [App::DocumentObjectGroupPython] F_element016  label="F_element : 007"  # scripted group (container) (typed FeaturePython)
  n = 2
  ref = F_element
FEATURE [App::DocumentObjectGroupPython] G4_POLYVINYLIDENE_FLUORIDE  # scripted group (container) (typed FeaturePython)
  Dunit = g/cm3
  Dvalue = 1.76
  Group = -> [C_element094,H_element086,F_element016]
  conduct = 2
  density = 1
  expand = 3
  formula = G4_POLYVINYLIDENE_FLUORIDE
  name = G4_POLYVINYLIDENE_FLUORIDE
  specific = 4
FEATURE [App::DocumentObjectGroupPython] C_element095  label="C_element : 053"  # scripted group (container) (typed FeaturePython)
  n = 6
  ref = C_element
FEATURE [App::DocumentObjectGroupPython] H_element087  label="H_element : 9"  # scripted group (container) (typed FeaturePython)
  n = 9
  ref = H_element
FEATURE [App::DocumentObjectGroupPython] N_element037  label="N_element : 016"  # scripted group (container) (typed FeaturePython)
  n = 1
  ref = N_element
FEATURE [App::DocumentObjectGroupPython] O_element084  label="O_element : 045"  # scripted group (container) (typed FeaturePython)
  n = 1
  ref = O_element
FEATURE [App::DocumentObjectGroupPython] G4_POLYVINYL_PYRROLIDONE  # scripted group (container) (typed FeaturePython)
  Dunit = g/cm3
  Dvalue = 1.25
  Group = -> [C_element095,H_element087,N_element037,O_element084]
  conduct = 2
  density = 1
  expand = 3
  formula = G4_POLYVINYL_PYRROLIDONE
  name = G4_POLYVINYL_PYRROLIDONE
  specific = 4
FEATURE [App::DocumentObjectGroupPython] K_element008  label="K_element : 1"  # scripted group (container) (typed FeaturePython)
  n = 1
  ref = K_element
FEATURE [App::DocumentObjectGroupPython] I_element006  label="I_element : 003"  # scripted group (container) (typed FeaturePython)
  n = 1
  ref = I_element
FEATURE [App::DocumentObjectGroupPython] G4_POTASSIUM_IODIDE  # scripted group (container) (typed FeaturePython)
  Dunit = g/cm3
  Dvalue = 3.13
  Group = -> [K_element008,I_element006]
  conduct = 2
  density = 1
  expand = 3
  formula = G4_POTASSIUM_IODIDE
  name = G4_POTASSIUM_IODIDE
  specific = 4
FEATURE [App::DocumentObjectGroupPython] K_element009  label="K_element : 2"  # scripted group (container) (typed FeaturePython)
  n = 2
  ref = K_element
FEATURE [App::DocumentObjectGroupPython] O_element085  label="O_element : 046"  # scripted group (container) (typed FeaturePython)
  n = 1
  ref = O_element
FEATURE [App::DocumentObjectGroupPython] G4_POTASSIUM_OXIDE  # scripted group (container) (typed FeaturePython)
  Dunit = g/cm3
  Dvalue = 2.32
  Group = -> [K_element009,O_element085]
  conduct = 2
  density = 1
  expand = 3
  formula = G4_POTASSIUM_OXIDE
  name = G4_POTASSIUM_OXIDE
  specific = 4
FEATURE [App::DocumentObjectGroupPython] C_element096  label="C_element : 054"  # scripted group (container) (typed FeaturePython)
  n = 3
  ref = C_element
FEATURE [App::DocumentObjectGroupPython] H_element088  label="H_element : 049"  # scripted group (container) (typed FeaturePython)
  n = 8
  ref = H_element
FEATURE [App::DocumentObjectGroupPython] G4_PROPANE  # scripted group (container) (typed FeaturePython)
  Dunit = g/cm3
  Dvalue = 0.00187939
  Group = -> [C_element096,H_element088]
  conduct = 2
  density = 1
  expand = 3
  formula = G4_PROPANE
  name = G4_PROPANE
  specific = 4
FEATURE [App::DocumentObjectGroupPython] C_element097  label="C_element : 055"  # scripted group (container) (typed FeaturePython)
  n = 3
  ref = C_element
FEATURE [App::DocumentObjectGroupPython] H_element089  label="H_element : 050"  # scripted group (container) (typed FeaturePython)
  n = 8
  ref = H_element
FEATURE [App::DocumentObjectGroupPython] G4_lPROPANE  # scripted group (container) (typed FeaturePython)
  Dunit = g/cm3
  Dvalue = 0.43
  Group = -> [C_element097,H_element089]
  conduct = 2
  density = 1
  expand = 3
  formula = G4_lPROPANE
  name = G4_lPROPANE
  specific = 4
FEATURE [App::DocumentObjectGroupPython] C_element098  label="C_element : 056"  # scripted group (container) (typed FeaturePython)
  n = 3
  ref = C_element
FEATURE [App::DocumentObjectGroupPython] H_element090  label="H_element : 051"  # scripted group (container) (typed FeaturePython)
  n = 8
  ref = H_element
FEATURE [App::DocumentObjectGroupPython] O_element086  label="O_element : 047"  # scripted group (container) (typed FeaturePython)
  n = 1
  ref = O_element
FEATURE [App::DocumentObjectGroupPython] G4_N_PROPYL_ALCOHOL  label="G4_N-PROPYL_ALCOHOL"  # scripted group (container) (typed FeaturePython)
  Dunit = g/cm3
  Dvalue = 0.8035
  Group = -> [C_element098,H_element090,O_element086]
  conduct = 2
  density = 1
  expand = 3
  formula = G4_N-PROPYL_ALCOHOL
  name = G4_N-PROPYL_ALCOHOL
  specific = 4
FEATURE [App::DocumentObjectGroupPython] C_element099  label="C_element : 057"  # scripted group (container) (typed FeaturePython)
  n = 5
  ref = C_element
FEATURE [App::DocumentObjectGroupPython] H_element091  label="H_element : 052"  # scripted group (container) (typed FeaturePython)
  n = 5
  ref = H_element
FEATURE [App::DocumentObjectGroupPython] N_element038  label="N_element : 017"  # scripted group (container) (typed FeaturePython)
  n = 1
  ref = N_element
FEATURE [App::DocumentObjectGroupPython] G4_PYRIDINE  # scripted group (container) (typed FeaturePython)
  Dunit = g/cm3
  Dvalue = 0.9819
  Group = -> [C_element099,H_element091,N_element038]
  conduct = 2
  density = 1
  expand = 3
  formula = G4_PYRIDINE
  name = G4_PYRIDINE
  specific = 4
FEATURE [App::DocumentObjectGroupPython] H_element092  label="H_element : 0.144"  # scripted group (container) (typed FeaturePython)
  n = 0.143711
FEATURE [App::DocumentObjectGroupPython] C_element100  label="C_element : 0.856"  # scripted group (container) (typed FeaturePython)
  n = 0.856289
FEATURE [App::DocumentObjectGroupPython] G4_RUBBER_BUTYL  # scripted group (container) (typed FeaturePython)
  Dunit = g/cm3
  Dvalue = 0.92
  Group = -> [H_element092,C_element100]
  conduct = 2
  density = 1
  expand = 3
  formula = G4_RUBBER_BUTYL
  name = G4_RUBBER_BUTYL
  specific = 4
FEATURE [App::DocumentObjectGroupPython] H_element093  label="H_element : 0.118"  # scripted group (container) (typed FeaturePython)
  n = 0.118371
FEATURE [App::DocumentObjectGroupPython] C_element101  label="C_element : 0.882"  # scripted group (container) (typed FeaturePython)
  n = 0.881629
FEATURE [App::DocumentObjectGroupPython] G4_RUBBER_NATURAL  # scripted group (container) (typed FeaturePython)
  Dunit = g/cm3
  Dvalue = 0.92
  Group = -> [H_element093,C_element101]
  conduct = 2
  density = 1
  expand = 3
  formula = G4_RUBBER_NATURAL
  name = G4_RUBBER_NATURAL
  specific = 4
FEATURE [App::DocumentObjectGroupPython] H_element094  label="H_element : 0.145"  # scripted group (container) (typed FeaturePython)
  n = 0.05692
FEATURE [App::DocumentObjectGroupPython] C_element102  label="C_element : 0.543"  # scripted group (container) (typed FeaturePython)
  n = 0.542646
FEATURE [App::DocumentObjectGroupPython] Cl_element021  label="Cl_element : 0.400"  # scripted group (container) (typed FeaturePython)
  n = 0.400434
FEATURE [App::DocumentObjectGroupPython] G4_RUBBER_NEOPRENE  # scripted group (container) (typed FeaturePython)
  Dunit = g/cm3
  Dvalue = 1.23
  Group = -> [H_element094,C_element102,Cl_element021]
  conduct = 2
  density = 1
  expand = 3
  formula = G4_RUBBER_NEOPRENE
  name = G4_RUBBER_NEOPRENE
  specific = 4
FEATURE [App::DocumentObjectGroupPython] Si_element006  label="Si_element : 1"  # scripted group (container) (typed FeaturePython)
  n = 1
  ref = Si_element
FEATURE [App::DocumentObjectGroupPython] O_element087  label="O_element : 048"  # scripted group (container) (typed FeaturePython)
  n = 2
  ref = O_element
FEATURE [App::DocumentObjectGroupPython] G4_SILICON_DIOXIDE  # scripted group (container) (typed FeaturePython)
  Dunit = g/cm3
  Dvalue = 2.32
  Group = -> [Si_element006,O_element087]
  conduct = 2
  density = 1
  expand = 3
  formula = G4_SILICON_DIOXIDE
  name = G4_SILICON_DIOXIDE
  specific = 4
FEATURE [App::DocumentObjectGroupPython] Ag_element002  label="Ag_element : 1"  # scripted group (container) (typed FeaturePython)
  n = 1
  ref = Ag_element
FEATURE [App::DocumentObjectGroupPython] Br_element005  label="Br_element : 003"  # scripted group (container) (typed FeaturePython)
  n = 1
  ref = Br_element
FEATURE [App::DocumentObjectGroupPython] G4_SILVER_BROMIDE  # scripted group (container) (typed FeaturePython)
  Dunit = g/cm3
  Dvalue = 6.473
  Group = -> [Ag_element002,Br_element005]
  conduct = 2
  density = 1
  expand = 3
  formula = G4_SILVER_BROMIDE
  name = G4_SILVER_BROMIDE
  specific = 4
FEATURE [App::DocumentObjectGroupPython] Ag_element003  label="Ag_element : 002"  # scripted group (container) (typed FeaturePython)
  n = 1
  ref = Ag_element
FEATURE [App::DocumentObjectGroupPython] Cl_element022  label="Cl_element : 011"  # scripted group (container) (typed FeaturePython)
  n = 1
  ref = Cl_element
FEATURE [App::DocumentObjectGroupPython] G4_SILVER_CHLORIDE  # scripted group (container) (typed FeaturePython)
  Dunit = g/cm3
  Dvalue = 5.56
  Group = -> [Ag_element003,Cl_element022]
  conduct = 2
  density = 1
  expand = 3
  formula = G4_SILVER_CHLORIDE
  name = G4_SILVER_CHLORIDE
  specific = 4
FEATURE [App::DocumentObjectGroupPython] Br_element006  label="Br_element : 0.423"  # scripted group (container) (typed FeaturePython)
  n = 0.422895
FEATURE [App::DocumentObjectGroupPython] Ag_element004  label="Ag_element : 0.574"  # scripted group (container) (typed FeaturePython)
  n = 0.573748
FEATURE [App::DocumentObjectGroupPython] I_element007  label="I_element : 0.649"  # scripted group (container) (typed FeaturePython)
  n = 0.003357
FEATURE [App::DocumentObjectGroupPython] G4_SILVER_HALIDES  # scripted group (container) (typed FeaturePython)
  Dunit = g/cm3
  Dvalue = 6.47
  Group = -> [Br_element006,Ag_element004,I_element007]
  conduct = 2
  density = 1
  expand = 3
  formula = G4_SILVER_HALIDES
  name = G4_SILVER_HALIDES
  specific = 4
FEATURE [App::DocumentObjectGroupPython] Ag_element005  label="Ag_element : 003"  # scripted group (container) (typed FeaturePython)
  n = 1
  ref = Ag_element
FEATURE [App::DocumentObjectGroupPython] I_element008  label="I_element : 004"  # scripted group (container) (typed FeaturePython)
  n = 1
  ref = I_element
FEATURE [App::DocumentObjectGroupPython] G4_SILVER_IODIDE  # scripted group (container) (typed FeaturePython)
  Dunit = g/cm3
  Dvalue = 6.01
  Group = -> [Ag_element005,I_element008]
  conduct = 2
  density = 1
  expand = 3
  formula = G4_SILVER_IODIDE
  name = G4_SILVER_IODIDE
  specific = 4
FEATURE [App::DocumentObjectGroupPython] H_element095  label="H_element : 0.100"  # scripted group (container) (typed FeaturePython)
  n = 0.1
FEATURE [App::DocumentObjectGroupPython] C_element103  label="C_element : 0.204"  # scripted group (container) (typed FeaturePython)
  n = 0.204
FEATURE [App::DocumentObjectGroupPython] N_element039  label="N_element : 0.759"  # scripted group (container) (typed FeaturePython)
  n = 0.042
FEATURE [App::DocumentObjectGroupPython] O_element088  label="O_element : 0.645"  # scripted group (container) (typed FeaturePython)
  n = 0.645
FEATURE [App::DocumentObjectGroupPython] Na_element013  label="Na_element : 0.100"  # scripted group (container) (typed FeaturePython)
  n = 0.002
FEATURE [App::DocumentObjectGroupPython] P_element009  label="P_element : 0.107"  # scripted group (container) (typed FeaturePython)
  n = 0.001
FEATURE [App::DocumentObjectGroupPython] S_element020  label="S_element : 0.021"  # scripted group (container) (typed FeaturePython)
  n = 0.002
FEATURE [App::DocumentObjectGroupPython] Cl_element023  label="Cl_element : 0.590"  # scripted group (container) (typed FeaturePython)
  n = 0.003
FEATURE [App::DocumentObjectGroupPython] K_element010  label="K_element : 0.001"  # scripted group (container) (typed FeaturePython)
  n = 0.001
FEATURE [App::DocumentObjectGroupPython] G4_SKIN_ICRP  # scripted group (container) (typed FeaturePython)
  Dunit = g/cm3
  Dvalue = 1.09
  Group = -> [H_element095,C_element103,N_element039,O_element088,Na_element013,P_element009,S_element020,Cl_element023,K_element010]
  conduct = 2
  density = 1
  expand = 3
  formula = G4_SKIN_ICRP
  name = G4_SKIN_ICRP
  specific = 4
FEATURE [App::DocumentObjectGroupPython] Na_element014  label="Na_element : 2"  # scripted group (container) (typed FeaturePython)
  n = 2
  ref = Na_element
FEATURE [App::DocumentObjectGroupPython] C_element104  label="C_element : 058"  # scripted group (container) (typed FeaturePython)
  n = 1
  ref = C_element
FEATURE [App::DocumentObjectGroupPython] O_element089  label="O_element : 049"  # scripted group (container) (typed FeaturePython)
  n = 3
  ref = O_element
FEATURE [App::DocumentObjectGroupPython] G4_SODIUM_CARBONATE  # scripted group (container) (typed FeaturePython)
  Dunit = g/cm3
  Dvalue = 2.532
  Group = -> [Na_element014,C_element104,O_element089]
  conduct = 2
  density = 1
  expand = 3
  formula = G4_SODIUM_CARBONATE
  name = G4_SODIUM_CARBONATE
  specific = 4
FEATURE [App::DocumentObjectGroupPython] Na_element015  label="Na_element : 1"  # scripted group (container) (typed FeaturePython)
  n = 1
  ref = Na_element
FEATURE [App::DocumentObjectGroupPython] I_element009  label="I_element : 005"  # scripted group (container) (typed FeaturePython)
  n = 1
  ref = I_element
FEATURE [App::DocumentObjectGroupPython] G4_SODIUM_IODIDE  # scripted group (container) (typed FeaturePython)
  Dunit = g/cm3
  Dvalue = 3.667
  Group = -> [Na_element015,I_element009]
  conduct = 2
  density = 1
  expand = 3
  formula = G4_SODIUM_IODIDE
  name = G4_SODIUM_IODIDE
  specific = 4
FEATURE [App::DocumentObjectGroupPython] Na_element016  label="Na_element : 003"  # scripted group (container) (typed FeaturePython)
  n = 2
  ref = Na_element
FEATURE [App::DocumentObjectGroupPython] O_element090  label="O_element : 050"  # scripted group (container) (typed FeaturePython)
  n = 1
  ref = O_element
FEATURE [App::DocumentObjectGroupPython] G4_SODIUM_MONOXIDE  # scripted group (container) (typed FeaturePython)
  Dunit = g/cm3
  Dvalue = 2.27
  Group = -> [Na_element016,O_element090]
  conduct = 2
  density = 1
  expand = 3
  formula = G4_SODIUM_MONOXIDE
  name = G4_SODIUM_MONOXIDE
  specific = 4
FEATURE [App::DocumentObjectGroupPython] Na_element017  label="Na_element : 004"  # scripted group (container) (typed FeaturePython)
  n = 1
  ref = Na_element
FEATURE [App::DocumentObjectGroupPython] N_element040  label="N_element : 018"  # scripted group (container) (typed FeaturePython)
  n = 1
  ref = N_element
FEATURE [App::DocumentObjectGroupPython] O_element091  label="O_element : 051"  # scripted group (container) (typed FeaturePython)
  n = 3
  ref = O_element
FEATURE [App::DocumentObjectGroupPython] G4_SODIUM_NITRATE  # scripted group (container) (typed FeaturePython)
  Dunit = g/cm3
  Dvalue = 2.261
  Group = -> [Na_element017,N_element040,O_element091]
  conduct = 2
  density = 1
  expand = 3
  formula = G4_SODIUM_NITRATE
  name = G4_SODIUM_NITRATE
  specific = 4
FEATURE [App::DocumentObjectGroupPython] C_element105  label="C_element : 059"  # scripted group (container) (typed FeaturePython)
  n = 14
  ref = C_element
FEATURE [App::DocumentObjectGroupPython] H_element096  label="H_element : 053"  # scripted group (container) (typed FeaturePython)
  n = 12
  ref = H_element
FEATURE [App::DocumentObjectGroupPython] G4_STILBENE  # scripted group (container) (typed FeaturePython)
  Dunit = g/cm3
  Dvalue = 0.9707
  Group = -> [C_element105,H_element096]
  conduct = 2
  density = 1
  expand = 3
  formula = G4_STILBENE
  name = G4_STILBENE
  specific = 4
FEATURE [App::DocumentObjectGroupPython] C_element106  label="C_element : 12"  # scripted group (container) (typed FeaturePython)
  n = 12
  ref = C_element
FEATURE [App::DocumentObjectGroupPython] H_element097  label="H_element : 22"  # scripted group (container) (typed FeaturePython)
  n = 22
  ref = H_element
FEATURE [App::DocumentObjectGroupPython] O_element092  label="O_element : 11"  # scripted group (container) (typed FeaturePython)
  n = 11
  ref = O_element
FEATURE [App::DocumentObjectGroupPython] G4_SUCROSE  # scripted group (container) (typed FeaturePython)
  Dunit = g/cm3
  Dvalue = 1.5805
  Group = -> [C_element106,H_element097,O_element092]
  conduct = 2
  density = 1
  expand = 3
  formula = G4_SUCROSE
  name = G4_SUCROSE
  specific = 4
FEATURE [App::DocumentObjectGroupPython] C_element107  label="C_element : 18"  # scripted group (container) (typed FeaturePython)
  n = 18
  ref = C_element
FEATURE [App::DocumentObjectGroupPython] H_element098  label="H_element : 054"  # scripted group (container) (typed FeaturePython)
  n = 14
  ref = H_element
FEATURE [App::DocumentObjectGroupPython] G4_TERPHENYL  # scripted group (container) (typed FeaturePython)
  Dunit = g/cm3
  Dvalue = 1.24
  Group = -> [C_element107,H_element098]
  conduct = 2
  density = 1
  expand = 3
  formula = G4_TERPHENYL
  name = G4_TERPHENYL
  specific = 4
FEATURE [App::DocumentObjectGroupPython] H_element099  label="H_element : 0.146"  # scripted group (container) (typed FeaturePython)
  n = 0.106
FEATURE [App::DocumentObjectGroupPython] C_element108  label="C_element : 0.883"  # scripted group (container) (typed FeaturePython)
  n = 0.099
FEATURE [App::DocumentObjectGroupPython] N_element041  label="N_element : 0.020"  # scripted group (container) (typed FeaturePython)
  n = 0.02
FEATURE [App::DocumentObjectGroupPython] O_element093  label="O_element : 0.766"  # scripted group (container) (typed FeaturePython)
  n = 0.766
FEATURE [App::DocumentObjectGroupPython] Na_element018  label="Na_element : 0.101"  # scripted group (container) (typed FeaturePython)
  n = 0.002
FEATURE [App::DocumentObjectGroupPython] P_element010  label="P_element : 0.108"  # scripted group (container) (typed FeaturePython)
  n = 0.001
FEATURE [App::DocumentObjectGroupPython] S_element021  label="S_element : 0.022"  # scripted group (container) (typed FeaturePython)
  n = 0.002
FEATURE [App::DocumentObjectGroupPython] Cl_element024  label="Cl_element : 0.002"  # scripted group (container) (typed FeaturePython)
  n = 0.002
FEATURE [App::DocumentObjectGroupPython] K_element011  label="K_element : 0.017"  # scripted group (container) (typed FeaturePython)
  n = 0.002
FEATURE [App::DocumentObjectGroupPython] G4_TESTIS_ICRP  # scripted group (container) (typed FeaturePython)
  Dunit = g/cm3
  Dvalue = 1.04
  Group = -> [H_element099,C_element108,N_element041,O_element093,Na_element018,P_element010,S_element021,Cl_element024,K_element011]
  conduct = 2
  density = 1
  expand = 3
  formula = G4_TESTIS_ICRP
  name = G4_TESTIS_ICRP
  specific = 4
FEATURE [App::DocumentObjectGroupPython] C_element109  label="C_element : 060"  # scripted group (container) (typed FeaturePython)
  n = 2
  ref = C_element
FEATURE [App::DocumentObjectGroupPython] Cl_element025  label="Cl_element : 012"  # scripted group (container) (typed FeaturePython)
  n = 4
  ref = Cl_element
FEATURE [App::DocumentObjectGroupPython] G4_TETRACHLOROETHYLENE  # scripted group (container) (typed FeaturePython)
  Dunit = g/cm3
  Dvalue = 1.625
  Group = -> [C_element109,Cl_element025]
  conduct = 2
  density = 1
  expand = 3
  formula = G4_TETRACHLOROETHYLENE
  name = G4_TETRACHLOROETHYLENE
  specific = 4
FEATURE [App::DocumentObjectGroupPython] Tl_element001  label="Tl_element : 1"  # scripted group (container) (typed FeaturePython)
  n = 1
  ref = Tl_element
FEATURE [App::DocumentObjectGroupPython] Cl_element026  label="Cl_element : 013"  # scripted group (container) (typed FeaturePython)
  n = 1
  ref = Cl_element
FEATURE [App::DocumentObjectGroupPython] G4_THALLIUM_CHLORIDE  # scripted group (container) (typed FeaturePython)
  Dunit = g/cm3
  Dvalue = 7.004
  Group = -> [Tl_element001,Cl_element026]
  conduct = 2
  density = 1
  expand = 3
  formula = G4_THALLIUM_CHLORIDE
  name = G4_THALLIUM_CHLORIDE
  specific = 4
FEATURE [App::DocumentObjectGroupPython] H_element100  label="H_element : 0.147"  # scripted group (container) (typed FeaturePython)
  n = 0.105
FEATURE [App::DocumentObjectGroupPython] C_element110  label="C_element : 0.256"  # scripted group (container) (typed FeaturePython)
  n = 0.256
FEATURE [App::DocumentObjectGroupPython] N_element042  label="N_element : 0.760"  # scripted group (container) (typed FeaturePython)
  n = 0.027
FEATURE [App::DocumentObjectGroupPython] O_element094  label="O_element : 0.602"  # scripted group (container) (typed FeaturePython)
  n = 0.602
FEATURE [App::DocumentObjectGroupPython] Na_element019  label="Na_element : 0.102"  # scripted group (container) (typed FeaturePython)
  n = 0.001
FEATURE [App::DocumentObjectGroupPython] P_element011  label="P_element : 0.109"  # scripted group (container) (typed FeaturePython)
  n = 0.002
FEATURE [App::DocumentObjectGroupPython] S_element022  label="S_element : 0.023"  # scripted group (container) (typed FeaturePython)
  n = 0.003
FEATURE [App::DocumentObjectGroupPython] Cl_element027  label="Cl_element : 0.591"  # scripted group (container) (typed FeaturePython)
  n = 0.002
FEATURE [App::DocumentObjectGroupPython] K_element012  label="K_element : 0.018"  # scripted group (container) (typed FeaturePython)
  n = 0.002
FEATURE [App::DocumentObjectGroupPython] G4_TISSUE_SOFT_ICRP  # scripted group (container) (typed FeaturePython)
  Dunit = g/cm3
  Dvalue = 1.03
  Group = -> [H_element100,C_element110,N_element042,O_element094,Na_element019,P_element011,S_element022,Cl_element027,K_element012]
  conduct = 2
  density = 1
  expand = 3
  formula = G4_TISSUE_SOFT_ICRP
  name = G4_TISSUE_SOFT_ICRP
  specific = 4
FEATURE [App::DocumentObjectGroupPython] H_element101  label="H_element : 0.148"  # scripted group (container) (typed FeaturePython)
  n = 0.101
FEATURE [App::DocumentObjectGroupPython] C_element111  label="C_element : 0.111"  # scripted group (container) (typed FeaturePython)
  n = 0.111
FEATURE [App::DocumentObjectGroupPython] N_element043  label="N_element : 0.026"  # scripted group (container) (typed FeaturePython)
  n = 0.026
FEATURE [App::DocumentObjectGroupPython] O_element095  label="O_element : 0.762"  # scripted group (container) (typed FeaturePython)
  n = 0.762
FEATURE [App::DocumentObjectGroupPython] G4_TISSUE_SOFT_ICRU_4  label="G4_TISSUE_SOFT_ICRU-4"  # scripted group (container) (typed FeaturePython)
  Dunit = g/cm3
  Dvalue = 1
  Group = -> [H_element101,C_element111,N_element043,O_element095]
  conduct = 2
  density = 1
  expand = 3
  formula = G4_TISSUE_SOFT_ICRU-4
  name = G4_TISSUE_SOFT_ICRU-4
  specific = 4
FEATURE [App::DocumentObjectGroupPython] H_element102  label="H_element : 0.149"  # scripted group (container) (typed FeaturePython)
  n = 0.101869
FEATURE [App::DocumentObjectGroupPython] C_element112  label="C_element : 0.456"  # scripted group (container) (typed FeaturePython)
  n = 0.456179
FEATURE [App::DocumentObjectGroupPython] N_element044  label="N_element : 0.761"  # scripted group (container) (typed FeaturePython)
  n = 0.035172
FEATURE [App::DocumentObjectGroupPython] O_element096  label="O_element : 0.407"  # scripted group (container) (typed FeaturePython)
  n = 0.40678
FEATURE [App::DocumentObjectGroupPython] G4_TISSUE_METHANE  label="G4_TISSUE-METHANE"  # scripted group (container) (typed FeaturePython)
  Dunit = g/cm3
  Dvalue = 0.00106409
  Group = -> [H_element102,C_element112,N_element044,O_element096]
  conduct = 2
  density = 1
  expand = 3
  formula = G4_TISSUE-METHANE
  name = G4_TISSUE-METHANE
  specific = 4
FEATURE [App::DocumentObjectGroupPython] H_element103  label="H_element : 0.103"  # scripted group (container) (typed FeaturePython)
  n = 0.102672
FEATURE [App::DocumentObjectGroupPython] C_element113  label="C_element : 0.569"  # scripted group (container) (typed FeaturePython)
  n = 0.56894
FEATURE [App::DocumentObjectGroupPython] N_element045  label="N_element : 0.762"  # scripted group (container) (typed FeaturePython)
  n = 0.035022
FEATURE [App::DocumentObjectGroupPython] O_element097  label="O_element : 0.293"  # scripted group (container) (typed FeaturePython)
  n = 0.293366
FEATURE [App::DocumentObjectGroupPython] G4_TISSUE_PROPANE  label="G4_TISSUE-PROPANE"  # scripted group (container) (typed FeaturePython)
  Dunit = g/cm3
  Dvalue = 0.00182628
  Group = -> [H_element103,C_element113,N_element045,O_element097]
  conduct = 2
  density = 1
  expand = 3
  formula = G4_TISSUE-PROPANE
  name = G4_TISSUE-PROPANE
  specific = 4
FEATURE [App::DocumentObjectGroupPython] Ti_element003  label="Ti_element : 1"  # scripted group (container) (typed FeaturePython)
  n = 1
  ref = Ti_element
FEATURE [App::DocumentObjectGroupPython] O_element098  label="O_element : 052"  # scripted group (container) (typed FeaturePython)
  n = 2
  ref = O_element
FEATURE [App::DocumentObjectGroupPython] G4_TITANIUM_DIOXIDE  # scripted group (container) (typed FeaturePython)
  Dunit = g/cm3
  Dvalue = 4.26
  Group = -> [Ti_element003,O_element098]
  conduct = 2
  density = 1
  expand = 3
  formula = G4_TITANIUM_DIOXIDE
  name = G4_TITANIUM_DIOXIDE
  specific = 4
FEATURE [App::DocumentObjectGroupPython] C_element114  label="C_element : 061"  # scripted group (container) (typed FeaturePython)
  n = 7
  ref = C_element
FEATURE [App::DocumentObjectGroupPython] H_element104  label="H_element : 055"  # scripted group (container) (typed FeaturePython)
  n = 8
  ref = H_element
FEATURE [App::DocumentObjectGroupPython] G4_TOLUENE  # scripted group (container) (typed FeaturePython)
  Dunit = g/cm3
  Dvalue = 0.8669
  Group = -> [C_element114,H_element104]
  conduct = 2
  density = 1
  expand = 3
  formula = G4_TOLUENE
  name = G4_TOLUENE
  specific = 4
FEATURE [App::DocumentObjectGroupPython] C_element115  label="C_element : 062"  # scripted group (container) (typed FeaturePython)
  n = 2
  ref = C_element
FEATURE [App::DocumentObjectGroupPython] H_element105  label="H_element : 056"  # scripted group (container) (typed FeaturePython)
  n = 1
  ref = H_element
FEATURE [App::DocumentObjectGroupPython] Cl_element028  label="Cl_element : 014"  # scripted group (container) (typed FeaturePython)
  n = 3
  ref = Cl_element
FEATURE [App::DocumentObjectGroupPython] G4_TRICHLOROETHYLENE  # scripted group (container) (typed FeaturePython)
  Dunit = g/cm3
  Dvalue = 1.46
  Group = -> [C_element115,H_element105,Cl_element028]
  conduct = 2
  density = 1
  expand = 3
  formula = G4_TRICHLOROETHYLENE
  name = G4_TRICHLOROETHYLENE
  specific = 4
FEATURE [App::DocumentObjectGroupPython] C_element116  label="C_element : 063"  # scripted group (container) (typed FeaturePython)
  n = 6
  ref = C_element
FEATURE [App::DocumentObjectGroupPython] H_element106  label="H_element : 15"  # scripted group (container) (typed FeaturePython)
  n = 15
  ref = H_element
FEATURE [App::DocumentObjectGroupPython] O_element099  label="O_element : 053"  # scripted group (container) (typed FeaturePython)
  n = 4
  ref = O_element
FEATURE [App::DocumentObjectGroupPython] P_element012  label="P_element : 1"  # scripted group (container) (typed FeaturePython)
  n = 1
  ref = P_element
FEATURE [App::DocumentObjectGroupPython] G4_TRIETHYL_PHOSPHATE  # scripted group (container) (typed FeaturePython)
  Dunit = g/cm3
  Dvalue = 1.07
  Group = -> [C_element116,H_element106,O_element099,P_element012]
  conduct = 2
  density = 1
  expand = 3
  formula = G4_TRIETHYL_PHOSPHATE
  name = G4_TRIETHYL_PHOSPHATE
  specific = 4
FEATURE [App::DocumentObjectGroupPython] W_element003  label="W_element : 003"  # scripted group (container) (typed FeaturePython)
  n = 1
  ref = W_element
FEATURE [App::DocumentObjectGroupPython] F_element017  label="F_element : 6"  # scripted group (container) (typed FeaturePython)
  n = 6
  ref = F_element
FEATURE [App::DocumentObjectGroupPython] G4_TUNGSTEN_HEXAFLUORIDE  # scripted group (container) (typed FeaturePython)
  Dunit = g/cm3
  Dvalue = 2.4
  Group = -> [W_element003,F_element017]
  conduct = 2
  density = 1
  expand = 3
  formula = G4_TUNGSTEN_HEXAFLUORIDE
  name = G4_TUNGSTEN_HEXAFLUORIDE
  specific = 4
FEATURE [App::DocumentObjectGroupPython] U_element001  label="U_element : 1"  # scripted group (container) (typed FeaturePython)
  n = 1
  ref = U_element
FEATURE [App::DocumentObjectGroupPython] C_element117  label="C_element : 064"  # scripted group (container) (typed FeaturePython)
  n = 2
  ref = C_element
FEATURE [App::DocumentObjectGroupPython] G4_URANIUM_DICARBIDE  # scripted group (container) (typed FeaturePython)
  Dunit = g/cm3
  Dvalue = 11.28
  Group = -> [U_element001,C_element117]
  conduct = 2
  density = 1
  expand = 3
  formula = G4_URANIUM_DICARBIDE
  name = G4_URANIUM_DICARBIDE
  specific = 4
FEATURE [App::DocumentObjectGroupPython] U_element002  label="U_element : 002"  # scripted group (container) (typed FeaturePython)
  n = 1
  ref = U_element
FEATURE [App::DocumentObjectGroupPython] C_element118  label="C_element : 065"  # scripted group (container) (typed FeaturePython)
  n = 1
  ref = C_element
FEATURE [App::DocumentObjectGroupPython] G4_URANIUM_MONOCARBIDE  # scripted group (container) (typed FeaturePython)
  Dunit = g/cm3
  Dvalue = 13.63
  Group = -> [U_element002,C_element118]
  conduct = 2
  density = 1
  expand = 3
  formula = G4_URANIUM_MONOCARBIDE
  name = G4_URANIUM_MONOCARBIDE
  specific = 4
FEATURE [App::DocumentObjectGroupPython] U_element003  label="U_element : 003"  # scripted group (container) (typed FeaturePython)
  n = 1
  ref = U_element
FEATURE [App::DocumentObjectGroupPython] O_element100  label="O_element : 054"  # scripted group (container) (typed FeaturePython)
  n = 2
  ref = O_element
FEATURE [App::DocumentObjectGroupPython] G4_URANIUM_OXIDE  # scripted group (container) (typed FeaturePython)
  Dunit = g/cm3
  Dvalue = 10.96
  Group = -> [U_element003,O_element100]
  conduct = 2
  density = 1
  expand = 3
  formula = G4_URANIUM_OXIDE
  name = G4_URANIUM_OXIDE
  specific = 4
FEATURE [App::DocumentObjectGroupPython] C_element119  label="C_element : 066"  # scripted group (container) (typed FeaturePython)
  n = 1
  ref = C_element
FEATURE [App::DocumentObjectGroupPython] H_element107  label="H_element : 057"  # scripted group (container) (typed FeaturePython)
  n = 4
  ref = H_element
FEATURE [App::DocumentObjectGroupPython] N_element046  label="N_element : 019"  # scripted group (container) (typed FeaturePython)
  n = 2
  ref = N_element
FEATURE [App::DocumentObjectGroupPython] O_element101  label="O_element : 055"  # scripted group (container) (typed FeaturePython)
  n = 1
  ref = O_element
FEATURE [App::DocumentObjectGroupPython] G4_UREA  # scripted group (container) (typed FeaturePython)
  Dunit = g/cm3
  Dvalue = 1.323
  Group = -> [C_element119,H_element107,N_element046,O_element101]
  conduct = 2
  density = 1
  expand = 3
  formula = G4_UREA
  name = G4_UREA
  specific = 4
FEATURE [App::DocumentObjectGroupPython] C_element120  label="C_element : 067"  # scripted group (container) (typed FeaturePython)
  n = 5
  ref = C_element
FEATURE [App::DocumentObjectGroupPython] H_element108  label="H_element : 058"  # scripted group (container) (typed FeaturePython)
  n = 11
  ref = H_element
FEATURE [App::DocumentObjectGroupPython] N_element047  label="N_element : 020"  # scripted group (container) (typed FeaturePython)
  n = 1
  ref = N_element
FEATURE [App::DocumentObjectGroupPython] O_element102  label="O_element : 056"  # scripted group (container) (typed FeaturePython)
  n = 2
  ref = O_element
FEATURE [App::DocumentObjectGroupPython] G4_VALINE  # scripted group (container) (typed FeaturePython)
  Dunit = g/cm3
  Dvalue = 1.23
  Group = -> [C_element120,H_element108,N_element047,O_element102]
  conduct = 2
  density = 1
  expand = 3
  formula = G4_VALINE
  name = G4_VALINE
  specific = 4
FEATURE [App::DocumentObjectGroupPython] H_element109  label="H_element : 0.009"  # scripted group (container) (typed FeaturePython)
  n = 0.009417
FEATURE [App::DocumentObjectGroupPython] C_element121  label="C_element : 0.281"  # scripted group (container) (typed FeaturePython)
  n = 0.280555
FEATURE [App::DocumentObjectGroupPython] F_element018  label="F_element : 0.710"  # scripted group (container) (typed FeaturePython)
  n = 0.710028
FEATURE [App::DocumentObjectGroupPython] G4_VITON  # scripted group (container) (typed FeaturePython)
  Dunit = g/cm3
  Dvalue = 1.8
  Group = -> [H_element109,C_element121,F_element018]
  conduct = 2
  density = 1
  expand = 3
  formula = G4_VITON
  name = G4_VITON
  specific = 4
FEATURE [App::DocumentObjectGroupPython] H_element110  label="H_element : 059"  # scripted group (container) (typed FeaturePython)
  n = 2
  ref = H_element
FEATURE [App::DocumentObjectGroupPython] O_element103  label="O_element : 057"  # scripted group (container) (typed FeaturePython)
  n = 1
  ref = O_element
FEATURE [App::DocumentObjectGroupPython] G4_WATER  # scripted group (container) (typed FeaturePython)
  Dunit = g/cm3
  Dvalue = 1
  Group = -> [H_element110,O_element103]
  conduct = 2
  density = 1
  expand = 3
  formula = G4_WATER
  name = G4_WATER
  specific = 4
FEATURE [App::DocumentObjectGroupPython] H_element111  label="H_element : 060"  # scripted group (container) (typed FeaturePython)
  n = 2
  ref = H_element
FEATURE [App::DocumentObjectGroupPython] O_element104  label="O_element : 058"  # scripted group (container) (typed FeaturePython)
  n = 1
  ref = O_element
FEATURE [App::DocumentObjectGroupPython] G4_WATER_VAPOR  # scripted group (container) (typed FeaturePython)
  Dunit = g/cm3
  Dvalue = 0.000756182
  Group = -> [H_element111,O_element104]
  conduct = 2
  density = 1
  expand = 3
  formula = G4_WATER_VAPOR
  name = G4_WATER_VAPOR
  specific = 4
FEATURE [App::DocumentObjectGroupPython] C_element122  label="C_element : 068"  # scripted group (container) (typed FeaturePython)
  n = 8
  ref = C_element
FEATURE [App::DocumentObjectGroupPython] H_element112  label="H_element : 061"  # scripted group (container) (typed FeaturePython)
  n = 10
  ref = H_element
FEATURE [App::DocumentObjectGroupPython] G4_XYLENE  # scripted group (container) (typed FeaturePython)
  Dunit = g/cm3
  Dvalue = 0.87
  Group = -> [C_element122,H_element112]
  conduct = 2
  density = 1
  expand = 3
  formula = G4_XYLENE
  name = G4_XYLENE
  specific = 4
FEATURE [App::DocumentObjectGroupPython] C_element123  label="C_element : 069"  # scripted group (container) (typed FeaturePython)
  n = 1
  ref = C_element
FEATURE [App::DocumentObjectGroupPython] G4_GRAPHITE  # scripted group (container) (typed FeaturePython)
  Dunit = g/cm3
  Dvalue = 2.21
  Group = -> [C_element123]
  conduct = 2
  density = 1
  expand = 3
  formula = G4_GRAPHITE
  name = G4_GRAPHITE
  specific = 4
FEATURE [App::DocumentObjectGroupPython] NIST  # scripted group (container) (typed FeaturePython)
  Group = -> [G4_A_150_TISSUE,G4_ACETONE,G4_ACETYLENE,G4_ADENINE,G4_ADIPOSE_TISSUE_ICRP,G4_AIR,G4_ALANINE,G4_ALUMINUM_OXIDE,G4_AMBER,G4_AMMONIA,G4_ANILINE,G4_ANTHRACENE,G4_B_100_BONE,G4_BAKELITE,G4_BARIUM_FLUORIDE,G4_BARIUM_SULFATE,G4_BENZENE,G4_BERYLLIUM_OXIDE,G4_BGO,G4_BLOOD_ICRP,G4_BONE_COMPACT_ICRU,G4_BONE_CORTICAL_ICRP,G4_BORON_CARBIDE,G4_BORON_OXIDE,G4_BRAIN_ICRP,G4_BUTANE,G4_N_BUTYL_ALCOHOL,G4_C_552,+152 more]
FEATURE [App::DocumentObjectGroupPython] H_element113  label="H_element : 062"  # scripted group (container) (typed FeaturePython)
  n = 1
  ref = H_element
FEATURE [App::DocumentObjectGroupPython] G4_H  # scripted group (container) (typed FeaturePython)
  Dunit = g/cm3
  Dvalue = 8.3748e-05
  Group = -> [H_element113]
  conduct = 2
  density = 1
  expand = 3
  formula = H
  name = G4_H
  specific = 4
FEATURE [App::DocumentObjectGroupPython] He_element001  label="He_element : 1"  # scripted group (container) (typed FeaturePython)
  n = 1
  ref = He_element
FEATURE [App::DocumentObjectGroupPython] G4_He  # scripted group (container) (typed FeaturePython)
  Dunit = g/cm3
  Dvalue = 0.000166322
  Group = -> [He_element001]
  conduct = 2
  density = 1
  expand = 3
  formula = He
  name = G4_He
  specific = 4
FEATURE [App::DocumentObjectGroupPython] Li_element008  label="Li_element : 008"  # scripted group (container) (typed FeaturePython)
  n = 1
  ref = Li_element
FEATURE [App::DocumentObjectGroupPython] G4_Li  # scripted group (container) (typed FeaturePython)
  Dunit = g/cm3
  Dvalue = 0.534
  Group = -> [Li_element008]
  conduct = 2
  density = 1
  expand = 3
  formula = Li
  name = G4_Li
  specific = 4
FEATURE [App::DocumentObjectGroupPython] Be_element002  label="Be_element : 002"  # scripted group (container) (typed FeaturePython)
  n = 1
  ref = Be_element
FEATURE [App::DocumentObjectGroupPython] G4_Be  # scripted group (container) (typed FeaturePython)
  Dunit = g/cm3
  Dvalue = 1.848
  Group = -> [Be_element002]
  conduct = 2
  density = 1
  expand = 3
  formula = Be
  name = G4_Be
  specific = 4
FEATURE [App::DocumentObjectGroupPython] B_element007  label="B_element : 007"  # scripted group (container) (typed FeaturePython)
  n = 1
  ref = B_element
FEATURE [App::DocumentObjectGroupPython] G4_B  # scripted group (container) (typed FeaturePython)
  Dunit = g/cm3
  Dvalue = 2.37
  Group = -> [B_element007]
  conduct = 2
  density = 1
  expand = 3
  formula = B
  name = G4_B
  specific = 4
FEATURE [App::DocumentObjectGroupPython] C_element124  label="C_element : 070"  # scripted group (container) (typed FeaturePython)
  n = 1
  ref = C_element
FEATURE [App::DocumentObjectGroupPython] G4_C  # scripted group (container) (typed FeaturePython)
  Dunit = g/cm3
  Dvalue = 2
  Group = -> [C_element124]
  conduct = 2
  density = 1
  expand = 3
  formula = C
  name = G4_C
  specific = 4
FEATURE [App::DocumentObjectGroupPython] N_element048  label="N_element : 021"  # scripted group (container) (typed FeaturePython)
  n = 1
  ref = N_element
FEATURE [App::DocumentObjectGroupPython] G4_N  # scripted group (container) (typed FeaturePython)
  Dunit = g/cm3
  Dvalue = 0.0011652
  Group = -> [N_element048]
  conduct = 2
  density = 1
  expand = 3
  formula = N
  name = G4_N
  specific = 4
FEATURE [App::DocumentObjectGroupPython] O_element105  label="O_element : 059"  # scripted group (container) (typed FeaturePython)
  n = 1
  ref = O_element
FEATURE [App::DocumentObjectGroupPython] G4_O  # scripted group (container) (typed FeaturePython)
  Dunit = g/cm3
  Dvalue = 0.00133151
  Group = -> [O_element105]
  conduct = 2
  density = 1
  expand = 3
  formula = O
  name = G4_O
  specific = 4
FEATURE [App::DocumentObjectGroupPython] F_element019  label="F_element : 008"  # scripted group (container) (typed FeaturePython)
  n = 1
  ref = F_element
FEATURE [App::DocumentObjectGroupPython] G4_F  # scripted group (container) (typed FeaturePython)
  Dunit = g/cm3
  Dvalue = 0.00158029
  Group = -> [F_element019]
  conduct = 2
  density = 1
  expand = 3
  formula = F
  name = G4_F
  specific = 4
FEATURE [App::DocumentObjectGroupPython] Ne_element001  label="Ne_element : 1"  # scripted group (container) (typed FeaturePython)
  n = 1
  ref = Ne_element
FEATURE [App::DocumentObjectGroupPython] G4_Ne  # scripted group (container) (typed FeaturePython)
  Dunit = g/cm3
  Dvalue = 0.000838505
  Group = -> [Ne_element001]
  conduct = 2
  density = 1
  expand = 3
  formula = Ne
  name = G4_Ne
  specific = 4
FEATURE [App::DocumentObjectGroupPython] Na_element020  label="Na_element : 005"  # scripted group (container) (typed FeaturePython)
  n = 1
  ref = Na_element
FEATURE [App::DocumentObjectGroupPython] G4_Na  # scripted group (container) (typed FeaturePython)
  Dunit = g/cm3
  Dvalue = 0.971
  Group = -> [Na_element020]
  conduct = 2
  density = 1
  expand = 3
  formula = Na
  name = G4_Na
  specific = 4
FEATURE [App::DocumentObjectGroupPython] Mg_element011  label="Mg_element : 005"  # scripted group (container) (typed FeaturePython)
  n = 1
  ref = Mg_element
FEATURE [App::DocumentObjectGroupPython] G4_Mg  # scripted group (container) (typed FeaturePython)
  Dunit = g/cm3
  Dvalue = 1.74
  Group = -> [Mg_element011]
  conduct = 2
  density = 1
  expand = 3
  formula = Mg
  name = G4_Mg
  specific = 4
FEATURE [App::DocumentObjectGroupPython] Al_element004  label="Al_element : 1"  # scripted group (container) (typed FeaturePython)
  n = 1
  ref = Al_element
FEATURE [App::DocumentObjectGroupPython] G4_Al  # scripted group (container) (typed FeaturePython)
  Dunit = g/cm3
  Dvalue = 2.699
  Group = -> [Al_element004]
  conduct = 2
  density = 1
  expand = 3
  formula = Al
  name = G4_Al
  specific = 4
FEATURE [App::DocumentObjectGroupPython] Si_element007  label="Si_element : 002"  # scripted group (container) (typed FeaturePython)
  n = 1
  ref = Si_element
FEATURE [App::DocumentObjectGroupPython] G4_Si  # scripted group (container) (typed FeaturePython)
  Dunit = g/cm3
  Dvalue = 2.33
  Group = -> [Si_element007]
  conduct = 2
  density = 1
  expand = 3
  formula = Si
  name = G4_Si
  specific = 4
FEATURE [App::DocumentObjectGroupPython] P_element013  label="P_element : 002"  # scripted group (container) (typed FeaturePython)
  n = 1
  ref = P_element
FEATURE [App::DocumentObjectGroupPython] G4_P  # scripted group (container) (typed FeaturePython)
  Dunit = g/cm3
  Dvalue = 2.2
  Group = -> [P_element013]
  conduct = 2
  density = 1
  expand = 3
  formula = P
  name = G4_P
  specific = 4
FEATURE [App::DocumentObjectGroupPython] S_element023  label="S_element : 007"  # scripted group (container) (typed FeaturePython)
  n = 1
  ref = S_element
FEATURE [App::DocumentObjectGroupPython] G4_S  # scripted group (container) (typed FeaturePython)
  Dunit = g/cm3
  Dvalue = 2
  Group = -> [S_element023]
  conduct = 2
  density = 1
  expand = 3
  formula = S
  name = G4_S
  specific = 4
FEATURE [App::DocumentObjectGroupPython] Cl_element029  label="Cl_element : 015"  # scripted group (container) (typed FeaturePython)
  n = 1
  ref = Cl_element
FEATURE [App::DocumentObjectGroupPython] G4_Cl  # scripted group (container) (typed FeaturePython)
  Dunit = g/cm3
  Dvalue = 0.00299473
  Group = -> [Cl_element029]
  conduct = 2
  density = 1
  expand = 3
  formula = Cl
  name = G4_Cl
  specific = 4
FEATURE [App::DocumentObjectGroupPython] Ar_element002  label="Ar_element : 1"  # scripted group (container) (typed FeaturePython)
  n = 1
  ref = Ar_element
FEATURE [App::DocumentObjectGroupPython] G4_Ar  # scripted group (container) (typed FeaturePython)
  Dunit = g/cm3
  Dvalue = 0.00166201
  Group = -> [Ar_element002]
  conduct = 2
  density = 1
  expand = 3
  formula = Ar
  name = G4_Ar
  specific = 4
FEATURE [App::DocumentObjectGroupPython] K_element013  label="K_element : 003"  # scripted group (container) (typed FeaturePython)
  n = 1
  ref = K_element
FEATURE [App::DocumentObjectGroupPython] G4_K  # scripted group (container) (typed FeaturePython)
  Dunit = g/cm3
  Dvalue = 0.862
  Group = -> [K_element013]
  conduct = 2
  density = 1
  expand = 3
  formula = K
  name = G4_K
  specific = 4
FEATURE [App::DocumentObjectGroupPython] Ca_element014  label="Ca_element : 007"  # scripted group (container) (typed FeaturePython)
  n = 1
  ref = Ca_element
FEATURE [App::DocumentObjectGroupPython] G4_Ca  # scripted group (container) (typed FeaturePython)
  Dunit = g/cm3
  Dvalue = 1.55
  Group = -> [Ca_element014]
  conduct = 2
  density = 1
  expand = 3
  formula = Ca
  name = G4_Ca
  specific = 4
FEATURE [App::DocumentObjectGroupPython] Sc_element001  label="Sc_element : 1"  # scripted group (container) (typed FeaturePython)
  n = 1
  ref = Sc_element
FEATURE [App::DocumentObjectGroupPython] G4_Sc  # scripted group (container) (typed FeaturePython)
  Dunit = g/cm3
  Dvalue = 2.989
  Group = -> [Sc_element001]
  conduct = 2
  density = 1
  expand = 3
  formula = Sc
  name = G4_Sc
  specific = 4
FEATURE [App::DocumentObjectGroupPython] Ti_element004  label="Ti_element : 002"  # scripted group (container) (typed FeaturePython)
  n = 1
  ref = Ti_element
FEATURE [App::DocumentObjectGroupPython] G4_Ti  # scripted group (container) (typed FeaturePython)
  Dunit = g/cm3
  Dvalue = 4.54
  Group = -> [Ti_element004]
  conduct = 2
  density = 1
  expand = 3
  formula = Ti
  name = G4_Ti
  specific = 4
FEATURE [App::DocumentObjectGroupPython] V_element001  label="V_element : 1"  # scripted group (container) (typed FeaturePython)
  n = 1
  ref = V_element
FEATURE [App::DocumentObjectGroupPython] G4_V  # scripted group (container) (typed FeaturePython)
  Dunit = g/cm3
  Dvalue = 6.11
  Group = -> [V_element001]
  conduct = 2
  density = 1
  expand = 3
  formula = V
  name = G4_V
  specific = 4
FEATURE [App::DocumentObjectGroupPython] Cr_element001  label="Cr_element : 1"  # scripted group (container) (typed FeaturePython)
  n = 1
  ref = Cr_element
FEATURE [App::DocumentObjectGroupPython] G4_Cr  # scripted group (container) (typed FeaturePython)
  Dunit = g/cm3
  Dvalue = 7.18
  Group = -> [Cr_element001]
  conduct = 2
  density = 1
  expand = 3
  formula = Cr
  name = G4_Cr
  specific = 4
FEATURE [App::DocumentObjectGroupPython] Mn_element001  label="Mn_element : 1"  # scripted group (container) (typed FeaturePython)
  n = 1
  ref = Mn_element
FEATURE [App::DocumentObjectGroupPython] G4_Mn  # scripted group (container) (typed FeaturePython)
  Dunit = g/cm3
  Dvalue = 7.44
  Group = -> [Mn_element001]
  conduct = 2
  density = 1
  expand = 3
  formula = Mn
  name = G4_Mn
  specific = 4
FEATURE [App::DocumentObjectGroupPython] Fe_element007  label="Fe_element : 004"  # scripted group (container) (typed FeaturePython)
  n = 1
  ref = Fe_element
FEATURE [App::DocumentObjectGroupPython] G4_Fe  # scripted group (container) (typed FeaturePython)
  Dunit = g/cm3
  Dvalue = 7.874
  Group = -> [Fe_element007]
  conduct = 2
  density = 1
  expand = 3
  formula = Fe
  name = G4_Fe
  specific = 4
FEATURE [App::DocumentObjectGroupPython] Co_element001  label="Co_element : 1"  # scripted group (container) (typed FeaturePython)
  n = 1
  ref = Co_element
FEATURE [App::DocumentObjectGroupPython] G4_Co  # scripted group (container) (typed FeaturePython)
  Dunit = g/cm3
  Dvalue = 8.9
  Group = -> [Co_element001]
  conduct = 2
  density = 1
  expand = 3
  formula = Co
  name = G4_Co
  specific = 4
FEATURE [App::DocumentObjectGroupPython] Ni_element001  label="Ni_element : 1"  # scripted group (container) (typed FeaturePython)
  n = 1
  ref = Ni_element
FEATURE [App::DocumentObjectGroupPython] G4_Ni  # scripted group (container) (typed FeaturePython)
  Dunit = g/cm3
  Dvalue = 8.902
  Group = -> [Ni_element001]
  conduct = 2
  density = 1
  expand = 3
  formula = Ni
  name = G4_Ni
  specific = 4
FEATURE [App::DocumentObjectGroupPython] Cu_element001  label="Cu_element : 1"  # scripted group (container) (typed FeaturePython)
  n = 1
  ref = Cu_element
FEATURE [App::DocumentObjectGroupPython] G4_Cu  # scripted group (container) (typed FeaturePython)
  Dunit = g/cm3
  Dvalue = 8.96
  Group = -> [Cu_element001]
  conduct = 2
  density = 1
  expand = 3
  formula = Cu
  name = G4_Cu
  specific = 4
FEATURE [App::DocumentObjectGroupPython] Zn_element001  label="Zn_element : 1"  # scripted group (container) (typed FeaturePython)
  n = 1
  ref = Zn_element
FEATURE [App::DocumentObjectGroupPython] G4_Zn  # scripted group (container) (typed FeaturePython)
  Dunit = g/cm3
  Dvalue = 7.133
  Group = -> [Zn_element001]
  conduct = 2
  density = 1
  expand = 3
  formula = Zn
  name = G4_Zn
  specific = 4
FEATURE [App::DocumentObjectGroupPython] Ga_element002  label="Ga_element : 002"  # scripted group (container) (typed FeaturePython)
  n = 1
  ref = Ga_element
FEATURE [App::DocumentObjectGroupPython] G4_Ga  # scripted group (container) (typed FeaturePython)
  Dunit = g/cm3
  Dvalue = 5.904
  Group = -> [Ga_element002]
  conduct = 2
  density = 1
  expand = 3
  formula = Ga
  name = G4_Ga
  specific = 4
FEATURE [App::DocumentObjectGroupPython] Ge_element002  label="Ge_element : 1"  # scripted group (container) (typed FeaturePython)
  n = 1
  ref = Ge_element
FEATURE [App::DocumentObjectGroupPython] G4_Ge  # scripted group (container) (typed FeaturePython)
  Dunit = g/cm3
  Dvalue = 5.323
  Group = -> [Ge_element002]
  conduct = 2
  density = 1
  expand = 3
  formula = Ge
  name = G4_Ge
  specific = 4
FEATURE [App::DocumentObjectGroupPython] As_element003  label="As_element : 002"  # scripted group (container) (typed FeaturePython)
  n = 1
  ref = As_element
FEATURE [App::DocumentObjectGroupPython] G4_As  # scripted group (container) (typed FeaturePython)
  Dunit = g/cm3
  Dvalue = 5.73
  Group = -> [As_element003]
  conduct = 2
  density = 1
  expand = 3
  formula = As
  name = G4_As
  specific = 4
FEATURE [App::DocumentObjectGroupPython] Se_element001  label="Se_element : 1"  # scripted group (container) (typed FeaturePython)
  n = 1
  ref = Se_element
FEATURE [App::DocumentObjectGroupPython] G4_Se  # scripted group (container) (typed FeaturePython)
  Dunit = g/cm3
  Dvalue = 4.5
  Group = -> [Se_element001]
  conduct = 2
  density = 1
  expand = 3
  formula = Se
  name = G4_Se
  specific = 4
FEATURE [App::DocumentObjectGroupPython] Br_element007  label="Br_element : 004"  # scripted group (container) (typed FeaturePython)
  n = 1
  ref = Br_element
FEATURE [App::DocumentObjectGroupPython] G4_Br  # scripted group (container) (typed FeaturePython)
  Dunit = g/cm3
  Dvalue = 0.0070721
  Group = -> [Br_element007]
  conduct = 2
  density = 1
  expand = 3
  formula = Br
  name = G4_Br
  specific = 4
FEATURE [App::DocumentObjectGroupPython] Kr_element001  label="Kr_element : 1"  # scripted group (container) (typed FeaturePython)
  n = 1
  ref = Kr_element
FEATURE [App::DocumentObjectGroupPython] G4_Kr  # scripted group (container) (typed FeaturePython)
  Dunit = g/cm3
  Dvalue = 0.00347832
  Group = -> [Kr_element001]
  conduct = 2
  density = 1
  expand = 3
  formula = Kr
  name = G4_Kr
  specific = 4
FEATURE [App::DocumentObjectGroupPython] Rb_element001  label="Rb_element : 1"  # scripted group (container) (typed FeaturePython)
  n = 1
  ref = Rb_element
FEATURE [App::DocumentObjectGroupPython] G4_Rb  # scripted group (container) (typed FeaturePython)
  Dunit = g/cm3
  Dvalue = 1.532
  Group = -> [Rb_element001]
  conduct = 2
  density = 1
  expand = 3
  formula = Rb
  name = G4_Rb
  specific = 4
FEATURE [App::DocumentObjectGroupPython] Sr_element001  label="Sr_element : 1"  # scripted group (container) (typed FeaturePython)
  n = 1
  ref = Sr_element
FEATURE [App::DocumentObjectGroupPython] G4_Sr  # scripted group (container) (typed FeaturePython)
  Dunit = g/cm3
  Dvalue = 2.54
  Group = -> [Sr_element001]
  conduct = 2
  density = 1
  expand = 3
  formula = Sr
  name = G4_Sr
  specific = 4
FEATURE [App::DocumentObjectGroupPython] Y_element001  label="Y_element : 1"  # scripted group (container) (typed FeaturePython)
  n = 1
  ref = Y_element
FEATURE [App::DocumentObjectGroupPython] G4_Y  # scripted group (container) (typed FeaturePython)
  Dunit = g/cm3
  Dvalue = 4.469
  Group = -> [Y_element001]
  conduct = 2
  density = 1
  expand = 3
  formula = Y
  name = G4_Y
  specific = 4
FEATURE [App::DocumentObjectGroupPython] Zr_element001  label="Zr_element : 1"  # scripted group (container) (typed FeaturePython)
  n = 1
  ref = Zr_element
FEATURE [App::DocumentObjectGroupPython] G4_Zr  # scripted group (container) (typed FeaturePython)
  Dunit = g/cm3
  Dvalue = 6.506
  Group = -> [Zr_element001]
  conduct = 2
  density = 1
  expand = 3
  formula = Zr
  name = G4_Zr
  specific = 4
FEATURE [App::DocumentObjectGroupPython] Nb_element001  label="Nb_element : 1"  # scripted group (container) (typed FeaturePython)
  n = 1
  ref = Nb_element
FEATURE [App::DocumentObjectGroupPython] G4_Nb  # scripted group (container) (typed FeaturePython)
  Dunit = g/cm3
  Dvalue = 8.57
  Group = -> [Nb_element001]
  conduct = 2
  density = 1
  expand = 3
  formula = Nb
  name = G4_Nb
  specific = 4
FEATURE [App::DocumentObjectGroupPython] Mo_element001  label="Mo_element : 1"  # scripted group (container) (typed FeaturePython)
  n = 1
  ref = Mo_element
FEATURE [App::DocumentObjectGroupPython] G4_Mo  # scripted group (container) (typed FeaturePython)
  Dunit = g/cm3
  Dvalue = 10.22
  Group = -> [Mo_element001]
  conduct = 2
  density = 1
  expand = 3
  formula = Mo
  name = G4_Mo
  specific = 4
FEATURE [App::DocumentObjectGroupPython] Tc_element001  label="Tc_element : 1"  # scripted group (container) (typed FeaturePython)
  n = 1
  ref = Tc_element
FEATURE [App::DocumentObjectGroupPython] G4_Tc  # scripted group (container) (typed FeaturePython)
  Dunit = g/cm3
  Dvalue = 11.5
  Group = -> [Tc_element001]
  conduct = 2
  density = 1
  expand = 3
  formula = Tc
  name = G4_Tc
  specific = 4
FEATURE [App::DocumentObjectGroupPython] Ru_element001  label="Ru_element : 1"  # scripted group (container) (typed FeaturePython)
  n = 1
  ref = Ru_element
FEATURE [App::DocumentObjectGroupPython] G4_Ru  # scripted group (container) (typed FeaturePython)
  Dunit = g/cm3
  Dvalue = 12.41
  Group = -> [Ru_element001]
  conduct = 2
  density = 1
  expand = 3
  formula = Ru
  name = G4_Ru
  specific = 4
FEATURE [App::DocumentObjectGroupPython] Rh_element001  label="Rh_element : 1"  # scripted group (container) (typed FeaturePython)
  n = 1
  ref = Rh_element
FEATURE [App::DocumentObjectGroupPython] G4_Rh  # scripted group (container) (typed FeaturePython)
  Dunit = g/cm3
  Dvalue = 12.41
  Group = -> [Rh_element001]
  conduct = 2
  density = 1
  expand = 3
  formula = Rh
  name = G4_Rh
  specific = 4
FEATURE [App::DocumentObjectGroupPython] Pd_element001  label="Pd_element : 1"  # scripted group (container) (typed FeaturePython)
  n = 1
  ref = Pd_element
FEATURE [App::DocumentObjectGroupPython] G4_Pd  # scripted group (container) (typed FeaturePython)
  Dunit = g/cm3
  Dvalue = 12.02
  Group = -> [Pd_element001]
  conduct = 2
  density = 1
  expand = 3
  formula = Pd
  name = G4_Pd
  specific = 4
FEATURE [App::DocumentObjectGroupPython] Ag_element006  label="Ag_element : 004"  # scripted group (container) (typed FeaturePython)
  n = 1
  ref = Ag_element
FEATURE [App::DocumentObjectGroupPython] G4_Ag  # scripted group (container) (typed FeaturePython)
  Dunit = g/cm3
  Dvalue = 10.5
  Group = -> [Ag_element006]
  conduct = 2
  density = 1
  expand = 3
  formula = Ag
  name = G4_Ag
  specific = 4
FEATURE [App::DocumentObjectGroupPython] Cd_element003  label="Cd_element : 003"  # scripted group (container) (typed FeaturePython)
  n = 1
  ref = Cd_element
FEATURE [App::DocumentObjectGroupPython] G4_Cd  # scripted group (container) (typed FeaturePython)
  Dunit = g/cm3
  Dvalue = 8.65
  Group = -> [Cd_element003]
  conduct = 2
  density = 1
  expand = 3
  formula = Cd
  name = G4_Cd
  specific = 4
FEATURE [App::DocumentObjectGroupPython] In_element001  label="In_element : 1"  # scripted group (container) (typed FeaturePython)
  n = 1
  ref = In_element
FEATURE [App::DocumentObjectGroupPython] G4_In  # scripted group (container) (typed FeaturePython)
  Dunit = g/cm3
  Dvalue = 7.31
  Group = -> [In_element001]
  conduct = 2
  density = 1
  expand = 3
  formula = In
  name = G4_In
  specific = 4
FEATURE [App::DocumentObjectGroupPython] Sn_element001  label="Sn_element : 1"  # scripted group (container) (typed FeaturePython)
  n = 1
  ref = Sn_element
FEATURE [App::DocumentObjectGroupPython] G4_Sn  # scripted group (container) (typed FeaturePython)
  Dunit = g/cm3
  Dvalue = 7.31
  Group = -> [Sn_element001]
  conduct = 2
  density = 1
  expand = 3
  formula = Sn
  name = G4_Sn
  specific = 4
FEATURE [App::DocumentObjectGroupPython] Sb_element001  label="Sb_element : 1"  # scripted group (container) (typed FeaturePython)
  n = 1
  ref = Sb_element
FEATURE [App::DocumentObjectGroupPython] G4_Sb  # scripted group (container) (typed FeaturePython)
  Dunit = g/cm3
  Dvalue = 6.691
  Group = -> [Sb_element001]
  conduct = 2
  density = 1
  expand = 3
  formula = Sb
  name = G4_Sb
  specific = 4
FEATURE [App::DocumentObjectGroupPython] Te_element002  label="Te_element : 002"  # scripted group (container) (typed FeaturePython)
  n = 1
  ref = Te_element
FEATURE [App::DocumentObjectGroupPython] G4_Te  # scripted group (container) (typed FeaturePython)
  Dunit = g/cm3
  Dvalue = 6.24
  Group = -> [Te_element002]
  conduct = 2
  density = 1
  expand = 3
  formula = Te
  name = G4_Te
  specific = 4
FEATURE [App::DocumentObjectGroupPython] I_element010  label="I_element : 006"  # scripted group (container) (typed FeaturePython)
  n = 1
  ref = I_element
FEATURE [App::DocumentObjectGroupPython] G4_I  # scripted group (container) (typed FeaturePython)
  Dunit = g/cm3
  Dvalue = 4.93
  Group = -> [I_element010]
  conduct = 2
  density = 1
  expand = 3
  formula = I
  name = G4_I
  specific = 4
FEATURE [App::DocumentObjectGroupPython] Xe_element001  label="Xe_element : 1"  # scripted group (container) (typed FeaturePython)
  n = 1
  ref = Xe_element
FEATURE [App::DocumentObjectGroupPython] G4_Xe  # scripted group (container) (typed FeaturePython)
  Dunit = g/cm3
  Dvalue = 0.00548536
  Group = -> [Xe_element001]
  conduct = 2
  density = 1
  expand = 3
  formula = Xe
  name = G4_Xe
  specific = 4
FEATURE [App::DocumentObjectGroupPython] Cs_element003  label="Cs_element : 003"  # scripted group (container) (typed FeaturePython)
  n = 1
  ref = Cs_element
FEATURE [App::DocumentObjectGroupPython] G4_Cs  # scripted group (container) (typed FeaturePython)
  Dunit = g/cm3
  Dvalue = 1.873
  Group = -> [Cs_element003]
  conduct = 2
  density = 1
  expand = 3
  formula = Cs
  name = G4_Cs
  specific = 4
FEATURE [App::DocumentObjectGroupPython] Ba_element003  label="Ba_element : 003"  # scripted group (container) (typed FeaturePython)
  n = 1
  ref = Ba_element
FEATURE [App::DocumentObjectGroupPython] G4_Ba  # scripted group (container) (typed FeaturePython)
  Dunit = g/cm3
  Dvalue = 3.5
  Group = -> [Ba_element003]
  conduct = 2
  density = 1
  expand = 3
  formula = Ba
  name = G4_Ba
  specific = 4
FEATURE [App::DocumentObjectGroupPython] La_element003  label="La_element : 003"  # scripted group (container) (typed FeaturePython)
  n = 1
  ref = La_element
FEATURE [App::DocumentObjectGroupPython] G4_La  # scripted group (container) (typed FeaturePython)
  Dunit = g/cm3
  Dvalue = 6.154
  Group = -> [La_element003]
  conduct = 2
  density = 1
  expand = 3
  formula = La
  name = G4_La
  specific = 4
FEATURE [App::DocumentObjectGroupPython] Ce_element002  label="Ce_element : 1"  # scripted group (container) (typed FeaturePython)
  n = 1
  ref = Ce_element
FEATURE [App::DocumentObjectGroupPython] G4_Ce  # scripted group (container) (typed FeaturePython)
  Dunit = g/cm3
  Dvalue = 6.657
  Group = -> [Ce_element002]
  conduct = 2
  density = 1
  expand = 3
  formula = Ce
  name = G4_Ce
  specific = 4
FEATURE [App::DocumentObjectGroupPython] Pr_element001  label="Pr_element : 1"  # scripted group (container) (typed FeaturePython)
  n = 1
  ref = Pr_element
FEATURE [App::DocumentObjectGroupPython] G4_Pr  # scripted group (container) (typed FeaturePython)
  Dunit = g/cm3
  Dvalue = 6.71
  Group = -> [Pr_element001]
  conduct = 2
  density = 1
  expand = 3
  formula = Pr
  name = G4_Pr
  specific = 4
FEATURE [App::DocumentObjectGroupPython] Nd_element001  label="Nd_element : 1"  # scripted group (container) (typed FeaturePython)
  n = 1
  ref = Nd_element
FEATURE [App::DocumentObjectGroupPython] G4_Nd  # scripted group (container) (typed FeaturePython)
  Dunit = g/cm3
  Dvalue = 6.9
  Group = -> [Nd_element001]
  conduct = 2
  density = 1
  expand = 3
  formula = Nd
  name = G4_Nd
  specific = 4
FEATURE [App::DocumentObjectGroupPython] Pm_element001  label="Pm_element : 1"  # scripted group (container) (typed FeaturePython)
  n = 1
  ref = Pm_element
FEATURE [App::DocumentObjectGroupPython] G4_Pm  # scripted group (container) (typed FeaturePython)
  Dunit = g/cm3
  Dvalue = 7.22
  Group = -> [Pm_element001]
  conduct = 2
  density = 1
  expand = 3
  formula = Pm
  name = G4_Pm
  specific = 4
FEATURE [App::DocumentObjectGroupPython] Sm_element001  label="Sm_element : 1"  # scripted group (container) (typed FeaturePython)
  n = 1
  ref = Sm_element
FEATURE [App::DocumentObjectGroupPython] G4_Sm  # scripted group (container) (typed FeaturePython)
  Dunit = g/cm3
  Dvalue = 7.46
  Group = -> [Sm_element001]
  conduct = 2
  density = 1
  expand = 3
  formula = Sm
  name = G4_Sm
  specific = 4
FEATURE [App::DocumentObjectGroupPython] Eu_element001  label="Eu_element : 1"  # scripted group (container) (typed FeaturePython)
  n = 1
  ref = Eu_element
FEATURE [App::DocumentObjectGroupPython] G4_Eu  # scripted group (container) (typed FeaturePython)
  Dunit = g/cm3
  Dvalue = 5.243
  Group = -> [Eu_element001]
  conduct = 2
  density = 1
  expand = 3
  formula = Eu
  name = G4_Eu
  specific = 4
FEATURE [App::DocumentObjectGroupPython] Gd_element002  label="Gd_element : 1"  # scripted group (container) (typed FeaturePython)
  n = 1
  ref = Gd_element
FEATURE [App::DocumentObjectGroupPython] G4_Gd  # scripted group (container) (typed FeaturePython)
  Dunit = g/cm3
  Dvalue = 7.9004
  Group = -> [Gd_element002]
  conduct = 2
  density = 1
  expand = 3
  formula = Gd
  name = G4_Gd
  specific = 4
FEATURE [App::DocumentObjectGroupPython] Tb_element001  label="Tb_element : 1"  # scripted group (container) (typed FeaturePython)
  n = 1
  ref = Tb_element
FEATURE [App::DocumentObjectGroupPython] G4_Tb  # scripted group (container) (typed FeaturePython)
  Dunit = g/cm3
  Dvalue = 8.229
  Group = -> [Tb_element001]
  conduct = 2
  density = 1
  expand = 3
  formula = Tb
  name = G4_Tb
  specific = 4
FEATURE [App::DocumentObjectGroupPython] Dy_element001  label="Dy_element : 1"  # scripted group (container) (typed FeaturePython)
  n = 1
  ref = Dy_element
FEATURE [App::DocumentObjectGroupPython] G4_Dy  # scripted group (container) (typed FeaturePython)
  Dunit = g/cm3
  Dvalue = 8.55
  Group = -> [Dy_element001]
  conduct = 2
  density = 1
  expand = 3
  formula = Dy
  name = G4_Dy
  specific = 4
FEATURE [App::DocumentObjectGroupPython] Ho_element001  label="Ho_element : 1"  # scripted group (container) (typed FeaturePython)
  n = 1
  ref = Ho_element
FEATURE [App::DocumentObjectGroupPython] G4_Ho  # scripted group (container) (typed FeaturePython)
  Dunit = g/cm3
  Dvalue = 8.795
  Group = -> [Ho_element001]
  conduct = 2
  density = 1
  expand = 3
  formula = Ho
  name = G4_Ho
  specific = 4
FEATURE [App::DocumentObjectGroupPython] Er_element001  label="Er_element : 1"  # scripted group (container) (typed FeaturePython)
  n = 1
  ref = Er_element
FEATURE [App::DocumentObjectGroupPython] G4_Er  # scripted group (container) (typed FeaturePython)
  Dunit = g/cm3
  Dvalue = 9.066
  Group = -> [Er_element001]
  conduct = 2
  density = 1
  expand = 3
  formula = Er
  name = G4_Er
  specific = 4
FEATURE [App::DocumentObjectGroupPython] Tm_element001  label="Tm_element : 1"  # scripted group (container) (typed FeaturePython)
  n = 1
  ref = Tm_element
FEATURE [App::DocumentObjectGroupPython] G4_Tm  # scripted group (container) (typed FeaturePython)
  Dunit = g/cm3
  Dvalue = 9.321
  Group = -> [Tm_element001]
  conduct = 2
  density = 1
  expand = 3
  formula = Tm
  name = G4_Tm
  specific = 4
FEATURE [App::DocumentObjectGroupPython] Yb_element001  label="Yb_element : 1"  # scripted group (container) (typed FeaturePython)
  n = 1
  ref = Yb_element
FEATURE [App::DocumentObjectGroupPython] G4_Yb  # scripted group (container) (typed FeaturePython)
  Dunit = g/cm3
  Dvalue = 6.73
  Group = -> [Yb_element001]
  conduct = 2
  density = 1
  expand = 3
  formula = Yb
  name = G4_Yb
  specific = 4
FEATURE [App::DocumentObjectGroupPython] Lu_element001  label="Lu_element : 1"  # scripted group (container) (typed FeaturePython)
  n = 1
  ref = Lu_element
FEATURE [App::DocumentObjectGroupPython] G4_Lu  # scripted group (container) (typed FeaturePython)
  Dunit = g/cm3
  Dvalue = 9.84
  Group = -> [Lu_element001]
  conduct = 2
  density = 1
  expand = 3
  formula = Lu
  name = G4_Lu
  specific = 4
FEATURE [App::DocumentObjectGroupPython] Hf_element001  label="Hf_element : 1"  # scripted group (container) (typed FeaturePython)
  n = 1
  ref = Hf_element
FEATURE [App::DocumentObjectGroupPython] G4_Hf  # scripted group (container) (typed FeaturePython)
  Dunit = g/cm3
  Dvalue = 13.31
  Group = -> [Hf_element001]
  conduct = 2
  density = 1
  expand = 3
  formula = Hf
  name = G4_Hf
  specific = 4
FEATURE [App::DocumentObjectGroupPython] Ta_element001  label="Ta_element : 1"  # scripted group (container) (typed FeaturePython)
  n = 1
  ref = Ta_element
FEATURE [App::DocumentObjectGroupPython] G4_Ta  # scripted group (container) (typed FeaturePython)
  Dunit = g/cm3
  Dvalue = 16.654
  Group = -> [Ta_element001]
  conduct = 2
  density = 1
  expand = 3
  formula = Ta
  name = G4_Ta
  specific = 4
FEATURE [App::DocumentObjectGroupPython] W_element004  label="W_element : 004"  # scripted group (container) (typed FeaturePython)
  n = 1
  ref = W_element
FEATURE [App::DocumentObjectGroupPython] G4_W  # scripted group (container) (typed FeaturePython)
  Dunit = g/cm3
  Dvalue = 19.3
  Group = -> [W_element004]
  conduct = 2
  density = 1
  expand = 3
  formula = W
  name = G4_W
  specific = 4
FEATURE [App::DocumentObjectGroupPython] Re_element001  label="Re_element : 1"  # scripted group (container) (typed FeaturePython)
  n = 1
  ref = Re_element
FEATURE [App::DocumentObjectGroupPython] G4_Re  # scripted group (container) (typed FeaturePython)
  Dunit = g/cm3
  Dvalue = 21.02
  Group = -> [Re_element001]
  conduct = 2
  density = 1
  expand = 3
  formula = Re
  name = G4_Re
  specific = 4
FEATURE [App::DocumentObjectGroupPython] Os_element001  label="Os_element : 1"  # scripted group (container) (typed FeaturePython)
  n = 1
  ref = Os_element
FEATURE [App::DocumentObjectGroupPython] G4_Os  # scripted group (container) (typed FeaturePython)
  Dunit = g/cm3
  Dvalue = 22.57
  Group = -> [Os_element001]
  conduct = 2
  density = 1
  expand = 3
  formula = Os
  name = G4_Os
  specific = 4
FEATURE [App::DocumentObjectGroupPython] Ir_element001  label="Ir_element : 1"  # scripted group (container) (typed FeaturePython)
  n = 1
  ref = Ir_element
FEATURE [App::DocumentObjectGroupPython] G4_Ir  # scripted group (container) (typed FeaturePython)
  Dunit = g/cm3
  Dvalue = 22.42
  Group = -> [Ir_element001]
  conduct = 2
  density = 1
  expand = 3
  formula = Ir
  name = G4_Ir
  specific = 4
FEATURE [App::DocumentObjectGroupPython] Pt_element001  label="Pt_element : 1"  # scripted group (container) (typed FeaturePython)
  n = 1
  ref = Pt_element
FEATURE [App::DocumentObjectGroupPython] G4_Pt  # scripted group (container) (typed FeaturePython)
  Dunit = g/cm3
  Dvalue = 21.45
  Group = -> [Pt_element001]
  conduct = 2
  density = 1
  expand = 3
  formula = Pt
  name = G4_Pt
  specific = 4
FEATURE [App::DocumentObjectGroupPython] Au_element001  label="Au_element : 1"  # scripted group (container) (typed FeaturePython)
  n = 1
  ref = Au_element
FEATURE [App::DocumentObjectGroupPython] G4_Au  # scripted group (container) (typed FeaturePython)
  Dunit = g/cm3
  Dvalue = 19.32
  Group = -> [Au_element001]
  conduct = 2
  density = 1
  expand = 3
  formula = Au
  name = G4_Au
  specific = 4
FEATURE [App::DocumentObjectGroupPython] Hg_element002  label="Hg_element : 002"  # scripted group (container) (typed FeaturePython)
  n = 1
  ref = Hg_element
FEATURE [App::DocumentObjectGroupPython] G4_Hg  # scripted group (container) (typed FeaturePython)
  Dunit = g/cm3
  Dvalue = 13.546
  Group = -> [Hg_element002]
  conduct = 2
  density = 1
  expand = 3
  formula = Hg
  name = G4_Hg
  specific = 4
FEATURE [App::DocumentObjectGroupPython] Tl_element002  label="Tl_element : 002"  # scripted group (container) (typed FeaturePython)
  n = 1
  ref = Tl_element
FEATURE [App::DocumentObjectGroupPython] G4_Tl  # scripted group (container) (typed FeaturePython)
  Dunit = g/cm3
  Dvalue = 11.72
  Group = -> [Tl_element002]
  conduct = 2
  density = 1
  expand = 3
  formula = Tl
  name = G4_Tl
  specific = 4
FEATURE [App::DocumentObjectGroupPython] Pb_element003  label="Pb_element : 1"  # scripted group (container) (typed FeaturePython)
  n = 1
  ref = Pb_element
FEATURE [App::DocumentObjectGroupPython] G4_Pb  # scripted group (container) (typed FeaturePython)
  Dunit = g/cm3
  Dvalue = 11.35
  Group = -> [Pb_element003]
  conduct = 2
  density = 1
  expand = 3
  formula = Pb
  name = G4_Pb
  specific = 4
FEATURE [App::DocumentObjectGroupPython] Bi_element002  label="Bi_element : 1"  # scripted group (container) (typed FeaturePython)
  n = 1
  ref = Bi_element
FEATURE [App::DocumentObjectGroupPython] G4_Bi  # scripted group (container) (typed FeaturePython)
  Dunit = g/cm3
  Dvalue = 9.747
  Group = -> [Bi_element002]
  conduct = 2
  density = 1
  expand = 3
  formula = Bi
  name = G4_Bi
  specific = 4
FEATURE [App::DocumentObjectGroupPython] Po_element001  label="Po_element : 1"  # scripted group (container) (typed FeaturePython)
  n = 1
  ref = Po_element
FEATURE [App::DocumentObjectGroupPython] G4_Po  # scripted group (container) (typed FeaturePython)
  Dunit = g/cm3
  Dvalue = 9.32
  Group = -> [Po_element001]
  conduct = 2
  density = 1
  expand = 3
  formula = Po
  name = G4_Po
  specific = 4
FEATURE [App::DocumentObjectGroupPython] At_element001  label="At_element : 1"  # scripted group (container) (typed FeaturePython)
  n = 1
  ref = At_element
FEATURE [App::DocumentObjectGroupPython] G4_At  # scripted group (container) (typed FeaturePython)
  Dunit = g/cm3
  Dvalue = 9.32
  Group = -> [At_element001]
  conduct = 2
  density = 1
  expand = 3
  formula = At
  name = G4_At
  specific = 4
FEATURE [App::DocumentObjectGroupPython] Rn_element001  label="Rn_element : 1"  # scripted group (container) (typed FeaturePython)
  n = 1
  ref = Rn_element
FEATURE [App::DocumentObjectGroupPython] G4_Rn  # scripted group (container) (typed FeaturePython)
  Dunit = g/cm3
  Dvalue = 0.00900662
  Group = -> [Rn_element001]
  conduct = 2
  density = 1
  expand = 3
  formula = Rn
  name = G4_Rn
  specific = 4
FEATURE [App::DocumentObjectGroupPython] Fr_element001  label="Fr_element : 1"  # scripted group (container) (typed FeaturePython)
  n = 1
  ref = Fr_element
FEATURE [App::DocumentObjectGroupPython] G4_Fr  # scripted group (container) (typed FeaturePython)
  Dunit = g/cm3
  Dvalue = 1
  Group = -> [Fr_element001]
  conduct = 2
  density = 1
  expand = 3
  formula = Fr
  name = G4_Fr
  specific = 4
FEATURE [App::DocumentObjectGroupPython] Ra_element001  label="Ra_element : 1"  # scripted group (container) (typed FeaturePython)
  n = 1
  ref = Ra_element
FEATURE [App::DocumentObjectGroupPython] G4_Ra  # scripted group (container) (typed FeaturePython)
  Dunit = g/cm3
  Dvalue = 5
  Group = -> [Ra_element001]
  conduct = 2
  density = 1
  expand = 3
  formula = Ra
  name = G4_Ra
  specific = 4
FEATURE [App::DocumentObjectGroupPython] Ac_element001  label="Ac_element : 1"  # scripted group (container) (typed FeaturePython)
  n = 1
  ref = Ac_element
FEATURE [App::DocumentObjectGroupPython] G4_Ac  # scripted group (container) (typed FeaturePython)
  Dunit = g/cm3
  Dvalue = 10.07
  Group = -> [Ac_element001]
  conduct = 2
  density = 1
  expand = 3
  formula = Ac
  name = G4_Ac
  specific = 4
FEATURE [App::DocumentObjectGroupPython] Th_element001  label="Th_element : 1"  # scripted group (container) (typed FeaturePython)
  n = 1
  ref = Th_element
FEATURE [App::DocumentObjectGroupPython] G4_Th  # scripted group (container) (typed FeaturePython)
  Dunit = g/cm3
  Dvalue = 11.72
  Group = -> [Th_element001]
  conduct = 2
  density = 1
  expand = 3
  formula = Th
  name = G4_Th
  specific = 4
FEATURE [App::DocumentObjectGroupPython] Pa_element001  label="Pa_element : 1"  # scripted group (container) (typed FeaturePython)
  n = 1
  ref = Pa_element
FEATURE [App::DocumentObjectGroupPython] G4_Pa  # scripted group (container) (typed FeaturePython)
  Dunit = g/cm3
  Dvalue = 15.37
  Group = -> [Pa_element001]
  conduct = 2
  density = 1
  expand = 3
  formula = Pa
  name = G4_Pa
  specific = 4
FEATURE [App::DocumentObjectGroupPython] U_element004  label="U_element : 004"  # scripted group (container) (typed FeaturePython)
  n = 1
  ref = U_element
FEATURE [App::DocumentObjectGroupPython] G4_U  # scripted group (container) (typed FeaturePython)
  Dunit = g/cm3
  Dvalue = 18.95
  Group = -> [U_element004]
  conduct = 2
  density = 1
  expand = 3
  formula = U
  name = G4_U
  specific = 4
FEATURE [App::DocumentObjectGroupPython] Np_element001  label="Np_element : 1"  # scripted group (container) (typed FeaturePython)
  n = 1
  ref = Np_element
FEATURE [App::DocumentObjectGroupPython] G4_Np  # scripted group (container) (typed FeaturePython)
  Dunit = g/cm3
  Dvalue = 20.25
  Group = -> [Np_element001]
  conduct = 2
  density = 1
  expand = 3
  formula = Np
  name = G4_Np
  specific = 4
FEATURE [App::DocumentObjectGroupPython] Pu_element002  label="Pu_element : 002"  # scripted group (container) (typed FeaturePython)
  n = 1
  ref = Pu_element
FEATURE [App::DocumentObjectGroupPython] G4_Pu  # scripted group (container) (typed FeaturePython)
  Dunit = g/cm3
  Dvalue = 19.84
  Group = -> [Pu_element002]
  conduct = 2
  density = 1
  expand = 3
  formula = Pu
  name = G4_Pu
  specific = 4
FEATURE [App::DocumentObjectGroupPython] Am_element001  label="Am_element : 1"  # scripted group (container) (typed FeaturePython)
  n = 1
  ref = Am_element
FEATURE [App::DocumentObjectGroupPython] G4_Am  # scripted group (container) (typed FeaturePython)
  Dunit = g/cm3
  Dvalue = 13.67
  Group = -> [Am_element001]
  conduct = 2
  density = 1
  expand = 3
  formula = Am
  name = G4_Am
  specific = 4
FEATURE [App::DocumentObjectGroupPython] Cm_element001  label="Cm_element : 1"  # scripted group (container) (typed FeaturePython)
  n = 1
  ref = Cm_element
FEATURE [App::DocumentObjectGroupPython] G4_Cm  # scripted group (container) (typed FeaturePython)
  Dunit = g/cm3
  Dvalue = 13.51
  Group = -> [Cm_element001]
  conduct = 2
  density = 1
  expand = 3
  formula = Cm
  name = G4_Cm
  specific = 4
FEATURE [App::DocumentObjectGroupPython] Bk_element001  label="Bk_element : 1"  # scripted group (container) (typed FeaturePython)
  n = 1
  ref = Bk_element
FEATURE [App::DocumentObjectGroupPython] G4_Bk  # scripted group (container) (typed FeaturePython)
  Dunit = g/cm3
  Dvalue = 14
  Group = -> [Bk_element001]
  conduct = 2
  density = 1
  expand = 3
  formula = Bk
  name = G4_Bk
  specific = 4
FEATURE [App::DocumentObjectGroupPython] Cf_element001  label="Cf_element : 1"  # scripted group (container) (typed FeaturePython)
  n = 1
  ref = Cf_element
FEATURE [App::DocumentObjectGroupPython] G4_Cf  # scripted group (container) (typed FeaturePython)
  Dunit = g/cm3
  Dvalue = 10
  Group = -> [Cf_element001]
  conduct = 2
  density = 1
  expand = 3
  formula = Cf
  name = G4_Cf
  specific = 4
FEATURE [App::DocumentObjectGroupPython] Element  # scripted group (container) (typed FeaturePython)
  Group = -> [G4_H,G4_He,G4_Li,G4_Be,G4_B,G4_C,G4_N,G4_O,G4_F,G4_Ne,G4_Na,G4_Mg,G4_Al,G4_Si,G4_P,G4_S,G4_Cl,G4_Ar,G4_K,G4_Ca,G4_Sc,G4_Ti,G4_V,G4_Cr,G4_Mn,G4_Fe,G4_Co,G4_Ni,G4_Cu,G4_Zn,G4_Ga,G4_Ge,G4_As,G4_Se,G4_Br,G4_Kr,G4_Rb,G4_Sr,G4_Y,G4_Zr,G4_Nb,G4_Mo,G4_Tc,G4_Ru,G4_Rh,G4_Pd,G4_Ag,G4_Cd,G4_In,G4_Sn,G4_Sb,G4_Te,G4_I,G4_Xe,G4_Cs,G4_Ba,G4_La,G4_Ce,G4_Pr,G4_Nd,G4_Pm,G4_Sm,G4_Eu,G4_Gd,G4_Tb,G4_Dy,G4_Ho,G4_Er,+30 more]
FEATURE [App::DocumentObjectGroupPython] H_element114  label="H_element : 063"  # scripted group (container) (typed FeaturePython)
  n = 2
  ref = H_element
FEATURE [App::DocumentObjectGroupPython] G4_lH2  # scripted group (container) (typed FeaturePython)
  Dunit = g/cm3
  Dvalue = 0.0708
  Group = -> [H_element114]
  conduct = 2
  density = 1
  expand = 3
  formula = G4_lH2
  name = G4_lH2
  specific = 4
FEATURE [App::DocumentObjectGroupPython] N_element049  label="N_element : 022"  # scripted group (container) (typed FeaturePython)
  n = 2
  ref = N_element
FEATURE [App::DocumentObjectGroupPython] G4_lN2  # scripted group (container) (typed FeaturePython)
  Dunit = g/cm3
  Dvalue = 0.807
  Group = -> [N_element049]
  conduct = 2
  density = 1
  expand = 3
  formula = G4_lN2
  name = G4_lN2
  specific = 4
FEATURE [App::DocumentObjectGroupPython] O_element106  label="O_element : 060"  # scripted group (container) (typed FeaturePython)
  n = 2
  ref = O_element
FEATURE [App::DocumentObjectGroupPython] G4_lO2  # scripted group (container) (typed FeaturePython)
  Dunit = g/cm3
  Dvalue = 1.141
  Group = -> [O_element106]
  conduct = 2
  density = 1
  expand = 3
  formula = G4_lO2
  name = G4_lO2
  specific = 4
FEATURE [App::DocumentObjectGroupPython] Ar  label="Ar : 1"  # scripted group (container) (typed FeaturePython)
  n = 1
  ref = Ar
FEATURE [App::DocumentObjectGroupPython] G4_lAr  # scripted group (container) (typed FeaturePython)
  Dunit = g/cm3
  Dvalue = 1.396
  Group = -> [Ar]
  conduct = 2
  density = 1
  expand = 3
  formula = G4_lAr
  name = G4_lAr
  specific = 4
FEATURE [App::DocumentObjectGroupPython] Br  label="Br : 1"  # scripted group (container) (typed FeaturePython)
  n = 1
  ref = Br
FEATURE [App::DocumentObjectGroupPython] G4_lBr  # scripted group (container) (typed FeaturePython)
  Dunit = g/cm3
  Dvalue = 3.1028
  Group = -> [Br]
  conduct = 2
  density = 1
  expand = 3
  formula = G4_lBr
  name = G4_lBr
  specific = 4
FEATURE [App::DocumentObjectGroupPython] Kr  label="Kr : 1"  # scripted group (container) (typed FeaturePython)
  n = 1
  ref = Kr
FEATURE [App::DocumentObjectGroupPython] G4_lKr  # scripted group (container) (typed FeaturePython)
  Dunit = g/cm3
  Dvalue = 2.418
  Group = -> [Kr]
  conduct = 2
  density = 1
  expand = 3
  formula = G4_lKr
  name = G4_lKr
  specific = 4
FEATURE [App::DocumentObjectGroupPython] Xe  label="Xe : 1"  # scripted group (container) (typed FeaturePython)
  n = 1
  ref = Xe
FEATURE [App::DocumentObjectGroupPython] G4_lXe  # scripted group (container) (typed FeaturePython)
  Dunit = g/cm3
  Dvalue = 2.953
  Group = -> [Xe]
  conduct = 2
  density = 1
  expand = 3
  formula = G4_lXe
  name = G4_lXe
  specific = 4
FEATURE [App::DocumentObjectGroupPython] O_element107  label="O_element : 061"  # scripted group (container) (typed FeaturePython)
  n = 4
  ref = O_element
FEATURE [App::DocumentObjectGroupPython] Pb_element004  label="Pb_element : 002"  # scripted group (container) (typed FeaturePython)
  n = 1
  ref = Pb_element
FEATURE [App::DocumentObjectGroupPython] W_element005  label="W_element : 005"  # scripted group (container) (typed FeaturePython)
  n = 1
  ref = W_element
FEATURE [App::DocumentObjectGroupPython] G4_PbWO4  # scripted group (container) (typed FeaturePython)
  Dunit = g/cm3
  Dvalue = 8.28
  Group = -> [O_element107,Pb_element004,W_element005]
  conduct = 2
  density = 1
  expand = 3
  formula = G4_PbWO4
  name = G4_PbWO4
  specific = 4
FEATURE [App::DocumentObjectGroupPython] alactic  label="alactic : 1"  # scripted group (container) (typed FeaturePython)
  n = 1
  ref = alactic
FEATURE [App::DocumentObjectGroupPython] G4_Galactic  # scripted group (container) (typed FeaturePython)
  Dunit = g/cm3
  Dvalue = 0
  Group = -> [alactic]
  conduct = 2
  density = 1
  expand = 3
  formula = G4_Galactic
  name = G4_Galactic
  specific = 4
FEATURE [App::DocumentObjectGroupPython] RAPHITE_POROUS  label="RAPHITE_POROUS : 1"  # scripted group (container) (typed FeaturePython)
  n = 1
  ref = RAPHITE_POROUS
FEATURE [App::DocumentObjectGroupPython] G4_GRAPHITE_POROUS  # scripted group (container) (typed FeaturePython)
  Dunit = g/cm3
  Dvalue = 1.7
  Group = -> [RAPHITE_POROUS]
  conduct = 2
  density = 1
  expand = 3
  formula = G4_GRAPHITE_POROUS
  name = G4_GRAPHITE_POROUS
  specific = 4
FEATURE [App::DocumentObjectGroupPython] H_element115  label="H_element : 0.150"  # scripted group (container) (typed FeaturePython)
  n = 0.080538
FEATURE [App::DocumentObjectGroupPython] C_element125  label="C_element : 0.600"  # scripted group (container) (typed FeaturePython)
  n = 0.599848
FEATURE [App::DocumentObjectGroupPython] O_element108  label="O_element : 0.320"  # scripted group (container) (typed FeaturePython)
  n = 0.319614
FEATURE [App::DocumentObjectGroupPython] G4_LUCITE  # scripted group (container) (typed FeaturePython)
  Dunit = g/cm3
  Dvalue = 1.19
  Group = -> [H_element115,C_element125,O_element108]
  conduct = 2
  density = 1
  expand = 3
  formula = G4_LUCITE
  name = G4_LUCITE
  specific = 4
FEATURE [App::DocumentObjectGroupPython] Cu_element002  label="Cu_element : 62"  # scripted group (container) (typed FeaturePython)
  n = 62
  ref = Cu_element
FEATURE [App::DocumentObjectGroupPython] Zn_element002  label="Zn_element : 35"  # scripted group (container) (typed FeaturePython)
  n = 35
  ref = Zn_element
FEATURE [App::DocumentObjectGroupPython] Pb_element005  label="Pb_element : 3"  # scripted group (container) (typed FeaturePython)
  n = 3
  ref = Pb_element
FEATURE [App::DocumentObjectGroupPython] G4_BRASS  # scripted group (container) (typed FeaturePython)
  Dunit = g/cm3
  Dvalue = 8.52
  Group = -> [Cu_element002,Zn_element002,Pb_element005]
  conduct = 2
  density = 1
  expand = 3
  formula = G4_BRASS
  name = G4_BRASS
  specific = 4
FEATURE [App::DocumentObjectGroupPython] Cu_element003  label="Cu_element : 89"  # scripted group (container) (typed FeaturePython)
  n = 89
  ref = Cu_element
FEATURE [App::DocumentObjectGroupPython] Zn_element003  label="Zn_element : 9"  # scripted group (container) (typed FeaturePython)
  n = 9
  ref = Zn_element
FEATURE [App::DocumentObjectGroupPython] Pb_element006  label="Pb_element : 2"  # scripted group (container) (typed FeaturePython)
  n = 2
  ref = Pb_element
FEATURE [App::DocumentObjectGroupPython] G4_BRONZE  # scripted group (container) (typed FeaturePython)
  Dunit = g/cm3
  Dvalue = 8.82
  Group = -> [Cu_element003,Zn_element003,Pb_element006]
  conduct = 2
  density = 1
  expand = 3
  formula = G4_BRONZE
  name = G4_BRONZE
  specific = 4
FEATURE [App::DocumentObjectGroupPython] Fe_element008  label="Fe_element : 74"  # scripted group (container) (typed FeaturePython)
  n = 74
  ref = Fe_element
FEATURE [App::DocumentObjectGroupPython] Cr_element002  label="Cr_element : 18"  # scripted group (container) (typed FeaturePython)
  n = 18
  ref = Cr_element
FEATURE [App::DocumentObjectGroupPython] Ni_element002  label="Ni_element : 8"  # scripted group (container) (typed FeaturePython)
  n = 8
  ref = Ni_element
FEATURE [App::DocumentObjectGroupPython] G4_STAINLESS_STEEL  label="G4_STAINLESS-STEEL"  # scripted group (container) (typed FeaturePython)
  Dunit = g/cm3
  Dvalue = 8
  Group = -> [Fe_element008,Cr_element002,Ni_element002]
  conduct = 2
  density = 1
  expand = 3
  formula = G4_STAINLESS-STEEL
  name = G4_STAINLESS-STEEL
  specific = 4
FEATURE [App::DocumentObjectGroupPython] H_element116  label="H_element : 064"  # scripted group (container) (typed FeaturePython)
  n = 18
  ref = H_element
FEATURE [App::DocumentObjectGroupPython] C_element126  label="C_element : 071"  # scripted group (container) (typed FeaturePython)
  n = 12
  ref = C_element
FEATURE [App::DocumentObjectGroupPython] O_element109  label="O_element : 062"  # scripted group (container) (typed FeaturePython)
  n = 7
  ref = O_element
FEATURE [App::DocumentObjectGroupPython] G4_CR39  # scripted group (container) (typed FeaturePython)
  Dunit = g/cm3
  Dvalue = 1.32
  Group = -> [H_element116,C_element126,O_element109]
  conduct = 2
  density = 1
  expand = 3
  formula = G4_CR39
  name = G4_CR39
  specific = 4
FEATURE [App::DocumentObjectGroupPython] H_element117  label="H_element : 38"  # scripted group (container) (typed FeaturePython)
  n = 38
  ref = H_element
FEATURE [App::DocumentObjectGroupPython] C_element127  label="C_element : 072"  # scripted group (container) (typed FeaturePython)
  n = 18
  ref = C_element
FEATURE [App::DocumentObjectGroupPython] O_element110  label="O_element : 063"  # scripted group (container) (typed FeaturePython)
  n = 1
  ref = O_element
FEATURE [App::DocumentObjectGroupPython] G4_OCTADECANOL  # scripted group (container) (typed FeaturePython)
  Dunit = g/cm3
  Dvalue = 0.812
  Group = -> [H_element117,C_element127,O_element110]
  conduct = 2
  density = 1
  expand = 3
  formula = G4_OCTADECANOL
  name = G4_OCTADECANOL
  specific = 4
FEATURE [App::DocumentObjectGroupPython] HEP  # scripted group (container) (typed FeaturePython)
  Group = -> [G4_lH2,G4_lN2,G4_lO2,G4_lAr,G4_lBr,G4_lKr,G4_lXe,G4_PbWO4,G4_Galactic,G4_GRAPHITE_POROUS,G4_LUCITE,G4_BRASS,G4_BRONZE,G4_STAINLESS_STEEL,G4_CR39,G4_OCTADECANOL]
FEATURE [App::DocumentObjectGroupPython] C_element128  label="C_element : 073"  # scripted group (container) (typed FeaturePython)
  n = 14
  ref = C_element
FEATURE [App::DocumentObjectGroupPython] H_element118  label="H_element : 065"  # scripted group (container) (typed FeaturePython)
  n = 10
  ref = H_element
FEATURE [App::DocumentObjectGroupPython] O_element111  label="O_element : 064"  # scripted group (container) (typed FeaturePython)
  n = 2
  ref = O_element
FEATURE [App::DocumentObjectGroupPython] N_element050  label="N_element : 023"  # scripted group (container) (typed FeaturePython)
  n = 2
  ref = N_element
FEATURE [App::DocumentObjectGroupPython] G4_KEVLAR  # scripted group (container) (typed FeaturePython)
  Dunit = g/cm3
  Dvalue = 1.44
  Group = -> [C_element128,H_element118,O_element111,N_element050]
  conduct = 2
  density = 1
  expand = 3
  formula = G4_KEVLAR
  name = G4_KEVLAR
  specific = 4
FEATURE [App::DocumentObjectGroupPython] C_element129  label="C_element : 074"  # scripted group (container) (typed FeaturePython)
  n = 10
  ref = C_element
FEATURE [App::DocumentObjectGroupPython] H_element119  label="H_element : 066"  # scripted group (container) (typed FeaturePython)
  n = 8
  ref = H_element
FEATURE [App::DocumentObjectGroupPython] O_element112  label="O_element : 065"  # scripted group (container) (typed FeaturePython)
  n = 4
  ref = O_element
FEATURE [App::DocumentObjectGroupPython] G4_DACRON  # scripted group (container) (typed FeaturePython)
  Dunit = g/cm3
  Dvalue = 1.4
  Group = -> [C_element129,H_element119,O_element112]
  conduct = 2
  density = 1
  expand = 3
  formula = G4_DACRON
  name = G4_DACRON
  specific = 4
FEATURE [App::DocumentObjectGroupPython] C_element130  label="C_element : 075"  # scripted group (container) (typed FeaturePython)
  n = 4
  ref = C_element
FEATURE [App::DocumentObjectGroupPython] H_element120  label="H_element : 067"  # scripted group (container) (typed FeaturePython)
  n = 5
  ref = H_element
FEATURE [App::DocumentObjectGroupPython] Cl_element030  label="Cl_element : 016"  # scripted group (container) (typed FeaturePython)
  n = 1
  ref = Cl_element
FEATURE [App::DocumentObjectGroupPython] G4_NEOPRENE  # scripted group (container) (typed FeaturePython)
  Dunit = g/cm3
  Dvalue = 1.23
  Group = -> [C_element130,H_element120,Cl_element030]
  conduct = 2
  density = 1
  expand = 3
  formula = G4_NEOPRENE
  name = G4_NEOPRENE
  specific = 4
FEATURE [App::DocumentObjectGroupPython] Space  # scripted group (container) (typed FeaturePython)
  Group = -> [G4_KEVLAR,G4_DACRON,G4_NEOPRENE]
FEATURE [App::DocumentObjectGroupPython] H_element121  label="H_element : 068"  # scripted group (container) (typed FeaturePython)
  n = 5
  ref = H_element
FEATURE [App::DocumentObjectGroupPython] C_element131  label="C_element : 076"  # scripted group (container) (typed FeaturePython)
  n = 4
  ref = C_element
FEATURE [App::DocumentObjectGroupPython] N_element051  label="N_element : 3"  # scripted group (container) (typed FeaturePython)
  n = 3
  ref = N_element
FEATURE [App::DocumentObjectGroupPython] O_element113  label="O_element : 066"  # scripted group (container) (typed FeaturePython)
  n = 1
  ref = O_element
FEATURE [App::DocumentObjectGroupPython] G4_CYTOSINE  # scripted group (container) (typed FeaturePython)
  Dunit = g/cm3
  Dvalue = 1.55
  Group = -> [H_element121,C_element131,N_element051,O_element113]
  conduct = 2
  density = 1
  expand = 3
  formula = G4_CYTOSINE
  name = G4_CYTOSINE
  specific = 4
FEATURE [App::DocumentObjectGroupPython] H_element122  label="H_element : 069"  # scripted group (container) (typed FeaturePython)
  n = 6
  ref = H_element
FEATURE [App::DocumentObjectGroupPython] C_element132  label="C_element : 077"  # scripted group (container) (typed FeaturePython)
  n = 5
  ref = C_element
FEATURE [App::DocumentObjectGroupPython] N_element052  label="N_element : 024"  # scripted group (container) (typed FeaturePython)
  n = 2
  ref = N_element
FEATURE [App::DocumentObjectGroupPython] O_element114  label="O_element : 067"  # scripted group (container) (typed FeaturePython)
  n = 2
  ref = O_element
FEATURE [App::DocumentObjectGroupPython] G4_THYMINE  # scripted group (container) (typed FeaturePython)
  Dunit = g/cm3
  Dvalue = 1.23
  Group = -> [H_element122,C_element132,N_element052,O_element114]
  conduct = 2
  density = 1
  expand = 3
  formula = G4_THYMINE
  name = G4_THYMINE
  specific = 4
FEATURE [App::DocumentObjectGroupPython] H_element123  label="H_element : 070"  # scripted group (container) (typed FeaturePython)
  n = 4
  ref = H_element
FEATURE [App::DocumentObjectGroupPython] C_element133  label="C_element : 078"  # scripted group (container) (typed FeaturePython)
  n = 4
  ref = C_element
FEATURE [App::DocumentObjectGroupPython] N_element053  label="N_element : 025"  # scripted group (container) (typed FeaturePython)
  n = 2
  ref = N_element
FEATURE [App::DocumentObjectGroupPython] O_element115  label="O_element : 068"  # scripted group (container) (typed FeaturePython)
  n = 2
  ref = O_element
FEATURE [App::DocumentObjectGroupPython] G4_URACIL  # scripted group (container) (typed FeaturePython)
  Dunit = g/cm3
  Dvalue = 1.32
  Group = -> [H_element123,C_element133,N_element053,O_element115]
  conduct = 2
  density = 1
  expand = 3
  formula = G4_URACIL
  name = G4_URACIL
  specific = 4
FEATURE [App::DocumentObjectGroupPython] H_element124  label="H_element : 071"  # scripted group (container) (typed FeaturePython)
  n = 4
  ref = H_element
FEATURE [App::DocumentObjectGroupPython] C_element134  label="C_element : 079"  # scripted group (container) (typed FeaturePython)
  n = 5
  ref = C_element
FEATURE [App::DocumentObjectGroupPython] N_element054  label="N_element : 026"  # scripted group (container) (typed FeaturePython)
  n = 5
  ref = N_element
FEATURE [App::DocumentObjectGroupPython] G4_DNA_ADENINE  # scripted group (container) (typed FeaturePython)
  Dunit = g/cm3
  Dvalue = 1
  Group = -> [H_element124,C_element134,N_element054]
  conduct = 2
  density = 1
  expand = 3
  formula = G4_DNA_ADENINE
  name = G4_DNA_ADENINE
  specific = 4
FEATURE [App::DocumentObjectGroupPython] H_element125  label="H_element : 072"  # scripted group (container) (typed FeaturePython)
  n = 4
  ref = H_element
FEATURE [App::DocumentObjectGroupPython] C_element135  label="C_element : 080"  # scripted group (container) (typed FeaturePython)
  n = 5
  ref = C_element
FEATURE [App::DocumentObjectGroupPython] N_element055  label="N_element : 027"  # scripted group (container) (typed FeaturePython)
  n = 5
  ref = N_element
FEATURE [App::DocumentObjectGroupPython] O_element116  label="O_element : 069"  # scripted group (container) (typed FeaturePython)
  n = 1
  ref = O_element
FEATURE [App::DocumentObjectGroupPython] G4_DNA_GUANINE  # scripted group (container) (typed FeaturePython)
  Dunit = g/cm3
  Dvalue = 1
  Group = -> [H_element125,C_element135,N_element055,O_element116]
  conduct = 2
  density = 1
  expand = 3
  formula = G4_DNA_GUANINE
  name = G4_DNA_GUANINE
  specific = 4
FEATURE [App::DocumentObjectGroupPython] H_element126  label="H_element : 073"  # scripted group (container) (typed FeaturePython)
  n = 4
  ref = H_element
FEATURE [App::DocumentObjectGroupPython] C_element136  label="C_element : 081"  # scripted group (container) (typed FeaturePython)
  n = 4
  ref = C_element
FEATURE [App::DocumentObjectGroupPython] N_element056  label="N_element : 028"  # scripted group (container) (typed FeaturePython)
  n = 3
  ref = N_element
FEATURE [App::DocumentObjectGroupPython] O_element117  label="O_element : 070"  # scripted group (container) (typed FeaturePython)
  n = 1
  ref = O_element
FEATURE [App::DocumentObjectGroupPython] G4_DNA_CYTOSINE  # scripted group (container) (typed FeaturePython)
  Dunit = g/cm3
  Dvalue = 1
  Group = -> [H_element126,C_element136,N_element056,O_element117]
  conduct = 2
  density = 1
  expand = 3
  formula = G4_DNA_CYTOSINE
  name = G4_DNA_CYTOSINE
  specific = 4
FEATURE [App::DocumentObjectGroupPython] H_element127  label="H_element : 074"  # scripted group (container) (typed FeaturePython)
  n = 5
  ref = H_element
FEATURE [App::DocumentObjectGroupPython] C_element137  label="C_element : 082"  # scripted group (container) (typed FeaturePython)
  n = 5
  ref = C_element
FEATURE [App::DocumentObjectGroupPython] N_element057  label="N_element : 029"  # scripted group (container) (typed FeaturePython)
  n = 2
  ref = N_element
FEATURE [App::DocumentObjectGroupPython] O_element118  label="O_element : 071"  # scripted group (container) (typed FeaturePython)
  n = 2
  ref = O_element
FEATURE [App::DocumentObjectGroupPython] G4_DNA_THYMINE  # scripted group (container) (typed FeaturePython)
  Dunit = g/cm3
  Dvalue = 1
  Group = -> [H_element127,C_element137,N_element057,O_element118]
  conduct = 2
  density = 1
  expand = 3
  formula = G4_DNA_THYMINE
  name = G4_DNA_THYMINE
  specific = 4
FEATURE [App::DocumentObjectGroupPython] H_element128  label="H_element : 075"  # scripted group (container) (typed FeaturePython)
  n = 3
  ref = H_element
FEATURE [App::DocumentObjectGroupPython] C_element138  label="C_element : 083"  # scripted group (container) (typed FeaturePython)
  n = 4
  ref = C_element
FEATURE [App::DocumentObjectGroupPython] N_element058  label="N_element : 030"  # scripted group (container) (typed FeaturePython)
  n = 2
  ref = N_element
FEATURE [App::DocumentObjectGroupPython] O_element119  label="O_element : 072"  # scripted group (container) (typed FeaturePython)
  n = 2
  ref = O_element
FEATURE [App::DocumentObjectGroupPython] G4_DNA_URACIL  # scripted group (container) (typed FeaturePython)
  Dunit = g/cm3
  Dvalue = 1
  Group = -> [H_element128,C_element138,N_element058,O_element119]
  conduct = 2
  density = 1
  expand = 3
  formula = G4_DNA_URACIL
  name = G4_DNA_URACIL
  specific = 4
FEATURE [App::DocumentObjectGroupPython] H_element129  label="H_element : 076"  # scripted group (container) (typed FeaturePython)
  n = 10
  ref = H_element
FEATURE [App::DocumentObjectGroupPython] C_element139  label="C_element : 084"  # scripted group (container) (typed FeaturePython)
  n = 10
  ref = C_element
FEATURE [App::DocumentObjectGroupPython] N_element059  label="N_element : 031"  # scripted group (container) (typed FeaturePython)
  n = 5
  ref = N_element
FEATURE [App::DocumentObjectGroupPython] O_element120  label="O_element : 073"  # scripted group (container) (typed FeaturePython)
  n = 4
  ref = O_element
FEATURE [App::DocumentObjectGroupPython] G4_DNA_ADENOSINE  # scripted group (container) (typed FeaturePython)
  Dunit = g/cm3
  Dvalue = 1
  Group = -> [H_element129,C_element139,N_element059,O_element120]
  conduct = 2
  density = 1
  expand = 3
  formula = G4_DNA_ADENOSINE
  name = G4_DNA_ADENOSINE
  specific = 4
FEATURE [App::DocumentObjectGroupPython] H_element130  label="H_element : 077"  # scripted group (container) (typed FeaturePython)
  n = 10
  ref = H_element
FEATURE [App::DocumentObjectGroupPython] C_element140  label="C_element : 085"  # scripted group (container) (typed FeaturePython)
  n = 10
  ref = C_element
FEATURE [App::DocumentObjectGroupPython] N_element060  label="N_element : 032"  # scripted group (container) (typed FeaturePython)
  n = 5
  ref = N_element
FEATURE [App::DocumentObjectGroupPython] O_element121  label="O_element : 074"  # scripted group (container) (typed FeaturePython)
  n = 5
  ref = O_element
FEATURE [App::DocumentObjectGroupPython] G4_DNA_GUANOSINE  # scripted group (container) (typed FeaturePython)
  Dunit = g/cm3
  Dvalue = 1
  Group = -> [H_element130,C_element140,N_element060,O_element121]
  conduct = 2
  density = 1
  expand = 3
  formula = G4_DNA_GUANOSINE
  name = G4_DNA_GUANOSINE
  specific = 4
FEATURE [App::DocumentObjectGroupPython] H_element131  label="H_element : 078"  # scripted group (container) (typed FeaturePython)
  n = 10
  ref = H_element
FEATURE [App::DocumentObjectGroupPython] C_element141  label="C_element : 086"  # scripted group (container) (typed FeaturePython)
  n = 9
  ref = C_element
FEATURE [App::DocumentObjectGroupPython] N_element061  label="N_element : 033"  # scripted group (container) (typed FeaturePython)
  n = 3
  ref = N_element
FEATURE [App::DocumentObjectGroupPython] O_element122  label="O_element : 075"  # scripted group (container) (typed FeaturePython)
  n = 5
  ref = O_element
FEATURE [App::DocumentObjectGroupPython] G4_DNA_CYTIDINE  # scripted group (container) (typed FeaturePython)
  Dunit = g/cm3
  Dvalue = 1
  Group = -> [H_element131,C_element141,N_element061,O_element122]
  conduct = 2
  density = 1
  expand = 3
  formula = G4_DNA_CYTIDINE
  name = G4_DNA_CYTIDINE
  specific = 4
FEATURE [App::DocumentObjectGroupPython] H_element132  label="H_element : 079"  # scripted group (container) (typed FeaturePython)
  n = 9
  ref = H_element
FEATURE [App::DocumentObjectGroupPython] C_element142  label="C_element : 087"  # scripted group (container) (typed FeaturePython)
  n = 9
  ref = C_element
FEATURE [App::DocumentObjectGroupPython] N_element062  label="N_element : 034"  # scripted group (container) (typed FeaturePython)
  n = 2
  ref = N_element
FEATURE [App::DocumentObjectGroupPython] O_element123  label="O_element : 076"  # scripted group (container) (typed FeaturePython)
  n = 6
  ref = O_element
FEATURE [App::DocumentObjectGroupPython] G4_DNA_URIDINE  # scripted group (container) (typed FeaturePython)
  Dunit = g/cm3
  Dvalue = 1
  Group = -> [H_element132,C_element142,N_element062,O_element123]
  conduct = 2
  density = 1
  expand = 3
  formula = G4_DNA_URIDINE
  name = G4_DNA_URIDINE
  specific = 4
FEATURE [App::DocumentObjectGroupPython] H_element133  label="H_element : 080"  # scripted group (container) (typed FeaturePython)
  n = 11
  ref = H_element
FEATURE [App::DocumentObjectGroupPython] C_element143  label="C_element : 088"  # scripted group (container) (typed FeaturePython)
  n = 10
  ref = C_element
FEATURE [App::DocumentObjectGroupPython] N_element063  label="N_element : 035"  # scripted group (container) (typed FeaturePython)
  n = 2
  ref = N_element
FEATURE [App::DocumentObjectGroupPython] O_element124  label="O_element : 077"  # scripted group (container) (typed FeaturePython)
  n = 6
  ref = O_element
FEATURE [App::DocumentObjectGroupPython] G4_DNA_METHYLURIDINE  # scripted group (container) (typed FeaturePython)
  Dunit = g/cm3
  Dvalue = 1
  Group = -> [H_element133,C_element143,N_element063,O_element124]
  conduct = 2
  density = 1
  expand = 3
  formula = G4_DNA_METHYLURIDINE
  name = G4_DNA_METHYLURIDINE
  specific = 4
FEATURE [App::DocumentObjectGroupPython] P_element014  label="P_element : 003"  # scripted group (container) (typed FeaturePython)
  n = 1
  ref = P_element
FEATURE [App::DocumentObjectGroupPython] O_element125  label="O_element : 078"  # scripted group (container) (typed FeaturePython)
  n = 3
  ref = O_element
FEATURE [App::DocumentObjectGroupPython] G4_DNA_MONOPHOSPHATE  # scripted group (container) (typed FeaturePython)
  Dunit = g/cm3
  Dvalue = 1
  Group = -> [P_element014,O_element125]
  conduct = 2
  density = 1
  expand = 3
  formula = G4_DNA_MONOPHOSPHATE
  name = G4_DNA_MONOPHOSPHATE
  specific = 4
FEATURE [App::DocumentObjectGroupPython] H_element134  label="H_element : 081"  # scripted group (container) (typed FeaturePython)
  n = 10
  ref = H_element
FEATURE [App::DocumentObjectGroupPython] C_element144  label="C_element : 089"  # scripted group (container) (typed FeaturePython)
  n = 10
  ref = C_element
FEATURE [App::DocumentObjectGroupPython] N_element064  label="N_element : 036"  # scripted group (container) (typed FeaturePython)
  n = 5
  ref = N_element
FEATURE [App::DocumentObjectGroupPython] O_element126  label="O_element : 079"  # scripted group (container) (typed FeaturePython)
  n = 7
  ref = O_element
FEATURE [App::DocumentObjectGroupPython] P_element015  label="P_element : 004"  # scripted group (container) (typed FeaturePython)
  n = 1
  ref = P_element
FEATURE [App::DocumentObjectGroupPython] G4_DNA_A  # scripted group (container) (typed FeaturePython)
  Dunit = g/cm3
  Dvalue = 1
  Group = -> [H_element134,C_element144,N_element064,O_element126,P_element015]
  conduct = 2
  density = 1
  expand = 3
  formula = G4_DNA_A
  name = G4_DNA_A
  specific = 4
FEATURE [App::DocumentObjectGroupPython] H_element135  label="H_element : 082"  # scripted group (container) (typed FeaturePython)
  n = 10
  ref = H_element
FEATURE [App::DocumentObjectGroupPython] C_element145  label="C_element : 090"  # scripted group (container) (typed FeaturePython)
  n = 10
  ref = C_element
FEATURE [App::DocumentObjectGroupPython] N_element065  label="N_element : 037"  # scripted group (container) (typed FeaturePython)
  n = 5
  ref = N_element
FEATURE [App::DocumentObjectGroupPython] O_element127  label="O_element : 8"  # scripted group (container) (typed FeaturePython)
  n = 8
  ref = O_element
FEATURE [App::DocumentObjectGroupPython] P_element016  label="P_element : 005"  # scripted group (container) (typed FeaturePython)
  n = 1
  ref = P_element
FEATURE [App::DocumentObjectGroupPython] G4_DNA_G  # scripted group (container) (typed FeaturePython)
  Dunit = g/cm3
  Dvalue = 1
  Group = -> [H_element135,C_element145,N_element065,O_element127,P_element016]
  conduct = 2
  density = 1
  expand = 3
  formula = G4_DNA_G
  name = G4_DNA_G
  specific = 4
FEATURE [App::DocumentObjectGroupPython] H_element136  label="H_element : 083"  # scripted group (container) (typed FeaturePython)
  n = 10
  ref = H_element
FEATURE [App::DocumentObjectGroupPython] C_element146  label="C_element : 091"  # scripted group (container) (typed FeaturePython)
  n = 9
  ref = C_element
FEATURE [App::DocumentObjectGroupPython] N_element066  label="N_element : 038"  # scripted group (container) (typed FeaturePython)
  n = 3
  ref = N_element
FEATURE [App::DocumentObjectGroupPython] O_element128  label="O_element : 080"  # scripted group (container) (typed FeaturePython)
  n = 8
  ref = O_element
FEATURE [App::DocumentObjectGroupPython] P_element017  label="P_element : 006"  # scripted group (container) (typed FeaturePython)
  n = 1
  ref = P_element
FEATURE [App::DocumentObjectGroupPython] G4_DNA_C  # scripted group (container) (typed FeaturePython)
  Dunit = g/cm3
  Dvalue = 1
  Group = -> [H_element136,C_element146,N_element066,O_element128,P_element017]
  conduct = 2
  density = 1
  expand = 3
  formula = G4_DNA_C
  name = G4_DNA_C
  specific = 4
FEATURE [App::DocumentObjectGroupPython] H_element137  label="H_element : 084"  # scripted group (container) (typed FeaturePython)
  n = 9
  ref = H_element
FEATURE [App::DocumentObjectGroupPython] C_element147  label="C_element : 092"  # scripted group (container) (typed FeaturePython)
  n = 9
  ref = C_element
FEATURE [App::DocumentObjectGroupPython] N_element067  label="N_element : 039"  # scripted group (container) (typed FeaturePython)
  n = 2
  ref = N_element
FEATURE [App::DocumentObjectGroupPython] O_element129  label="O_element : 9"  # scripted group (container) (typed FeaturePython)
  n = 9
  ref = O_element
FEATURE [App::DocumentObjectGroupPython] P_element018  label="P_element : 007"  # scripted group (container) (typed FeaturePython)
  n = 1
  ref = P_element
FEATURE [App::DocumentObjectGroupPython] G4_DNA_U  # scripted group (container) (typed FeaturePython)
  Dunit = g/cm3
  Dvalue = 1
  Group = -> [H_element137,C_element147,N_element067,O_element129,P_element018]
  conduct = 2
  density = 1
  expand = 3
  formula = G4_DNA_U
  name = G4_DNA_U
  specific = 4
FEATURE [App::DocumentObjectGroupPython] H_element138  label="H_element : 085"  # scripted group (container) (typed FeaturePython)
  n = 11
  ref = H_element
FEATURE [App::DocumentObjectGroupPython] C_element148  label="C_element : 093"  # scripted group (container) (typed FeaturePython)
  n = 10
  ref = C_element
FEATURE [App::DocumentObjectGroupPython] N_element068  label="N_element : 040"  # scripted group (container) (typed FeaturePython)
  n = 2
  ref = N_element
FEATURE [App::DocumentObjectGroupPython] O_element130  label="O_element : 081"  # scripted group (container) (typed FeaturePython)
  n = 9
  ref = O_element
FEATURE [App::DocumentObjectGroupPython] P_element019  label="P_element : 008"  # scripted group (container) (typed FeaturePython)
  n = 1
  ref = P_element
FEATURE [App::DocumentObjectGroupPython] G4_DNA_MU  # scripted group (container) (typed FeaturePython)
  Dunit = g/cm3
  Dvalue = 1
  Group = -> [H_element138,C_element148,N_element068,O_element130,P_element019]
  conduct = 2
  density = 1
  expand = 3
  formula = G4_DNA_MU
  name = G4_DNA_MU
  specific = 4
FEATURE [App::DocumentObjectGroupPython] BioChemical  # scripted group (container) (typed FeaturePython)
  Group = -> [G4_CYTOSINE,G4_THYMINE,G4_URACIL,G4_DNA_ADENINE,G4_DNA_GUANINE,G4_DNA_CYTOSINE,G4_DNA_THYMINE,G4_DNA_URACIL,G4_DNA_ADENOSINE,G4_DNA_GUANOSINE,G4_DNA_CYTIDINE,G4_DNA_URIDINE,G4_DNA_METHYLURIDINE,G4_DNA_MONOPHOSPHATE,G4_DNA_A,G4_DNA_G,G4_DNA_C,G4_DNA_U,G4_DNA_MU]
FEATURE [App::DocumentObjectGroupPython] G4Materials  # scripted group (container) (typed FeaturePython)
  Group = -> [NIST,Element,HEP,Space,BioChemical]
  version = 1
FEATURE [App::DocumentObjectGroupPython] Geant4  # scripted group (container) (typed FeaturePython)
  Group = -> [G4Isotopes,G4Elements,G4Materials]
FEATURE [App::DocumentObjectGroupPython] Materials  # scripted group (container) (typed FeaturePython)
  Group = -> [Geant4]
FEATURE [Part::FeaturePython] GDMLBox_WorldBox  # WARN: FeaturePython — macro-defined, semantics opaque (R4)
  lunit = 2
  material = 5
  x = 100
  y = 100
  z = 100
FEATURE [Sketcher::SketchObject] Sketch
  FullyConstrained = false
  sketch-geometry (15):
    g0-g5: Circle x6 (B-spline internal-alignment scaffolding for g6; pole/knot coordinates omitted)
    g6: BSplineCurve PolesCount=7 KnotsCount=5 Degree=3 IsPeriodic=0
    g7-g10: GeomPoint x4 (B-spline internal-alignment scaffolding for g6; pole/knot coordinates omitted)
    g11: LineSegment StartX=-4.39557 StartY=8.39124 StartZ=0 EndX=-5.2662 EndY=10.5884 EndZ=0
    g12: LineSegment StartX=-5.2662 StartY=10.5884 StartZ=0 EndX=-7.82152 EndY=9.89481 EndZ=0
    g13: LineSegment StartX=-7.82152 StartY=9.89481 StartZ=0 EndX=-9.50073 EndY=7.63152 EndZ=0
    g14: ArcOfCircle CenterX=-7.8377 CenterY=5.34547 CenterZ=0 NormalX=0 NormalY=0 NormalZ=1 AngleXU=0 Radius=2.82696 StartAngle=4.84147 EndAngle=8.48291
  constraints (9):
    c: Weight(g0) = 1
    c: Equal(g0, g1-g5) x5
    c: InternalAlignment(g0-g5 -> g6) x6
    c: InternalAlignment(g7-g10 -> g6) x4
    c: Coincident(g11,g6)
    c: Coincident(g11,g12)
    c: Coincident(g12,g13)
    c: Coincident(g14,g13)
    c: Coincident(g14,g6)
FEATURE [Part::Extrusion] Extrude
  Base = -> Sketch
  Dir = (0,0,1)
  DirMode = 2
  FaceMakerClass = Part::FaceMakerBullseye
  LengthFwd = 10
  LengthRev = 0
  Placement = pos=(13,9,0) rot=(0,0,1;0rad)
  Solid = true
  Symmetric = false
  material = 1
FEATURE [Part::Mirroring] Part__Mirroring  label="Extrude_mirror"
  Base = (0,0,0)
  Normal = (1,0,0)
  Source = -> Extrude
  material = 261
FEATURE [App::Part] Part
  Group = -> [Sketch,Extrude,Part__Mirroring]
  Origin = -> Origin001
FEATURE [App::Part] worldVOL
  Group = -> [GDMLBox_WorldBox,Part]
  Origin = -> Origin
